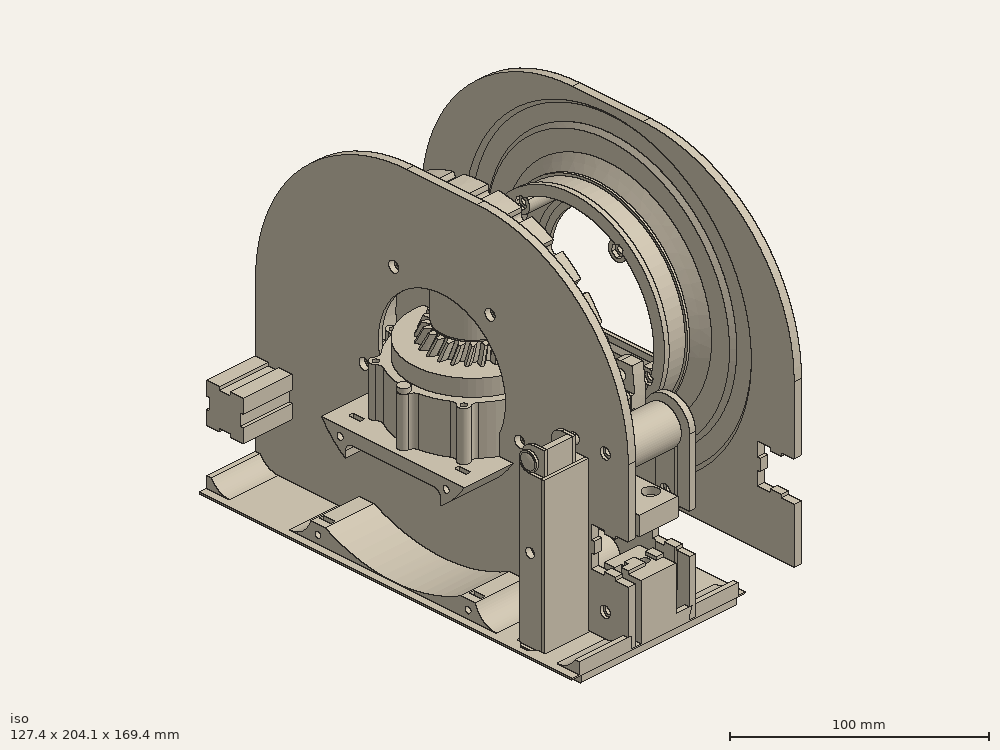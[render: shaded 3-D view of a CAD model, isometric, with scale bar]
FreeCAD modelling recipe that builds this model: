
FCSTD DOCUMENT  (FreeCAD 1.0R38806 (Git))
Label: v12c
License: All rights reserved
LicenseURL: https://en.wikipedia.org/wiki/All_rights_reserved
objects: Sketcher::SketchObject×72, PartDesign::Pad×41, PartDesign::Pocket×27, PartDesign::Body×25, PartDesign::SubShapeBinder×13, PartDesign::Hole×11, PartDesign::Revolution×7, Part::FeaturePython×7, PartDesign::PolarPattern×4, Part::Feature×3, PartDesign::Chamfer×3, App::Part×3, Part::MultiFuse×2, Part::MultiCommon×2, PartDesign::Mirrored×2, App::FeaturePython×1, PartDesign::Groove×1, Part::Cylinder×1, Part::Mirroring×1, App::DocumentObjectGroup×1
note: 480 computed .brp shape members not serialized (recipe doc carries the construction recipe); baked Part::Feature solids carry a one-line shape summary decoded from their .brp

FEATURE [Part::Feature] Body003  label="CyberGear"
  Placement = pos=(0,0,-25) rot=(0,1,0;1.5708rad)
  shape: bbox 80.34 x 79.86 x 36.5 mm, 98 faces (baked)
  expr: .Placement.Base.z = dd.CG_Z
FEATURE [App::FeaturePython] dd  # WARN: FeaturePython — macro-defined, semantics opaque (R4)
  B1_DW = 106.2
  B1_PD = 7
  B1_PL = 10
  CD_Radius = 72.6064
  CG_Z = -25
  CL_BD = 4.9
  CL_BW = 17.4
  CL_Len = 18.2
  CL_Num = 25
  CL_Radius = 6
  D1_X = -30.7
  DynamicData = Created with DynamicData (v2.68) workbench. | This is a simple container object built | for holding custom properties.
  FR_H = 165.613
  FR_W = 204
  G1_Height = 16
  G1_Module = 2
  G1_Num = 24
  G2_Num = 64
  R1_Y = 89.4064
  R2_Y = -56.6064
  R2_Z = -70.8042
  RO_D = 20
  expr: B1_DW = G2_Num * G1_Module - 2 * G1_Height + B1_PD + 3.2 mm
  expr: CD_Radius = CL_Len / (2 * sin(180 / CL_Num))
  expr: CL_BW = 19 - 1.6
  expr: D1_X = -(G1_Num * G1_Module / 2 + CL_BW / 2 - 2 mm)
  expr: FR_H = 2 * (CD_Radius + CL_Radius + 4.2 mm)
  expr: G1_Height = G1_Module * 8
  expr: R1_Y = CD_Radius + CL_Radius + RO_D / 2 + 0.8 mm
  expr: R2_Y = -(CD_Radius - CL_Radius - RO_D / 2)
  expr: R2_Z = -sqrt(pow(R1_Y; 2) - pow(R2_Y; 2)) - 1.6 mm
FEATURE [Sketcher::SketchObject] Sketch  label="CLM_Sketch000"
  ArcFitTolerance = 1e-06
  AttachmentOffset = pos=(0,0,0) rot=(0,1,0;3.14159rad)
  AttachmentSupport = -> [XZ_Plane002]
  FullyConstrained = true
  MakeInternals = false
  MapMode = 5
  Placement = pos=(0,0,0) rot=(0,0.707107,0.707107;3.14159rad)
  expr: Constraints[36] = dd.CL_BW / 2
  sketch-geometry (12):
    g0: LineSegment StartX=-14.7 StartY=4.8 StartZ=0 EndX=-14.7 EndY=2.65 EndZ=0
    g1: LineSegment StartX=-14.7 StartY=2.65 StartZ=0 EndX=-8.7 EndY=2.65 EndZ=0
    g2: LineSegment StartX=-8.7 StartY=2.65 StartZ=0 EndX=-8.7 EndY=2.45 EndZ=0
    g3: LineSegment StartX=-8.7 StartY=2.45 StartZ=0 EndX=10.3 EndY=2.45 EndZ=0
    g4: LineSegment StartX=10.3 StartY=2.45 StartZ=0 EndX=10.3 EndY=4.7 EndZ=0
    g5: LineSegment StartX=-14.7 StartY=4.8 StartZ=0 EndX=-16 EndY=4.8 EndZ=0
    g6: LineSegment StartX=-16 StartY=4.8 StartZ=0 EndX=-16 EndY=3.5 EndZ=0
    g7: LineSegment StartX=-17.0557 StartY=8e-16 StartZ=0 EndX=12.9443 EndY=0 EndZ=0
    g8: LineSegment StartX=11.6 StartY=3.9 StartZ=0 EndX=11.6 EndY=4.7 EndZ=0
    g9: LineSegment StartX=11.6 StartY=4.7 StartZ=0 EndX=10.3 EndY=4.7 EndZ=0
    g10: ArcOfCircle CenterX=-10.7262 CenterY=0 CenterZ=0 NormalX=0 NormalY=0 NormalZ=1 AngleXU=0 Radius=6.3295 StartAngle=2.55567 EndAngle=3.14159
    g11: ArcOfCircle CenterX=6.61476 CenterY=0 CenterZ=0 NormalX=0 NormalY=0 NormalZ=1 AngleXU=0 Radius=6.3295 StartAngle=0 EndAngle=0.66386
  constraints (38):
    c: Vertical(g0)
    c: Coincident(g0,g1)
    c: Horizontal(g1)
    c: Coincident(g1,g2)
    c: Coincident(g2,g3)
    c: Coincident(g3,g4)
    c: Vertical(g4)
    c: Coincident(g0,g5)
    c: Horizontal(g5)
    c: Coincident(g5,g6)
    c: Vertical(g6)
    c: PointOnObject(g7,g-1)
    c: PointOnObject(g7,g-1)
    c: Vertical(g8)
    c: Coincident(g8,g9)
    c: Coincident(g9,g4)
    c: Horizontal(g9)
    c: Vertical(g2)
    c: DistanceX(g3,g3) = 19
    c: DistanceX(g0,g3) = 25
    c: Distance(g5,g-1) = 4.8
    c: DistanceY(g-1,g8) = 4.7
    c: Equal(g5,g9)
    c: Distance(g3,g7) = 2.45
    c: Distance(g0,g7) = 2.65
    c: DistanceX(g9,g9) = 1.3
    c: PointOnObject(g10,g7)
    c: Coincident(g10,g6)
    c: Coincident(g10,g7)
    c: PointOnObject(g11,g7)
    c: Coincident(g11,g8)
    c: Coincident(g11,g7)
    c: Equal(g11,g10)
    c: DistanceX(g7,g7) = 30
    c: Distance(g8,g-1) = 3.9
    c: Equal(g6,g5)
    c: DistanceX(g2,g-1) = 8.7
    c: Horizontal(g3)
FEATURE [PartDesign::Revolution] Revolution  label="CLM_Revolution000"
  Angle = 360
  Angle2 = 60
  Axis = (-1,1e-16,0)
  Base = (0,0,0)
  Placement = pos=(0,0,0) rot=(1,0,0;1.5708rad)
  Profile = -> Sketch
  ReferenceAxis = -> Sketch [H_Axis]
  Refine = true
  Suppressed = false
  Type = 0
FEATURE [PartDesign::Body] Body  label="CLM"
  AllowCompound = false
  Group = -> [Sketch,Revolution]
  Origin = -> Origin002
  Placement = pos=(-30.7,-72.6064,0) rot=(0,0,1;0rad)
  Tip = -> Revolution
  expr: .Placement.Base.x = dd.D1_X
  expr: .Placement.Base.y = -dd.CD_Radius
FEATURE [Sketcher::SketchObject] Sketch001  label="CL1_Sketch001"
  ArcFitTolerance = 1e-06
  AttachmentOffset = pos=(0,0,8.7) rot=(0,0,1;0rad)
  AttachmentSupport = -> [YZ_Plane003]
  FullyConstrained = true
  MakeInternals = false
  MapMode = 5
  Placement = pos=(8.7,0,0) rot=(0.57735,0.57735,0.57735;2.0944rad)
  expr: .AttachmentOffset.Base.z = dd.CL_BW / 2
  expr: Constraints[13] = dd.CL_BD + 0.3 mm
  expr: Constraints[17] = dd.CL_Radius
  expr: Constraints[18] = dd.CL_Radius
  expr: Constraints[19] = dd.CD_Radius
  expr: Constraints[5] = dd.CL_Len
  sketch-geometry (8):
    g0: ArcOfCircle CenterX=0 CenterY=0 CenterZ=0 NormalX=0 NormalY=0 NormalZ=1 AngleXU=0 Radius=6 StartAngle=4.71239 EndAngle=6.28319
    g1: ArcOfCircle CenterX=0 CenterY=18.2 CenterZ=0 NormalX=0 NormalY=0 NormalZ=1 AngleXU=0 Radius=6 StartAngle=0 EndAngle=1.5708
    g2: Circle CenterX=0 CenterY=0 CenterZ=0 NormalX=0 NormalY=0 NormalZ=1 AngleXU=0 Radius=2.6
    g3: Circle CenterX=0 CenterY=18.2 CenterZ=0 NormalX=0 NormalY=0 NormalZ=1 AngleXU=0 Radius=2.6
    g4: LineSegment StartX=6 StartY=18.2 StartZ=0 EndX=6 EndY=0 EndZ=0
    g5: LineSegment StartX=4e-16 StartY=24.2 StartZ=0 EndX=-6 EndY=24.2 EndZ=0
    g6: LineSegment StartX=-1.1e-15 StartY=-6 StartZ=0 EndX=-6 EndY=-6 EndZ=0
    g7: ArcOfCircle CenterX=72.6064 CenterY=9.1 CenterZ=0 NormalX=0 NormalY=0 NormalZ=1 AngleXU=0 Radius=80.0436 StartAngle=2.95181 EndAngle=3.33138
  constraints (20):
    c: Coincident(g0,g-1)
    c: Coincident(g2,g0)
    c: Coincident(g3,g1)
    c: Equal(g3,g2)
    c: PointOnObject(g1,g-2)
    c: DistanceY(g-1,g1) = 18.2
    c: Vertical(g4)
    c: Tangent(g4,g1) = 1.5708
    c: Tangent(g4,g0) = 1.5708
    c: Horizontal(g5)
    c: Horizontal(g6)
    c: Tangent(g0,g6) = 1.5708
    c: Tangent(g1,g5) = -1.5708
    c: Diameter(g3) = 5.2
    c: Coincident(g7,g5)
    c: Coincident(g7,g6)
    c: Equal(g6,g5)
    c: Radius(g1) = 6
    c: DistanceX(g5,g5) = 6
    c: Distance(g7,g-2) = 72.6064
FEATURE [PartDesign::Pad] Pad  label="CL1_Pad000"
  Direction = (1,0,0)
  Length = 6
  Length2 = 10
  Placement = pos=(0,0,0) rot=(1,1,1;2.0944rad)
  Profile = -> Sketch001
  ReferenceAxis = -> Sketch001 [N_Axis]
  Refine = true
  Suppressed = false
  Type = 0
FEATURE [Sketcher::SketchObject] Sketch002  label="CL1_Sketch002"
  ArcFitTolerance = 1e-06
  AttachmentOffset = pos=(0,0,8.7) rot=(0,0,1;0rad)
  AttachmentSupport = -> [YZ_Plane003]
  FullyConstrained = true
  MakeInternals = false
  MapMode = 5
  Placement = pos=(8.7,0,0) rot=(0.57735,0.57735,0.57735;2.0944rad)
  expr: .AttachmentOffset.Base.z = dd.CL_BW / 2
  expr: Constraints[11] = dd.CL_Len
  expr: Constraints[13] = dd.CL_Radius
  expr: Constraints[21] = dd.CL_Radius
  expr: Constraints[26] = dd.CD_Radius
  expr: Constraints[27] = 360 ° / dd.CL_Num
  expr: Constraints[28] = 360 ° / dd.CL_Num
  sketch-geometry (12):
    g0: ArcOfCircle CenterX=0 CenterY=18.2 CenterZ=0 NormalX=0 NormalY=0 NormalZ=1 AngleXU=0 Radius=6 StartAngle=4.71239 EndAngle=6.03186
    g1: ArcOfCircle CenterX=0 CenterY=0 CenterZ=0 NormalX=0 NormalY=0 NormalZ=1 AngleXU=0 Radius=6 StartAngle=0.251327 EndAngle=1.5708
    g2: LineSegment StartX=5.8115 StartY=1.49214 StartZ=0 EndX=6 EndY=0.757976 EndZ=0
    g3: LineSegment StartX=6 StartY=0.757976 StartZ=0 EndX=6 EndY=17.442 EndZ=0
    g4: LineSegment StartX=6 StartY=17.442 StartZ=0 EndX=5.8115 EndY=16.7079 EndZ=0
    g5: LineSegment StartX=-1.1e-15 StartY=12.2 StartZ=0 EndX=-7.37714 EndY=12.2 EndZ=0
    g6: LineSegment StartX=-7.37714 StartY=6 StartZ=0 EndX=-9e-16 EndY=6 EndZ=0
    g7: LineSegment [constr] StartX=0 StartY=18.2 StartZ=0 EndX=0 EndY=24.2 EndZ=0
    g8: LineSegment [constr] StartX=0 StartY=24.2 StartZ=0 EndX=-6 EndY=24.2 EndZ=0
    g9: ArcOfCircle [constr] CenterX=72.6064 CenterY=9.1 CenterZ=0 NormalX=0 NormalY=0 NormalZ=1 AngleXU=0 Radius=80.0436 StartAngle=2.95181 EndAngle=3.10285
    g10: ArcOfCircle CenterX=72.6064 CenterY=9.1 CenterZ=0 NormalX=0 NormalY=0 NormalZ=1 AngleXU=0 Radius=80.0436 StartAngle=3.10285 EndAngle=3.18033
    g11: LineSegment [constr] StartX=0 StartY=9.1 StartZ=0 EndX=6 EndY=9.1 EndZ=0
  constraints (33):
    c: PointOnObject(g0,g-2)
    c: Coincident(g1,g-1)
    c: Coincident(g2,g3)
    c: Vertical(g3)
    c: Coincident(g3,g4)
    c: Horizontal(g5)
    c: Horizontal(g6)
    c: Tangent(g0,g5) = 1.5708
    c: Tangent(g4,g0) = 1.5708
    c: Tangent(g2,g1) = 1.5708
    c: Tangent(g1,g6) = 1.5708
    c: DistanceY(g1,g0) = 18.2
    c: Equal(g1,g0)
    c: Radius(g0) = 6
    c: Coincident(g7,g0)
    c: PointOnObject(g7,g-2)
    c: Coincident(g8,g7)
    c: Horizontal(g8)
    c: Coincident(g9,g8)
    c: Coincident(g9,g5)
    c: Equal(g7,g8)
    c: Distance(g8,g8) = 6
    c: Equal(g5,g6)
    c: Coincident(g10,g9)
    c: Coincident(g10,g5)
    c: Coincident(g10,g6)
    c: Distance(g9,g-2) = 72.6064
    c: Angle(g3,g2) = 0.251327
    c: Angle(g4,g3) = 0.251327
    c: PointOnObject(g11,g-2)
    c: Symmetric(g3,g3,g11)
    c: Horizontal(g11)
    c: Equal(g11,g8)
FEATURE [PartDesign::Pad] Pad001  label="CL1_Pad001"
  BaseFeature = -> Pad
  Direction = (1,0,0)
  Length = 1.6
  Length2 = 10
  Placement = pos=(0,0,0) rot=(1,1,1;2.0944rad)
  Profile = -> Sketch002
  ReferenceAxis = -> Sketch002 [N_Axis]
  Refine = true
  Reversed = true
  Suppressed = false
  Type = 0
FEATURE [Sketcher::SketchObject] Sketch003  label="CL1_Sketch003"
  ArcFitTolerance = 1e-06
  AttachmentOffset = pos=(0,0,8.7) rot=(0,0,1;0rad)
  AttachmentSupport = -> [YZ_Plane003]
  ExternalGeometry = -> [Pad001]
  FullyConstrained = true
  MakeInternals = false
  MapMode = 5
  Placement = pos=(8.7,0,0) rot=(0.57735,0.57735,0.57735;2.0944rad)
  expr: .AttachmentOffset.Base.z = dd.CL_BW / 2
  sketch-geometry (10):
    g0: LineSegment [constr] StartX=-7.37714 StartY=12.2 StartZ=0 EndX=-7.37714 EndY=9.1 EndZ=0
    g1: LineSegment [constr] StartX=-7.37714 StartY=9.1 StartZ=0 EndX=-7.37714 EndY=6 EndZ=0
    g2: LineSegment [constr] StartX=-7.37714 StartY=9.1 StartZ=0 EndX=-4.88857 EndY=9.1 EndZ=0
    g3: LineSegment [constr] StartX=-4.88857 StartY=9.1 StartZ=0 EndX=-2.4 EndY=9.1 EndZ=0
    g4: LineSegment StartX=-6.17714 StartY=11 StartZ=0 EndX=-6.17714 EndY=7.2 EndZ=0
    g5: LineSegment StartX=-6.17714 StartY=7.2 StartZ=0 EndX=-2.4 EndY=7.2 EndZ=0
    g6: LineSegment StartX=-2.4 StartY=7.2 StartZ=0 EndX=-2.4 EndY=11 EndZ=0
    g7: LineSegment StartX=-2.4 StartY=11 StartZ=0 EndX=-6.17714 EndY=11 EndZ=0
    g8: LineSegment [constr] StartX=-7.37714 StartY=12.2 StartZ=0 EndX=-6.17714 EndY=12.2 EndZ=0
    g9: LineSegment [constr] StartX=-6.17714 StartY=12.2 StartZ=0 EndX=-6.17714 EndY=11 EndZ=0
  constraints (27):
    c: Coincident(g0,g-3)
    c: Coincident(g1,g0)
    c: Coincident(g1,g-3)
    c: Coincident(g2,g0)
    c: Horizontal(g2)
    c: Coincident(g3,g2)
    c: Horizontal(g3)
    c: Equal(g1,g0)
    c: Equal(g2,g3)
    c: DistanceX(g3,g-1) = 2.4
    c: Vertical(g1)
    c: Coincident(g4,g5)
    c: Coincident(g5,g6)
    c: Coincident(g6,g7)
    c: Coincident(g7,g4)
    c: Vertical(g4)
    c: Horizontal(g5)
    c: Horizontal(g7)
    c: Coincident(g8,g0)
    c: Horizontal(g8)
    c: Coincident(g9,g8)
    c: Coincident(g9,g4)
    c: Vertical(g9)
    c: Symmetric(g6,g5,g3)
    c: PointOnObject(g3,g6)
    c: Equal(g9,g8)
    c: Distance(g8,g8) = 1.2
FEATURE [PartDesign::Pad] Pad002  label="CL1_Pad002"
  BaseFeature = -> Pad001
  Direction = (1,0,0)
  Length = 18.2
  Length2 = 10
  Placement = pos=(0,0,0) rot=(1,1,1;2.0944rad)
  Profile = -> Sketch003
  ReferenceAxis = -> Sketch003 [N_Axis]
  Refine = true
  Reversed = true
  Suppressed = false
  Type = 0
  expr: Length = dd.CL_BW + 0.8 mm
FEATURE [PartDesign::Body] Body004  label="ChainLink1"
  AllowCompound = false
  Group = -> [Sketch001,Pad,Sketch002,Pad001,Sketch003,Pad002]
  Origin = -> Origin003
  Placement = pos=(0,-72.6064,0) rot=(1,0,0;0rad)
  Tip = -> Pad002
  expr: .Placement.Base.y = -dd.CD_Radius
  expr: .Placement.Rotation.Angle = -180 ° / dd.CL_Num * 0
FEATURE [Sketcher::SketchObject] Sketch004  label="CL2_Sketch004"
  ArcFitTolerance = 1e-06
  AttachmentOffset = pos=(0,0,-8.7) rot=(0,0,1;0rad)
  AttachmentSupport = -> [YZ_Plane004]
  FullyConstrained = true
  MakeInternals = false
  MapMode = 5
  Placement = pos=(-8.7,0,0) rot=(0.57735,0.57735,0.57735;2.0944rad)
  expr: .AttachmentOffset.Base.z = -dd.CL_BW / 2
  expr: Constraints[10] = dd.CL_Len
  expr: Constraints[11] = dd.CD_Radius
  expr: Constraints[12] = dd.CL_Radius
  expr: Constraints[13] = dd.CL_Radius
  expr: Constraints[17] = dd.CL_BD
  sketch-geometry (8):
    g0: ArcOfCircle CenterX=0 CenterY=18.2 CenterZ=0 NormalX=0 NormalY=0 NormalZ=1 AngleXU=0 Radius=6 StartAngle=0 EndAngle=1.5708
    g1: ArcOfCircle CenterX=0 CenterY=0 CenterZ=0 NormalX=0 NormalY=0 NormalZ=1 AngleXU=0 Radius=6 StartAngle=4.71239 EndAngle=6.28319
    g2: ArcOfCircle CenterX=72.6064 CenterY=9.1 CenterZ=0 NormalX=0 NormalY=0 NormalZ=1 AngleXU=0 Radius=80.0436 StartAngle=2.95181 EndAngle=3.33138
    g3: LineSegment StartX=6 StartY=-1.5e-15 StartZ=0 EndX=6 EndY=18.2 EndZ=0
    g4: LineSegment StartX=4e-16 StartY=24.2 StartZ=0 EndX=-6 EndY=24.2 EndZ=0
    g5: LineSegment StartX=-1.1e-15 StartY=-6 StartZ=0 EndX=-6 EndY=-6 EndZ=0
    g6: Circle CenterX=0 CenterY=18.2 CenterZ=0 NormalX=0 NormalY=0 NormalZ=1 AngleXU=0 Radius=2.45
    g7: Circle CenterX=0 CenterY=0 CenterZ=0 NormalX=0 NormalY=0 NormalZ=1 AngleXU=0 Radius=2.45
  constraints (20):
    c: PointOnObject(g0,g-2)
    c: Coincident(g1,g-1)
    c: Vertical(g3)
    c: Horizontal(g4)
    c: Horizontal(g5)
    c: Tangent(g3,g0) = -1.5708
    c: Tangent(g1,g3) = -1.5708
    c: Tangent(g1,g5) = 1.5708
    c: Tangent(g0,g4) = -1.5708
    c: Coincident(g5,g2)
    c: DistanceY(g1,g0) = 18.2
    c: Distance(g2,g-2) = 72.6064
    c: Radius(g0) = 6
    c: DistanceX(g4,g4) = 6
    c: Coincident(g6,g0)
    c: Coincident(g7,g1)
    c: Equal(g7,g6)
    c: Diameter(g7) = 4.9
    c: Coincident(g2,g4)
    c: Equal(g5,g4)
FEATURE [PartDesign::Pad] Pad003  label="CL2_Pad003"
  Direction = (1,0,0)
  Length = 1.6
  Length2 = 10
  Placement = pos=(0,0,0) rot=(1,1,1;2.0944rad)
  Profile = -> Sketch004
  ReferenceAxis = -> Sketch004 [N_Axis]
  Refine = true
  Reversed = true
  Suppressed = false
  Type = 0
FEATURE [Sketcher::SketchObject] Sketch005  label="CL2_Sketch005"
  ArcFitTolerance = 1e-06
  AttachmentOffset = pos=(0,0,-8.7) rot=(0,0,1;0rad)
  AttachmentSupport = -> [YZ_Plane004]
  ExternalGeometry = -> [Pad003]
  FullyConstrained = true
  MakeInternals = false
  MapMode = 5
  Placement = pos=(-8.7,0,0) rot=(0.57735,0.57735,0.57735;2.0944rad)
  expr: .AttachmentOffset.Base.z = -dd.CL_BW / 2
  expr: Constraints[15] = dd.CL_Len
  expr: Constraints[17] = dd.CL_Radius
  expr: Constraints[18] = dd.CL_Radius
  expr: Constraints[19] = 360 ° / dd.CL_Num
  sketch-geometry (9):
    g0: ArcOfCircle CenterX=0 CenterY=18.2 CenterZ=0 NormalX=0 NormalY=0 NormalZ=1 AngleXU=0 Radius=6 StartAngle=4.71239 EndAngle=6.03186
    g1: ArcOfCircle CenterX=0 CenterY=0 CenterZ=0 NormalX=0 NormalY=0 NormalZ=1 AngleXU=0 Radius=6 StartAngle=0.251327 EndAngle=1.5708
    g2: LineSegment StartX=5.8115 StartY=16.7079 StartZ=0 EndX=6 EndY=17.442 EndZ=0
    g3: LineSegment StartX=6 StartY=17.442 StartZ=0 EndX=6 EndY=0.757976 EndZ=0
    g4: LineSegment StartX=6 StartY=0.757976 StartZ=0 EndX=5.8115 EndY=1.49214 EndZ=0
    g5: ArcOfCircle CenterX=72.6064 CenterY=9.1 CenterZ=0 NormalX=0 NormalY=0 NormalZ=1 AngleXU=0 Radius=80.0436 StartAngle=3.10285 EndAngle=3.18033
    g6: LineSegment StartX=-7.37714 StartY=12.2 StartZ=0 EndX=-9e-16 EndY=12.2 EndZ=0
    g7: LineSegment StartX=-7.37714 StartY=6 StartZ=0 EndX=-9e-16 EndY=6 EndZ=0
    g8: LineSegment [constr] StartX=5.8115 StartY=16.7079 StartZ=0 EndX=5.8115 EndY=1.49214 EndZ=0
  constraints (23):
    c: PointOnObject(g0,g-2)
    c: Coincident(g1,g-1)
    c: Coincident(g2,g3)
    c: Vertical(g3)
    c: Coincident(g3,g4)
    c: Tangent(g4,g1) = -1.5708
    c: Tangent(g2,g0) = -1.5708
    c: Coincident(g5,g-3)
    c: Coincident(g6,g5)
    c: Horizontal(g6)
    c: Coincident(g7,g5)
    c: Horizontal(g7)
    c: Tangent(g0,g6) = -1.5708
    c: Tangent(g1,g7) = 1.5708
    c: Equal(g-3,g5)
    c: DistanceY(g1,g0) = 18.2
    c: Equal(g0,g1)
    c: Radius(g0) = 6
    c: DistanceX(g1,g3) = 6
    c: Angle(g3,g4) = 0.251327
    c: Coincident(g8,g0)
    c: Coincident(g8,g1)
    c: Vertical(g8)
FEATURE [PartDesign::Pad] Pad004  label="CL2_Pad004"
  BaseFeature = -> Pad003
  Direction = (1,0,0)
  Length = 1.6
  Length2 = 10
  Placement = pos=(0,0,0) rot=(1,1,1;2.0944rad)
  Profile = -> Sketch005
  ReferenceAxis = -> Sketch005 [N_Axis]
  Refine = true
  Suppressed = false
  Type = 0
FEATURE [Sketcher::SketchObject] Sketch007  label="CL3_Sketch007"
  ArcFitTolerance = 1e-06
  AttachmentOffset = pos=(0,0,8.7) rot=(0,0,1;0rad)
  AttachmentSupport = -> [YZ_Plane005]
  FullyConstrained = true
  MakeInternals = false
  MapMode = 5
  Placement = pos=(8.7,0,0) rot=(0.57735,0.57735,0.57735;2.0944rad)
  expr: .AttachmentOffset.Base.z = dd.CL_BW / 2
  expr: Constraints[16] = dd.CL_Radius
  expr: Constraints[17] = dd.CL_Radius
  expr: Constraints[18] = dd.CD_Radius
  expr: Constraints[2] = dd.CL_Len
  expr: Constraints[4] = dd.CL_BD
  sketch-geometry (8):
    g0: Circle CenterX=0 CenterY=0 CenterZ=0 NormalX=0 NormalY=0 NormalZ=1 AngleXU=0 Radius=2.45
    g1: Circle CenterX=0 CenterY=-18.2 CenterZ=0 NormalX=0 NormalY=0 NormalZ=1 AngleXU=0 Radius=2.45
    g2: ArcOfCircle CenterX=72.6064 CenterY=-9.1 CenterZ=0 NormalX=0 NormalY=0 NormalZ=1 AngleXU=0 Radius=80.0436 StartAngle=2.95181 EndAngle=3.33138
    g3: ArcOfCircle CenterX=0 CenterY=0 CenterZ=0 NormalX=0 NormalY=0 NormalZ=1 AngleXU=0 Radius=6 StartAngle=1e-16 EndAngle=1.5708
    g4: ArcOfCircle CenterX=0 CenterY=-18.2 CenterZ=0 NormalX=0 NormalY=0 NormalZ=1 AngleXU=0 Radius=6 StartAngle=4.71239 EndAngle=6.28319
    g5: LineSegment StartX=-6 StartY=-24.2 StartZ=0 EndX=-9e-16 EndY=-24.2 EndZ=0
    g6: LineSegment StartX=-6 StartY=6 StartZ=0 EndX=0 EndY=6 EndZ=0
    g7: LineSegment StartX=6 StartY=6e-16 StartZ=0 EndX=6 EndY=-18.2 EndZ=0
  constraints (20):
    c: Coincident(g0,g-1)
    c: PointOnObject(g1,g-2)
    c: DistanceY(g1,g0) = 18.2
    c: Equal(g1,g0)
    c: Diameter(g1) = 4.9
    c: Coincident(g3,g0)
    c: Coincident(g4,g1)
    c: Coincident(g5,g2)
    c: Horizontal(g5)
    c: Coincident(g6,g2)
    c: Horizontal(g6)
    c: Vertical(g7)
    c: Tangent(g6,g3) = 1.5708
    c: Tangent(g3,g7) = 1.5708
    c: Tangent(g7,g4) = 1.5708
    c: Tangent(g4,g5) = -1.5708
    c: Radius(g3) = 6
    c: DistanceX(g6,g6) = 6
    c: Distance(g2,g-2) = 72.6064
    c: Equal(g5,g6)
FEATURE [PartDesign::Pad] Pad005  label="CL3_Pad005"
  Direction = (1,0,0)
  Length = 1.6
  Length2 = 10
  Placement = pos=(0,0,0) rot=(1,1,1;2.0944rad)
  Profile = -> Sketch007
  ReferenceAxis = -> Sketch007 [N_Axis]
  Refine = true
  Reversed = true
  Suppressed = false
  Type = 0
FEATURE [Sketcher::SketchObject] Sketch008  label="CL3_Sketch008"
  ArcFitTolerance = 1e-06
  AttachmentOffset = pos=(0,0,8.7) rot=(0,0,1;0rad)
  AttachmentSupport = -> [YZ_Plane005]
  ExternalGeometry = -> [Pad005]
  FullyConstrained = true
  MakeInternals = false
  MapMode = 5
  Placement = pos=(8.7,0,0) rot=(0.57735,0.57735,0.57735;2.0944rad)
  expr: .AttachmentOffset.Base.z = dd.CL_BW / 2
  expr: Constraints[15] = dd.CL_Radius
  expr: Constraints[21] = 360 ° / dd.CL_Num
  expr: Constraints[3] = dd.CL_Len
  expr: Constraints[4] = dd.CL_Radius
  sketch-geometry (9):
    g0: ArcOfCircle CenterX=0 CenterY=-18.2 CenterZ=0 NormalX=0 NormalY=0 NormalZ=1 AngleXU=0 Radius=6 StartAngle=0.251327 EndAngle=1.5708
    g1: ArcOfCircle CenterX=0 CenterY=0 CenterZ=0 NormalX=0 NormalY=0 NormalZ=1 AngleXU=0 Radius=6 StartAngle=4.71239 EndAngle=6.03186
    g2: ArcOfCircle CenterX=72.6064 CenterY=-9.1 CenterZ=0 NormalX=0 NormalY=0 NormalZ=1 AngleXU=0 Radius=80.0436 StartAngle=3.10285 EndAngle=3.18033
    g3: LineSegment StartX=-7.37714 StartY=-6 StartZ=0 EndX=-9e-16 EndY=-6 EndZ=0
    g4: LineSegment StartX=-7.37714 StartY=-12.2 StartZ=0 EndX=-9e-16 EndY=-12.2 EndZ=0
    g5: LineSegment StartX=5.8115 StartY=-1.49214 StartZ=0 EndX=6 EndY=-0.757976 EndZ=0
    g6: LineSegment StartX=6 StartY=-0.757976 StartZ=0 EndX=6 EndY=-17.442 EndZ=0
    g7: LineSegment StartX=6 StartY=-17.442 StartZ=0 EndX=5.8115 EndY=-16.7079 EndZ=0
    g8: LineSegment [constr] StartX=5.8115 StartY=-16.7079 StartZ=0 EndX=5.8115 EndY=-1.49214 EndZ=0
  constraints (23):
    c: PointOnObject(g0,g-2)
    c: Coincident(g1,g-1)
    c: Coincident(g2,g-3)
    c: Distance(g0,g1) = 18.2
    c: Radius(g1) = 6
    c: Equal(g1,g0)
    c: Coincident(g3,g2)
    c: Horizontal(g3)
    c: Coincident(g4,g2)
    c: Horizontal(g4)
    c: Tangent(g1,g3) = -1.5708
    c: Tangent(g0,g4) = 1.5708
    c: Coincident(g5,g6)
    c: Vertical(g6)
    c: Coincident(g6,g7)
    c: Distance(g5,g-2) = 6
    c: Tangent(g1,g5) = -1.5708
    c: Tangent(g0,g7) = -1.5708
    c: Coincident(g8,g0)
    c: Coincident(g8,g1)
    c: Vertical(g8)
    c: Angle(g5,g6) = 0.251327
    c: Equal(g2,g-3)
FEATURE [PartDesign::Pad] Pad006  label="CL3_Pad006"
  BaseFeature = -> Pad005
  Direction = (1,0,0)
  Length = 6
  Length2 = 10
  Placement = pos=(0,0,0) rot=(1,1,1;2.0944rad)
  Profile = -> Sketch008
  ReferenceAxis = -> Sketch008 [N_Axis]
  Refine = true
  Suppressed = false
  Type = 0
FEATURE [Sketcher::SketchObject] Sketch010  label="CL4_Sketch010"
  ArcFitTolerance = 1e-06
  AttachmentOffset = pos=(0,0,-8.7) rot=(0,0,1;0rad)
  AttachmentSupport = -> [YZ_Plane006]
  FullyConstrained = true
  MakeInternals = false
  MapMode = 5
  Placement = pos=(-8.7,0,0) rot=(0.57735,0.57735,0.57735;2.0944rad)
  expr: .AttachmentOffset.Base.z = -dd.CL_BW / 2
  expr: Constraints[16] = dd.CL_Radius
  expr: Constraints[17] = dd.CL_Radius
  expr: Constraints[18] = dd.CD_Radius
  expr: Constraints[2] = dd.CL_Len
  expr: Constraints[4] = dd.CL_BD
  sketch-geometry (8):
    g0: Circle CenterX=0 CenterY=0 CenterZ=0 NormalX=0 NormalY=0 NormalZ=1 AngleXU=0 Radius=2.45
    g1: Circle CenterX=0 CenterY=-18.2 CenterZ=0 NormalX=0 NormalY=0 NormalZ=1 AngleXU=0 Radius=2.45
    g2: ArcOfCircle CenterX=72.6064 CenterY=-9.1 CenterZ=0 NormalX=0 NormalY=0 NormalZ=1 AngleXU=0 Radius=80.0436 StartAngle=2.95181 EndAngle=3.33138
    g3: ArcOfCircle CenterX=0 CenterY=0 CenterZ=0 NormalX=0 NormalY=0 NormalZ=1 AngleXU=0 Radius=6 StartAngle=1e-16 EndAngle=1.5708
    g4: ArcOfCircle CenterX=0 CenterY=-18.2 CenterZ=0 NormalX=0 NormalY=0 NormalZ=1 AngleXU=0 Radius=6 StartAngle=4.71239 EndAngle=6.28319
    g5: LineSegment StartX=-6 StartY=-24.2 StartZ=0 EndX=-9e-16 EndY=-24.2 EndZ=0
    g6: LineSegment StartX=-6 StartY=6 StartZ=0 EndX=0 EndY=6 EndZ=0
    g7: LineSegment StartX=6 StartY=6e-16 StartZ=0 EndX=6 EndY=-18.2 EndZ=0
  constraints (20):
    c: Coincident(g0,g-1)
    c: PointOnObject(g1,g-2)
    c: DistanceY(g1,g0) = 18.2
    c: Equal(g1,g0)
    c: Diameter(g1) = 4.9
    c: Coincident(g3,g0)
    c: Coincident(g4,g1)
    c: Coincident(g5,g2)
    c: Horizontal(g5)
    c: Coincident(g6,g2)
    c: Horizontal(g6)
    c: Vertical(g7)
    c: Tangent(g6,g3) = 1.5708
    c: Tangent(g3,g7) = 1.5708
    c: Tangent(g7,g4) = 1.5708
    c: Tangent(g4,g5) = -1.5708
    c: Radius(g3) = 6
    c: DistanceX(g6,g6) = 6
    c: Distance(g2,g-2) = 72.6064
    c: Equal(g5,g6)
FEATURE [PartDesign::Pad] Pad007  label="CL4_Pad007"
  Direction = (1,0,0)
  Length = 1.6
  Length2 = 10
  Placement = pos=(0,0,0) rot=(1,1,1;2.0944rad)
  Profile = -> Sketch010
  ReferenceAxis = -> Sketch010 [N_Axis]
  Refine = true
  Suppressed = false
  Type = 0
FEATURE [Sketcher::SketchObject] Sketch011  label="CL4_Sketch011"
  ArcFitTolerance = 1e-06
  AttachmentOffset = pos=(0,0,-8.7) rot=(0,0,1;0rad)
  AttachmentSupport = -> [YZ_Plane006]
  ExternalGeometry = -> [Pad007]
  FullyConstrained = true
  MakeInternals = false
  MapMode = 5
  Placement = pos=(-8.7,0,0) rot=(0.57735,0.57735,0.57735;2.0944rad)
  expr: .AttachmentOffset.Base.z = -dd.CL_BW / 2
  expr: Constraints[15] = dd.CL_Radius
  expr: Constraints[21] = 360 ° / dd.CL_Num
  expr: Constraints[3] = dd.CL_Len
  expr: Constraints[4] = dd.CL_Radius
  sketch-geometry (9):
    g0: ArcOfCircle CenterX=0 CenterY=-18.2 CenterZ=0 NormalX=0 NormalY=0 NormalZ=1 AngleXU=0 Radius=6 StartAngle=0.251327 EndAngle=1.5708
    g1: ArcOfCircle CenterX=0 CenterY=0 CenterZ=0 NormalX=0 NormalY=0 NormalZ=1 AngleXU=0 Radius=6 StartAngle=4.71239 EndAngle=6.03186
    g2: ArcOfCircle CenterX=72.6064 CenterY=-9.1 CenterZ=0 NormalX=0 NormalY=0 NormalZ=1 AngleXU=0 Radius=80.0436 StartAngle=3.10285 EndAngle=3.18033
    g3: LineSegment StartX=-7.37714 StartY=-6 StartZ=0 EndX=-9e-16 EndY=-6 EndZ=0
    g4: LineSegment StartX=-7.37714 StartY=-12.2 StartZ=0 EndX=-9e-16 EndY=-12.2 EndZ=0
    g5: LineSegment StartX=5.8115 StartY=-1.49214 StartZ=0 EndX=6 EndY=-0.757976 EndZ=0
    g6: LineSegment StartX=6 StartY=-0.757976 StartZ=0 EndX=6 EndY=-17.442 EndZ=0
    g7: LineSegment StartX=6 StartY=-17.442 StartZ=0 EndX=5.8115 EndY=-16.7079 EndZ=0
    g8: LineSegment [constr] StartX=5.8115 StartY=-16.7079 StartZ=0 EndX=5.8115 EndY=-1.49214 EndZ=0
  constraints (23):
    c: PointOnObject(g0,g-2)
    c: Coincident(g1,g-1)
    c: Coincident(g2,g-3)
    c: Distance(g0,g1) = 18.2
    c: Radius(g1) = 6
    c: Equal(g1,g0)
    c: Coincident(g3,g2)
    c: Horizontal(g3)
    c: Coincident(g4,g2)
    c: Horizontal(g4)
    c: Tangent(g1,g3) = -1.5708
    c: Tangent(g0,g4) = 1.5708
    c: Coincident(g5,g6)
    c: Vertical(g6)
    c: Coincident(g6,g7)
    c: Distance(g5,g-2) = 6
    c: Tangent(g1,g5) = -1.5708
    c: Tangent(g0,g7) = -1.5708
    c: Coincident(g8,g0)
    c: Coincident(g8,g1)
    c: Vertical(g8)
    c: Angle(g5,g6) = 0.251327
    c: Equal(g2,g-3)
FEATURE [PartDesign::Pad] Pad008  label="CL4_Pad008"
  BaseFeature = -> Pad007
  Direction = (1,0,0)
  Length = 1.6
  Length2 = 10
  Placement = pos=(0,0,0) rot=(1,1,1;2.0944rad)
  Profile = -> Sketch011
  ReferenceAxis = -> Sketch011 [N_Axis]
  Refine = true
  Reversed = true
  Suppressed = false
  Type = 0
FEATURE [Part::FeaturePython] LanternGear  label="CD_LanternGear000"  # WARN: FeaturePython — macro-defined, semantics opaque (R4)
  AttacherType = Attacher::AttachEngine3D
  AttachmentOffset = pos=(0,0,-6.7) rot=(0,0,1;0.125664rad)
  AttachmentSupport = -> [YZ_Plane001]
  MapMode = 5
  Placement = pos=(-6.7,0,0) rot=(0.600057,0.529021,0.600057;2.1684rad)
  bolt_radius = 2.45
  head = 0
  height = 13.4
  module = 5.80852
  num_profiles = 10
  num_teeth = 25
  version = 1.3.0
  expr: .AttachmentOffset.Base.z = -height / 2
  expr: .AttachmentOffset.Rotation.Angle = 180 ° / dd.CL_Num
  expr: bolt_radius = dd.CL_BD / 2
  expr: height = dd.CL_BW - 4 mm
  expr: module = 2 * dd.CD_Radius / dd.CL_Num
  expr: num_teeth = dd.CL_Num
FEATURE [Part::FeaturePython] BevelGear  label="CD_BevelGear000"  # WARN: FeaturePython — macro-defined, semantics opaque (R4)
  AttacherType = Attacher::AttachEngine3D
  AttachmentOffset = pos=(0,0,6.7) rot=(0,0,1;0rad)
  AttachmentSupport = -> [YZ_Plane001]
  MapMode = 5
  Placement = pos=(6.7,0,0) rot=(0.57735,0.57735,0.57735;2.0944rad)
  angular_backlash = 0
  backlash = 0
  beta = -5.625
  clearance = 0.1
  dw = 128
  height = 7.5
  module = 2
  num_teeth = 64
  numpoints = 20
  pitch_angle = 69.444
  pressure_angle = 20
  reset_origin = true
  version = 1.3.0
  expr: .AttachmentOffset.Base.z = -dd.G1_Num * dd.G1_Module / 2 - dd.D1_X
  expr: angular_backlash = backlash / dw * 360 ° / pi
  expr: beta = -360 ° / num_teeth
  expr: dw = num_teeth * module
  expr: height = (dd.G1_Height + dd.G1_Module * 2) * dd.G1_Num / dd.G2_Num
  expr: module = dd.G1_Module
  expr: num_teeth = dd.G2_Num
  expr: pitch_angle = atan(dd.G2_Num / dd.G1_Num)
FEATURE [Part::FeaturePython] BevelGear001  label="G1_BevelGear001"  # WARN: FeaturePython — macro-defined, semantics opaque (R4)
  AttacherType = Attacher::AttachEngine3D
  Placement = pos=(0,0,0) rot=(0,0,1;0.1309rad)
  angular_backlash = 0
  backlash = 0
  beta = 5.625
  clearance = 0.1
  dw = 48
  height = 16
  module = 2
  num_teeth = 24
  numpoints = 20
  pitch_angle = 20.556
  pressure_angle = 20
  reset_origin = true
  version = 1.3.0
  expr: .Placement.Rotation.Angle = 180 ° / dd.G1_Num
  expr: angular_backlash = backlash / dw * 360 ° / pi
  expr: beta = 360 ° / dd.G2_Num
  expr: dw = num_teeth * module
  expr: height = dd.G1_Height
  expr: module = dd.G1_Module
  expr: num_teeth = dd.G1_Num
  expr: pitch_angle = 90 ° - <<CD_BevelGear000>>.pitch_angle
FEATURE [Sketcher::SketchObject] Sketch015  label="CD_Sketch015"
  ArcFitTolerance = 1e-06
  AttachmentSupport = -> [XZ_Plane009]
  FullyConstrained = true
  MakeInternals = false
  MapMode = 5
  Placement = pos=(0,0,0) rot=(1,0,0;1.5708rad)
  expr: Constraints[10] = dd.CL_BW - 4 mm
  expr: Constraints[11] = dd.CD_Radius + dd.CL_BD
  expr: Constraints[12] = (dd.G1_Height + dd.G1_Module * 2) * dd.G1_Num / dd.G2_Num
  expr: Constraints[13] = dd.G1_Height
  expr: Constraints[15] = dd.G2_Num * dd.G1_Module / 2
  expr: Constraints[23] = dd.B1_PL
  expr: Constraints[24] = (dd.B1_DW + dd.B1_PD) / 2
  expr: Constraints[33] = dd.G1_Module * 2.5
  sketch-geometry (12):
    g0: LineSegment StartX=14.2 StartY=-48 StartZ=0 EndX=14.2 EndY=-64 EndZ=0
    g1: LineSegment StartX=14.2 StartY=-64 StartZ=0 EndX=6.7 EndY=-64 EndZ=0
    g2: LineSegment StartX=6.7 StartY=-64 StartZ=0 EndX=6.7 EndY=-77.5064 EndZ=0
    g3: LineSegment StartX=6.7 StartY=-77.5064 StartZ=0 EndX=-6.7 EndY=-77.5064 EndZ=0
    g4: LineSegment StartX=-6.7 StartY=-77.5064 StartZ=0 EndX=-6.7 EndY=-55.4 EndZ=0
    g5: LineSegment StartX=-6.7 StartY=-55.4 StartZ=0 EndX=-5.5 EndY=-55.4 EndZ=0
    g6: LineSegment StartX=-5.5 StartY=-55.4 StartZ=0 EndX=-5.5 EndY=-56.6 EndZ=0
    g7: LineSegment StartX=-5.5 StartY=-56.6 StartZ=0 EndX=4.5 EndY=-56.6 EndZ=0
    g8: LineSegment StartX=4.5 StartY=-56.6 StartZ=0 EndX=4.5 EndY=-55.4 EndZ=0
    g9: LineSegment StartX=4.5 StartY=-55.4 StartZ=0 EndX=6.7 EndY=-55.4 EndZ=0
    g10: LineSegment StartX=6.7 StartY=-55.4 StartZ=0 EndX=9.2 EndY=-48 EndZ=0
    g11: LineSegment StartX=9.2 StartY=-48 StartZ=0 EndX=14.2 EndY=-48 EndZ=0
  constraints (35):
    c: Coincident(g11,g0)
    c: Vertical(g0)
    c: Coincident(g0,g1)
    c: Coincident(g1,g2)
    c: Vertical(g2)
    c: Coincident(g2,g3)
    c: Coincident(g3,g4)
    c: Coincident(g4,g5)
    c: Vertical(g4)
    c: Symmetric(g2,g3,g-2)
    c: Distance(g3,g3) = 13.4
    c: Distance(g3,g-1) = 77.5064
    c: Distance(g1,g1) = 7.5
    c: DistanceY(g0,g0) = 16
    c: Horizontal(g1)
    c: Distance(g0,g-1) = 64
    c: Coincident(g5,g6)
    c: Horizontal(g5)
    c: Coincident(g6,g7)
    c: Vertical(g6)
    c: Coincident(g7,g8)
    c: Horizontal(g7)
    c: Vertical(g8)
    c: DistanceX(g7,g7) = 10
    c: Distance(g7,g-1) = 56.6
    c: Coincident(g8,g9)
    c: Coincident(g9,g10)
    c: Horizontal(g9)
    c: Equal(g8,g6)
    c: Equal(g6,g5)
    c: Distance(g5,g5) = 1.2
    c: Coincident(g10,g11)
    c: Horizontal(g11)
    c: Distance(g11,g11) = 5
    c: PointOnObject(g9,g2)
FEATURE [PartDesign::Revolution] Revolution001  label="CD_Revolution001"
  Angle = 360
  Angle2 = 60
  Axis = (1,0,0)
  Base = (0,0,0)
  Placement = pos=(0,0,0) rot=(1,0,0;1.5708rad)
  Profile = -> Sketch015
  ReferenceAxis = -> Sketch015 [H_Axis]
  Refine = true
  Reversed = true
  Suppressed = false
  Type = 0
FEATURE [PartDesign::Body] Body009  label="CD_Comm"
  AllowCompound = false
  Group = -> [Sketch015,Revolution001]
  Origin = -> Origin009
  Tip = -> Revolution001
FEATURE [PartDesign::SubShapeBinder] Binder001  label="CD_Binder001"
  BindCopyOnChange = 0
  BindMode = 0
  ClaimChildren = false
  Context = -> Part001 [Body010.Binder001.]
  Fuse = false
  MakeFace = true
  OffsetFill = false
  OffsetIntersection = false
  OffsetJoinType = 0
  OffsetOpenResult = false
  PartialLoad = false
  Refine = true
  Relative = true
  Support = -> [LanternGear[Face102]]
  _Version = 2
FEATURE [Sketcher::SketchObject] Sketch016  label="CD_Sketch016"
  ArcFitTolerance = 1e-06
  AttachmentSupport = -> [YZ_Plane010]
  ExternalGeometry = -> [Binder001]
  FullyConstrained = true
  MakeInternals = false
  MapMode = 5
  Placement = pos=(0,0,0) rot=(0.57735,0.57735,0.57735;2.0944rad)
  expr: Constraints[10] = dd.CL_BD
  sketch-geometry (9):
    g0: LineSegment [constr] StartX=0 StartY=0 StartZ=0 EndX=-52.9312 EndY=-49.7057 EndZ=0
    g1: LineSegment [constr] StartX=-54.578 StartY=-47.8916 StartZ=0 EndX=0 EndY=0 EndZ=0
    g2: LineSegment [constr] StartX=-64.2932 StartY=-38.7279 StartZ=0 EndX=-52.9312 EndY=-49.7057 EndZ=0
    g3: LineSegment [constr] StartX=-42.6885 StartY=-61.7346 StartZ=0 EndX=-52.9312 EndY=-49.7057 EndZ=0
    g4: Circle CenterX=-52.9312 CenterY=-49.7057 CenterZ=0 NormalX=0 NormalY=0 NormalZ=1 AngleXU=0 Radius=2.45
    g5: ArcOfCircle CenterX=-32.7449 CenterY=-30.7495 CenterZ=0 NormalX=0 NormalY=0 NormalZ=1 AngleXU=0 Radius=32.5415 StartAngle=3.38929 EndAngle=4.40186
    g6: LineSegment StartX=-64.2932 StartY=-38.7279 StartZ=0 EndX=-32.7449 EndY=-30.7495 EndZ=0
    g7: LineSegment StartX=-32.7449 StartY=-30.7495 StartZ=0 EndX=-42.6885 EndY=-61.7346 EndZ=0
    g8: LineSegment [constr] StartX=-54.7171 StartY=-51.3828 StartZ=0 EndX=-56.4667 EndY=-53.0257 EndZ=0
  constraints (23):
    c: Coincident(g0,g-1)
    c: Coincident(g1,g-6)
    c: Coincident(g1,g0)
    c: Equal(g0,g1)
    c: Coincident(g2,g-3)
    c: Coincident(g2,g0)
    c: Coincident(g3,g-4)
    c: Coincident(g3,g0)
    c: Equal(g3,g2)
    c: Coincident(g4,g0)
    c: Diameter(g4) = 4.9
    c: PointOnObject(g5,g0)
    c: Coincident(g5,g6)
    c: Coincident(g6,g5)
    c: Coincident(g6,g7)
    c: Coincident(g7,g5)
    c: Coincident(g5,g3)
    c: PointOnObject(g5,g2)
    c: PointOnObject(g8,g4)
    c: PointOnObject(g8,g5)
    c: Parallel(g8,g0)
    c: PointOnObject(g8,g0)
    c: Distance(g8,g8) = 2.4
FEATURE [PartDesign::Pad] Pad010  label="CD_Pad010"
  Direction = (1,0,0)
  Length = 13.4
  Length2 = 10
  Midplane = true
  Placement = pos=(0,0,0) rot=(1,1,1;2.0944rad)
  Profile = -> Sketch016
  ReferenceAxis = -> Sketch016 [N_Axis]
  Refine = true
  Suppressed = false
  Type = 0
  expr: Length = dd.CL_BW - 4 mm
FEATURE [PartDesign::Body] Body010  label="CD_Add"
  AllowCompound = false
  Group = -> [Binder001,Sketch016,Pad010]
  Origin = -> Origin010
  Tip = -> Pad010
FEATURE [Part::MultiFuse] Fusion  label="CD_Fusion000"
  Refine = true
  Shapes = -> [BevelGear,LanternGear,Body010]
FEATURE [Part::MultiCommon] Common  label="CD_Common000"
  Refine = true
  Shapes = -> [Body009,Fusion]
FEATURE [Sketcher::SketchObject] Sketch017  label="B1S_Sketch017"
  ArcFitTolerance = 1e-06
  AttachmentSupport = -> [YZ_Plane011]
  FullyConstrained = true
  MakeInternals = false
  MapMode = 5
  Placement = pos=(0,0,0) rot=(0.57735,0.57735,0.57735;2.0944rad)
  expr: Constraints[2] = dd.B1_DW - 1.6 mm
  expr: Constraints[3] = dd.B1_DW + 1.6 mm
  sketch-geometry (2):
    g0: Circle CenterX=0 CenterY=0 CenterZ=0 NormalX=0 NormalY=0 NormalZ=1 AngleXU=0 Radius=52.3
    g1: Circle CenterX=0 CenterY=0 CenterZ=0 NormalX=0 NormalY=0 NormalZ=1 AngleXU=0 Radius=53.9
  constraints (4):
    c: Coincident(g0,g-1)
    c: Coincident(g1,g0)
    c: Diameter(g0) = 104.6
    c: Diameter(g1) = 107.8
FEATURE [PartDesign::Pad] Pad011  label="B1S_Pad011"
  Direction = (1,0,0)
  Length = 6.2
  Length2 = 7
  Placement = pos=(0,0,0) rot=(1,1,1;2.0944rad)
  Profile = -> Sketch017
  ReferenceAxis = -> Sketch017 [N_Axis]
  Refine = true
  Reversed = true
  Suppressed = false
  Type = 4
  expr: Length = dd.B1_PL / 2 + 1.2 mm
  expr: Length2 = dd.B1_PL / 2 + 2 mm
FEATURE [Sketcher::SketchObject] Sketch018  label="B1S_Sketch018"
  ArcFitTolerance = 1e-06
  AttachmentOffset = pos=(0,53.1,0) rot=(0,0,1;0rad)
  AttachmentSupport = -> [XZ_Plane011]
  ExternalGeometry = -> [Pad011]
  FullyConstrained = true
  MakeInternals = false
  MapMode = 5
  Placement = pos=(0,1.18e-14,53.1) rot=(1,0,0;1.5708rad)
  expr: .AttachmentOffset.Base.y = dd.B1_DW / 2
  expr: Constraints[15] = dd.B1_PD / 2 + 0.1 mm
  expr: Constraints[16] = dd.B1_PL + 0.4 mm
  sketch-geometry (8):
    g0: LineSegment StartX=-5.2 StartY=3.6 StartZ=0 EndX=5.2 EndY=3.6 EndZ=0
    g1: LineSegment StartX=5.2 StartY=3.6 StartZ=0 EndX=5.2 EndY=1.2 EndZ=0
    g2: LineSegment StartX=5.2 StartY=1.2 StartZ=0 EndX=5 EndY=1 EndZ=0
    g3: LineSegment StartX=5 StartY=1 StartZ=0 EndX=5 EndY=2e-16 EndZ=0
    g4: LineSegment StartX=5 StartY=2e-16 StartZ=0 EndX=-5 EndY=0 EndZ=0
    g5: LineSegment StartX=-5 StartY=0 StartZ=0 EndX=-5 EndY=1 EndZ=0
    g6: LineSegment StartX=-5 StartY=1 StartZ=0 EndX=-5.2 EndY=1.2 EndZ=0
    g7: LineSegment StartX=-5.2 StartY=1.2 StartZ=0 EndX=-5.2 EndY=3.6 EndZ=0
  constraints (22):
    c: Horizontal(g0)
    c: Coincident(g0,g1)
    c: Vertical(g1)
    c: Coincident(g1,g2)
    c: Coincident(g2,g3)
    c: PointOnObject(g3,g-1)
    c: Vertical(g3)
    c: Coincident(g3,g4)
    c: PointOnObject(g4,g-1)
    c: Coincident(g4,g5)
    c: Vertical(g5)
    c: Coincident(g5,g6)
    c: Coincident(g6,g7)
    c: Coincident(g7,g0)
    c: Vertical(g7)
    c: Distance(g0,g-1) = 3.6
    c: DistanceX(g0,g0) = 10.4
    c: Symmetric(g6,g1,g-2)
    c: Symmetric(g5,g2,g-2)
    c: Perpendicular(g2,g6)
    c: DistanceX(g6,g4) = 0.2
    c: DistanceY(g3,g1) = 1.2
FEATURE [PartDesign::Groove] Groove  label="B1S_Groove000"
  Angle = 360
  Angle2 = 60
  Axis = (1,0,0)
  Base = (0,1.18e-14,53.1)
  BaseFeature = -> Pad011
  Placement = pos=(0,0,0) rot=(1,1,1;2.0944rad)
  Profile = -> Sketch018
  ReferenceAxis = -> Sketch018 [H_Axis]
  Refine = true
  Reversed = true
  Suppressed = false
  Type = 0
FEATURE [PartDesign::PolarPattern] PolarPattern  label="B1S_PolarPattern000"
  Angle = 360
  Axis = -> X_Axis011
  BaseFeature = -> Groove
  Mode = 0
  Occurrences = 24
  Offset = 120
  Originals = -> [Groove]
  Placement = pos=(0,0,0) rot=(1,1,1;2.0944rad)
  Refine = true
  Suppressed = false
  TransformMode = 0
FEATURE [PartDesign::Chamfer] Chamfer  label="B1S_Chamfer000"
  Angle = 45
  Base = -> PolarPattern [Edge10]
  BaseFeature = -> PolarPattern
  ChamferType = 0
  FlipDirection = false
  Placement = pos=(0,0,0) rot=(1,1,1;2.0944rad)
  Refine = true
  Size = 0.8
  Size2 = 1
  SupportTransform = false
  Suppressed = false
  UseAllEdges = false
FEATURE [PartDesign::Body] Body011  label="Bearing1_Separator"
  AllowCompound = false
  Group = -> [Sketch017,Pad011,Sketch018,Groove,PolarPattern,Chamfer]
  Origin = -> Origin011
  Tip = -> Chamfer
FEATURE [PartDesign::SubShapeBinder] Binder002  label="F1_Binder002"
  BindCopyOnChange = 0
  BindMode = 0
  ClaimChildren = false
  Context = -> Part001 [Body012.Binder002.]
  Fuse = false
  MakeFace = true
  OffsetFill = false
  OffsetIntersection = false
  OffsetJoinType = 0
  OffsetOpenResult = false
  PartialLoad = false
  Refine = true
  Relative = true
  Support = -> [Common[Edge299,Edge1325,Edge1453,Edge1456,Edge294]]
  _Version = 2
FEATURE [Sketcher::SketchObject] Sketch019  label="F1_Sketch019"
  ArcFitTolerance = 1e-06
  AttachmentSupport = -> [XZ_Plane012]
  ExternalGeometry = -> [Binder002]
  FullyConstrained = true
  MakeInternals = false
  MapMode = 5
  Placement = pos=(0,0,0) rot=(1,0,0;1.5708rad)
  expr: Constraints[10] = (dd.B1_DW - dd.B1_PD) / 2
  sketch-geometry (12):
    g0: LineSegment StartX=-14.7 StartY=-46.4 StartZ=0 EndX=-14.7 EndY=-56.8 EndZ=0
    g1: LineSegment StartX=-5.5 StartY=-50.8 StartZ=0 EndX=-5.5 EndY=-49.6 EndZ=0
    g2: LineSegment StartX=-5.5 StartY=-49.6 StartZ=0 EndX=4.5 EndY=-49.6 EndZ=0
    g3: LineSegment StartX=4.5 StartY=-49.6 StartZ=0 EndX=4.5 EndY=-50.8 EndZ=0
    g4: LineSegment StartX=4.5 StartY=-50.8 StartZ=0 EndX=7.05405 EndY=-50.8 EndZ=0
    g5: LineSegment StartX=7.05405 StartY=-50.8 StartZ=0 EndX=8.54054 EndY=-46.4 EndZ=0
    g6: LineSegment [constr] StartX=9.2 StartY=-48 StartZ=0 EndX=8 EndY=-48 EndZ=0
    g7: LineSegment StartX=-6.7 StartY=-50.8 StartZ=0 EndX=-5.5 EndY=-50.8 EndZ=0
    g8: LineSegment StartX=8.54054 StartY=-46.4 StartZ=0 EndX=-14.7 EndY=-46.4 EndZ=0
    g9: LineSegment StartX=-6.7 StartY=-50.8 StartZ=0 EndX=-12.7 EndY=-56.8 EndZ=0
    g10: LineSegment StartX=-12.7 StartY=-56.8 StartZ=0 EndX=-14.7 EndY=-56.8 EndZ=0
    g11: LineSegment [constr] StartX=-6.7 StartY=-50.8 StartZ=0 EndX=-6.7 EndY=-55.4 EndZ=0
  constraints (35):
    c: Vertical(g0)
    c: Coincident(g7,g1)
    c: Vertical(g1)
    c: Coincident(g1,g2)
    c: Horizontal(g2)
    c: Coincident(g2,g3)
    c: Vertical(g3)
    c: Coincident(g3,g4)
    c: Horizontal(g4)
    c: Coincident(g4,g5)
    c: Distance(g1,g-1) = 49.6
    c: Parallel(g-3,g5)
    c: Coincident(g5,g8)
    c: Coincident(g6,g-3)
    c: PointOnObject(g6,g5)
    c: Horizontal(g6)
    c: Equal(g3,g6)
    c: PointOnObject(g-5,g3)
    c: PointOnObject(g-4,g1)
    c: Equal(g1,g3)
    c: Distance(g1,g1) = 1.2
    c: Horizontal(g7)
    c: Horizontal(g8)
    c: DistanceY(g2,g5) = 3.2
    c: Coincident(g8,g0)
    c: Coincident(g7,g9)
    c: Coincident(g9,g10)
    c: Coincident(g10,g0)
    c: Horizontal(g10)
    c: Coincident(g11,g7)
    c: Coincident(g11,g-4)
    c: Vertical(g11)
    c: DistanceX(g9,g7) = 6
    c: Distance(g10,g10) = 2
    c: Angle(g2,g9) = 0.785398
FEATURE [PartDesign::Revolution] Revolution002  label="F1_Revolution002"
  Angle = 360
  Angle2 = 60
  Axis = (1,0,0)
  Base = (0,0,0)
  Placement = pos=(0,0,0) rot=(1,0,0;1.5708rad)
  Profile = -> Sketch019
  ReferenceAxis = -> Sketch019 [H_Axis]
  Refine = true
  Reversed = true
  Suppressed = false
  Type = 0
FEATURE [PartDesign::SubShapeBinder] Binder003  label="FM_Binder003"
  BindCopyOnChange = 0
  BindMode = 0
  ClaimChildren = false
  Context = -> Body013 [Binder003.]
  Fuse = false
  MakeFace = true
  OffsetFill = false
  OffsetIntersection = false
  OffsetJoinType = 0
  OffsetOpenResult = false
  PartialLoad = false
  Refine = true
  Relative = true
  Support = -> [Part[Body003.Face2]]
  _Version = 2
FEATURE [Sketcher::SketchObject] Sketch020  label="FM_Sketch020"
  ArcFitTolerance = 1e-06
  AttachmentSupport = -> [YZ_Plane013]
  FullyConstrained = true
  MakeInternals = false
  MapMode = 5
  Placement = pos=(0,0,0) rot=(0.57735,0.57735,0.57735;2.0944rad)
  expr: Constraints[1] = dd.B1_DW - dd.B1_PD - 6.4 mm
  expr: Constraints[9] = -dd.CG_Z
  sketch-geometry (14):
    g0: Circle [constr] CenterX=0 CenterY=0 CenterZ=0 NormalX=0 NormalY=0 NormalZ=1 AngleXU=0 Radius=46.4
    g1: ArcOfCircle CenterX=0 CenterY=0 CenterZ=0 NormalX=0 NormalY=0 NormalZ=1 AngleXU=0 Radius=46.4 StartAngle=3.7106 EndAngle=4.1179
    g2: ArcOfCircle CenterX=0 CenterY=0 CenterZ=0 NormalX=0 NormalY=0 NormalZ=1 AngleXU=0 Radius=46.4 StartAngle=5.30688 EndAngle=5.71418
    g3: LineSegment StartX=-39.0891 StartY=-25 StartZ=0 EndX=39.0891 EndY=-25 EndZ=0
    g4: Circle [constr] CenterX=-29.0262 CenterY=-29.8 CenterZ=0 NormalX=0 NormalY=0 NormalZ=1 AngleXU=0 Radius=4.8
    g5: LineSegment StartX=-25.988 StartY=-34.9197 StartZ=0 EndX=-25.988 EndY=-38.4394 EndZ=0
    g6: LineSegment StartX=25.988 StartY=-38.4394 StartZ=0 EndX=25.988 EndY=-34.9197 EndZ=0
    g7: LineSegment StartX=22.4683 StartY=-31.4 StartZ=0 EndX=-22.4683 EndY=-31.4 EndZ=0
    g8: LineSegment [constr] StartX=-29.0262 StartY=-29.8 StartZ=0 EndX=-32.3754 EndY=-33.2385 EndZ=0
    g9: LineSegment [constr] StartX=-29.0262 StartY=-29.8 StartZ=0 EndX=-29.0262 EndY=-25 EndZ=0
    g10: ArcOfCircle CenterX=-22.4683 CenterY=-34.9197 CenterZ=0 NormalX=0 NormalY=0 NormalZ=1 AngleXU=0 Radius=3.51968 StartAngle=1.5708 EndAngle=3.14159
    g11: ArcOfCircle CenterX=22.4683 CenterY=-34.9197 CenterZ=0 NormalX=0 NormalY=0 NormalZ=1 AngleXU=0 Radius=3.51968 StartAngle=0 EndAngle=1.5708
    g12: GeomPoint [constr] X=-25.2427 Y=-32.7538 Z=0
    g13: LineSegment [constr] StartX=-22.4683 StartY=-34.9197 StartZ=0 EndX=-25.2427 EndY=-32.7538 EndZ=0
  constraints (36):
    c: Coincident(g0,g-1)
    c: Diameter(g0) = 92.8
    c: Coincident(g1,g0)
    c: Coincident(g2,g0)
    c: Coincident(g3,g1)
    c: Coincident(g3,g2)
    c: Horizontal(g3)
    c: Coincident(g6,g2)
    c: Coincident(g5,g1)
    c: Distance(g2,g-1) = 25
    c: Equal(g2,g0)
    c: Equal(g1,g0)
    c: Diameter(g4) = 9.6
    c: Vertical(g5)
    c: Vertical(g6)
    c: Coincident(g8,g4)
    c: PointOnObject(g8,g0)
    c: PointOnObject(g8,g4)
    c: PointOnObject(g0,g8)
    c: Coincident(g9,g4)
    c: PointOnObject(g9,g4)
    c: Vertical(g9)
    c: PointOnObject(g9,g3)
    c: Tangent(g5,g10) = -1.5708
    c: Tangent(g7,g10) = -1.5708
    c: Tangent(g6,g11) = -1.5708
    c: Tangent(g7,g11) = -1.5708
    c: Symmetric(g11,g10,g-2)
    c: Equal(g10,g11)
    c: DistanceY(g7,g2) = 6.4
    c: PointOnObject(g12,g10)
    c: Coincident(g13,g10)
    c: Coincident(g13,g12)
    c: PointOnObject(g12,g4)
    c: Equal(g13,g5)
    c: PointOnObject(g4,g13)
FEATURE [Sketcher::SketchObject] Sketch021  label="FM_Sketch021"
  ArcFitTolerance = 1e-06
  AttachmentOffset = pos=(0,0,-31.4) rot=(0,0,1;0rad)
  AttachmentSupport = -> [XY_Plane013]
  ExternalGeometry = -> [Binder003]
  FullyConstrained = true
  MakeInternals = false
  MapMode = 5
  Placement = pos=(0,0,-31.4) rot=(0,0,1;0rad)
  expr: .AttachmentOffset.Base.z = dd.CG_Z - 6.4 mm
  sketch-geometry (10):
    g0: Circle CenterX=-28.7267 CenterY=24.1045 CenterZ=0 NormalX=0 NormalY=0 NormalZ=1 AngleXU=0 Radius=1.5
    g1: Circle CenterX=-6.51181 CenterY=36.9303 CenterZ=0 NormalX=0 NormalY=0 NormalZ=1 AngleXU=0 Radius=1.5
    g2: Circle CenterX=18.75 CenterY=32.476 CenterZ=0 NormalX=0 NormalY=0 NormalZ=1 AngleXU=0 Radius=1.5
    g3: Circle CenterX=35.2385 CenterY=12.8258 CenterZ=0 NormalX=0 NormalY=0 NormalZ=1 AngleXU=0 Radius=1.5
    g4: Circle CenterX=35.2385 CenterY=-12.8258 CenterZ=0 NormalX=0 NormalY=0 NormalZ=1 AngleXU=0 Radius=1.5
    g5: Circle CenterX=18.75 CenterY=-32.476 CenterZ=0 NormalX=0 NormalY=0 NormalZ=1 AngleXU=0 Radius=1.5
    g6: Circle CenterX=-6.51181 CenterY=-36.9303 CenterZ=0 NormalX=0 NormalY=0 NormalZ=1 AngleXU=0 Radius=1.5
    g7: Circle CenterX=-28.7267 CenterY=-24.1045 CenterZ=0 NormalX=0 NormalY=0 NormalZ=1 AngleXU=0 Radius=1.5
    g8: Circle CenterX=-37.5 CenterY=-4.2e-15 CenterZ=0 NormalX=0 NormalY=0 NormalZ=1 AngleXU=0 Radius=1.5
    g9: Circle CenterX=0 CenterY=0 CenterZ=0 NormalX=0 NormalY=0 NormalZ=1 AngleXU=0 Radius=18.6
  constraints (20):
    c: Coincident(g0,g-4)
    c: Equal(g0,g-4)
    c: Coincident(g1,g-5)
    c: Equal(g1,g-5)
    c: Coincident(g2,g-6)
    c: Equal(g2,g-6)
    c: Coincident(g3,g-7)
    c: Equal(g3,g-7)
    c: Coincident(g4,g-8)
    c: Equal(g4,g-8)
    c: Coincident(g5,g-9)
    c: Equal(g5,g-9)
    c: Coincident(g6,g-10)
    c: Equal(g6,g-10)
    c: Coincident(g7,g-11)
    c: Equal(g7,g-11)
    c: Coincident(g8,g-3)
    c: Equal(g8,g-3)
    c: Coincident(g9,g-1)
    c: Diameter(g9) = 37.2
FEATURE [PartDesign::Pad] Pad012  label="FM_Pad012"
  Direction = (1,0,0)
  Length = 86.8
  Length2 = 10
  Midplane = true
  Placement = pos=(0,0,0) rot=(1,1,1;2.0944rad)
  Profile = -> Sketch020
  ReferenceAxis = -> Sketch020 [N_Axis]
  Refine = true
  Suppressed = false
  Type = 0
FEATURE [Sketcher::SketchObject] Sketch022  label="FM_Sketch022"
  ArcFitTolerance = 1e-06
  AttachmentOffset = pos=(0,0,-25) rot=(0,0,1;0rad)
  AttachmentSupport = -> [XY_Plane013]
  ExternalGeometry = -> [Binder003]
  FullyConstrained = true
  MakeInternals = false
  MapMode = 5
  Placement = pos=(0,0,-25) rot=(0,0,1;0rad)
  expr: .AttachmentOffset.Base.z = dd.CG_Z
  sketch-geometry (2):
    g0: Circle CenterX=30 CenterY=0 CenterZ=0 NormalX=0 NormalY=0 NormalZ=1 AngleXU=0 Radius=2.8
    g1: Circle CenterX=0 CenterY=0 CenterZ=0 NormalX=0 NormalY=0 NormalZ=1 AngleXU=0 Radius=21.5
  constraints (4):
    c: Coincident(g0,g-3)
    c: Coincident(g1,g-1)
    c: Equal(g1,g-4)
    c: Diameter(g0) = 5.6
FEATURE [Sketcher::SketchObject] Sketch023  label="FM_Sketch023"
  ArcFitTolerance = 1e-06
  AttachmentSupport = -> [YZ_Plane013]
  ExternalGeometry = -> [Pad012]
  FullyConstrained = true
  MakeInternals = false
  MapMode = 5
  Placement = pos=(0,0,0) rot=(0.57735,0.57735,0.57735;2.0944rad)
  expr: Constraints[22] = dd.FR_W
  expr: Constraints[29] = -dd.R2_Y
  sketch-geometry (23):
    g0: LineSegment [constr] StartX=-82 StartY=-29.8 StartZ=0 EndX=82 EndY=-29.8 EndZ=0
    g1: ArcOfCircle CenterX=-82 CenterY=-29.8 CenterZ=0 NormalX=0 NormalY=0 NormalZ=1 AngleXU=0 Radius=4.8 StartAngle=4.71239 EndAngle=5.94335
    g2: ArcOfCircle CenterX=-56.6064 CenterY=-29.8 CenterZ=0 NormalX=0 NormalY=0 NormalZ=1 AngleXU=0 Radius=4.8 StartAngle=3.48143 EndAngle=5.94335
    g3: ArcOfCircle CenterX=56.6064 CenterY=-29.8 CenterZ=0 NormalX=0 NormalY=0 NormalZ=1 AngleXU=0 Radius=4.8 StartAngle=3.48143 EndAngle=5.94335
    g4: ArcOfCircle CenterX=82 CenterY=-29.8 CenterZ=0 NormalX=0 NormalY=0 NormalZ=1 AngleXU=0 Radius=4.8 StartAngle=3.48143 EndAngle=4.71239
    g5: LineSegment StartX=-77.4745 StartY=-31.4 StartZ=0 EndX=-61.1319 EndY=-31.4 EndZ=0
    g6: LineSegment StartX=-52.081 StartY=-31.4 StartZ=0 EndX=52.081 EndY=-31.4 EndZ=0
    g7: LineSegment StartX=61.1319 StartY=-31.4 StartZ=0 EndX=77.4745 EndY=-31.4 EndZ=0
    g8: LineSegment StartX=-102 StartY=-34.6 StartZ=0 EndX=-102 EndY=-25 EndZ=0
    g9: LineSegment StartX=-102 StartY=-25 StartZ=0 EndX=102 EndY=-25 EndZ=0
    g10: LineSegment StartX=102 StartY=-25 StartZ=0 EndX=102 EndY=-34.6 EndZ=0
    g11: LineSegment [constr] StartX=61.1319 StartY=-31.4 StartZ=0 EndX=56.6064 EndY=-29.8 EndZ=0
    g12: LineSegment [constr] StartX=56.6064 StartY=-29.8 StartZ=0 EndX=56.6064 EndY=-25 EndZ=0
    g13: LineSegment StartX=89 StartY=-34.6 StartZ=0 EndX=82 EndY=-34.6 EndZ=0
    g14: LineSegment StartX=89 StartY=-36.2 StartZ=0 EndX=89 EndY=-34.6 EndZ=0
    g15: LineSegment StartX=95 StartY=-36.2 StartZ=0 EndX=89 EndY=-36.2 EndZ=0
    g16: LineSegment StartX=102 StartY=-34.6 StartZ=0 EndX=95 EndY=-34.6 EndZ=0
    g17: LineSegment StartX=95 StartY=-34.6 StartZ=0 EndX=95 EndY=-36.2 EndZ=0
    g18: LineSegment StartX=-95 StartY=-34.6 StartZ=0 EndX=-102 EndY=-34.6 EndZ=0
    g19: LineSegment StartX=-95 StartY=-36.2 StartZ=0 EndX=-95 EndY=-34.6 EndZ=0
    g20: LineSegment StartX=-89 StartY=-36.2 StartZ=0 EndX=-95 EndY=-36.2 EndZ=0
    g21: LineSegment StartX=-82 StartY=-34.6 StartZ=0 EndX=-89 EndY=-34.6 EndZ=0
    g22: LineSegment StartX=-89 StartY=-34.6 StartZ=0 EndX=-89 EndY=-36.2 EndZ=0
  constraints (65):
    c: Horizontal(g5)
    c: Horizontal(g6)
    c: Horizontal(g7)
    c: PointOnObject(g-4,g6)
    c: PointOnObject(g-4,g7)
    c: PointOnObject(g-4,g5)
    c: Coincident(g1,g5)
    c: Coincident(g2,g5)
    c: Coincident(g2,g6)
    c: Coincident(g3,g6)
    c: Coincident(g7,g3)
    c: Coincident(g4,g7)
    c: Equal(g4,g3)
    c: Equal(g3,g2)
    c: Equal(g2,g1)
    c: Coincident(g18,g8)
    c: Vertical(g8)
    c: Coincident(g8,g9)
    c: Horizontal(g9)
    c: Coincident(g9,g10)
    c: Vertical(g10)
    c: Coincident(g10,g16)
    c: DistanceX(g9,g9) = 204
    c: PointOnObject(g-3,g9)
    c: Symmetric(g10,g18,g-2)
    c: Radius(g3) = 4.8
    c: Symmetric(g4,g1,g-2)
    c: Distance(g16,g13) = 20
    c: Coincident(g0,g1)
    c: Distance(g2,g-2) = 56.6064
    c: Coincident(g0,g4)
    c: PointOnObject(g3,g0)
    c: Symmetric(g2,g3,g-2)
    c: Coincident(g11,g3)
    c: Coincident(g11,g3)
    c: Coincident(g12,g3)
    c: PointOnObject(g12,g9)
    c: Vertical(g12)
    c: Equal(g12,g11)
    c: Coincident(g14,g13)
    c: Horizontal(g13)
    c: Coincident(g15,g14)
    c: Coincident(g17,g15)
    c: Horizontal(g15)
    c: Coincident(g16,g17)
    c: Horizontal(g16)
    c: Vertical(g14)
    c: Vertical(g17)
    c: Equal(g13,g16)
    c: DistanceX(g15,g15) = 6
    c: Coincident(g19,g18)
    c: Coincident(g20,g19)
    c: Coincident(g22,g20)
    c: Coincident(g21,g22)
    c: Horizontal(g18)
    c: Vertical(g19)
    c: Horizontal(g20)
    c: Vertical(g22)
    c: Horizontal(g21)
    c: Symmetric(g14,g20,g-2)
    c: Equal(g18,g21)
    c: Tangent(g4,g13) = 1.5708
    c: Distance(g19,g19) = 1.6
    c: Equal(g19,g22)
    c: Tangent(g1,g21) = 1.5708
FEATURE [PartDesign::Pad] Pad013  label="FM_Pad013"
  BaseFeature = -> Pad012
  Direction = (1,0,0)
  Length = 21.2
  Length2 = 10
  Midplane = true
  Placement = pos=(0,0,0) rot=(1,1,1;2.0944rad)
  Profile = -> Sketch023
  ReferenceAxis = -> Sketch023 [N_Axis]
  Refine = true
  Suppressed = false
  Type = 0
FEATURE [PartDesign::Pocket] Pocket004  label="FM_Pocket004"
  BaseFeature = -> Pad013
  Direction = (0,0,-1)
  Length = 2.2
  Length2 = 5
  Placement = pos=(0,0,0) rot=(1,1,1;2.0944rad)
  Profile = -> Sketch022
  ReferenceAxis = -> Sketch022 [N_Axis]
  Refine = true
  Suppressed = false
  Type = 0
FEATURE [Sketcher::SketchObject] Sketch026  label="FM_Sketch026"
  ArcFitTolerance = 1e-06
  AttachmentSupport = -> [Pocket004]
  ExternalGeometry = -> [Pocket004]
  FullyConstrained = true
  MakeInternals = false
  MapMode = 5
  Placement = pos=(43.4,0,0) rot=(0.57735,0.57735,0.57735;2.0944rad)
  sketch-geometry (6):
    g0: Circle CenterX=29.0262 CenterY=-29.8 CenterZ=0 NormalX=0 NormalY=0 NormalZ=1 AngleXU=0 Radius=1.65
    g1: Circle [constr] CenterX=29.0262 CenterY=-29.8 CenterZ=0 NormalX=0 NormalY=0 NormalZ=1 AngleXU=0 Radius=4.8
    g2: LineSegment [constr] StartX=29.0262 StartY=-29.8 StartZ=0 EndX=29.0262 EndY=-25 EndZ=0
    g3: LineSegment [constr] StartX=29.0262 StartY=-29.8 StartZ=0 EndX=32.3754 EndY=-33.2385 EndZ=0
    g4: LineSegment [constr] StartX=29.0262 StartY=-29.8 StartZ=0 EndX=25.2427 EndY=-32.7538 EndZ=0
    g5: Circle CenterX=-29.0262 CenterY=-29.8 CenterZ=0 NormalX=0 NormalY=0 NormalZ=1 AngleXU=0 Radius=1.65
  constraints (16):
    c: Diameter(g0) = 3.3
    c: Coincident(g1,g0)
    c: Coincident(g2,g0)
    c: PointOnObject(g2,g1)
    c: Vertical(g2)
    c: Coincident(g3,g0)
    c: PointOnObject(g3,g1)
    c: Coincident(g4,g0)
    c: PointOnObject(g4,g1)
    c: PointOnObject(g2,g-5)
    c: PointOnObject(g3,g-4)
    c: PointOnObject(g-1,g3)
    c: PointOnObject(g4,g-3)
    c: PointOnObject(g-3,g4)
    c: Symmetric(g5,g0,g-2)
    c: Equal(g5,g0)
FEATURE [PartDesign::Pocket] Pocket006  label="FM_Pocket006"
  BaseFeature = -> Pocket004
  Direction = (-1,0,0)
  Length = 12
  Length2 = 5
  Placement = pos=(0,0,0) rot=(1,1,1;2.0944rad)
  Profile = -> Sketch026
  ReferenceAxis = -> Sketch026 [N_Axis]
  Refine = true
  Suppressed = false
  Type = 0
  expr: Length = 12 mm
FEATURE [Sketcher::SketchObject] Sketch027  label="FM_Sketch027"
  ArcFitTolerance = 1e-06
  AttachmentOffset = pos=(0,0,-8) rot=(0,0,1;0rad)
  AttachmentSupport = -> [Pocket006]
  ExternalGeometry = -> [Pocket006]
  FullyConstrained = true
  MakeInternals = false
  MapMode = 5
  Placement = pos=(35.4,0,0) rot=(0.57735,0.57735,0.57735;2.0944rad)
  sketch-geometry (20):
    g0: LineSegment [constr] StartX=30.6428 StartY=-27 StartZ=0 EndX=27.4096 EndY=-27 EndZ=0
    g1: LineSegment [constr] StartX=27.4096 StartY=-27 StartZ=0 EndX=25.793 EndY=-29.8 EndZ=0
    g2: LineSegment StartX=25.793 StartY=-29.8 StartZ=0 EndX=27.4096 EndY=-32.6 EndZ=0
    g3: LineSegment StartX=27.4096 StartY=-32.6 StartZ=0 EndX=30.6428 EndY=-32.6 EndZ=0
    g4: LineSegment StartX=30.6428 StartY=-32.6 StartZ=0 EndX=32.2594 EndY=-29.8 EndZ=0
    g5: LineSegment [constr] StartX=32.2594 StartY=-29.8 StartZ=0 EndX=30.6428 EndY=-27 EndZ=0
    g6: Circle [constr] CenterX=29.0262 CenterY=-29.8 CenterZ=0 NormalX=0 NormalY=0 NormalZ=1 AngleXU=0 Radius=3.23316
    g7: LineSegment [constr] StartX=-25.793 StartY=-29.8 StartZ=0 EndX=-27.4096 EndY=-27 EndZ=0
    g8: LineSegment [constr] StartX=-27.4096 StartY=-27 StartZ=0 EndX=-30.6428 EndY=-27 EndZ=0
    g9: LineSegment [constr] StartX=-30.6428 StartY=-27 StartZ=0 EndX=-32.2594 EndY=-29.8 EndZ=0
    g10: LineSegment StartX=-32.2594 StartY=-29.8 StartZ=0 EndX=-30.6428 EndY=-32.6 EndZ=0
    g11: LineSegment StartX=-30.6428 StartY=-32.6 StartZ=0 EndX=-27.4096 EndY=-32.6 EndZ=0
    g12: LineSegment StartX=-27.4096 StartY=-32.6 StartZ=0 EndX=-25.793 EndY=-29.8 EndZ=0
    g13: Circle [constr] CenterX=-29.0262 CenterY=-29.8 CenterZ=0 NormalX=0 NormalY=0 NormalZ=1 AngleXU=0 Radius=3.23316
    g14: LineSegment StartX=-32.2594 StartY=-29.8 StartZ=0 EndX=-32.2594 EndY=-25 EndZ=0
    g15: LineSegment StartX=-32.2594 StartY=-25 StartZ=0 EndX=-25.793 EndY=-25 EndZ=0
    g16: LineSegment StartX=-25.793 StartY=-25 StartZ=0 EndX=-25.793 EndY=-29.8 EndZ=0
    g17: LineSegment StartX=25.793 StartY=-29.8 StartZ=0 EndX=25.793 EndY=-25 EndZ=0
    g18: LineSegment StartX=25.793 StartY=-25 StartZ=0 EndX=32.2594 EndY=-25 EndZ=0
    g19: LineSegment StartX=32.2594 StartY=-25 StartZ=0 EndX=32.2594 EndY=-29.8 EndZ=0
  constraints (48):
    c: Coincident(g0,g1)
    c: Coincident(g1,g2)
    c: Coincident(g2,g3)
    c: Coincident(g3,g4)
    c: Coincident(g4,g5)
    c: Coincident(g5,g0)
    c: Equal(g0, g1-g5) x5
    c: PointOnObject(g0,g6)
    c: PointOnObject(g1,g6)
    c: PointOnObject(g2,g6)
    c: PointOnObject(g3,g6)
    c: PointOnObject(g4,g6)
    c: PointOnObject(g5,g6)
    c: Horizontal(g0)
    c: DistanceY(g2,g0) = 5.6
    c: Coincident(g6,g-3)
    c: Coincident(g7,g8)
    c: Coincident(g8,g9)
    c: Coincident(g9,g10)
    c: Coincident(g10,g11)
    c: Coincident(g11,g12)
    c: Coincident(g12,g7)
    c: Equal(g7, g8-g12) x5
    c: PointOnObject(g7,g13)
    c: PointOnObject(g8,g13)
    c: PointOnObject(g9,g13)
    c: PointOnObject(g10,g13)
    c: PointOnObject(g11,g13)
    c: PointOnObject(g12,g13)
    c: Coincident(g13,g-4)
    c: Equal(g13,g6)
    c: Horizontal(g11)
    c: Coincident(g9,g14)
    c: PointOnObject(g14,g-5)
    c: Vertical(g14)
    c: Coincident(g14,g15)
    c: PointOnObject(g15,g-5)
    c: Coincident(g15,g16)
    c: Coincident(g16,g7)
    c: Coincident(g1,g17)
    c: PointOnObject(g17,g-5)
    c: Vertical(g17)
    c: Coincident(g18,g19)
    c: Coincident(g19,g4)
    c: Vertical(g19)
    c: Horizontal(g18)
    c: Coincident(g18,g17)
    c: Vertical(g16)
FEATURE [PartDesign::Pocket] Pocket007  label="FM_Pocket007"
  BaseFeature = -> Pocket006
  Direction = (-1,0,0)
  Length = 2.4
  Length2 = 5
  Placement = pos=(0,0,0) rot=(1,1,1;2.0944rad)
  Profile = -> Sketch027
  ReferenceAxis = -> Sketch027 [N_Axis]
  Refine = true
  Suppressed = false
  Type = 0
FEATURE [PartDesign::Pocket] Pocket008  label="FM_Pocket008"
  BaseFeature = -> Pocket007
  Direction = (0,0,-1)
  Length = 5
  Length2 = 5
  Placement = pos=(0,0,0) rot=(1,1,1;2.0944rad)
  Profile = -> Sketch021
  ReferenceAxis = -> Sketch021 [N_Axis]
  Refine = true
  Reversed = true
  Suppressed = false
  Type = 1
FEATURE [PartDesign::Hole] Hole  label="FM_Hole000"
  BaseFeature = -> Pocket008
  CustomThreadClearance = 0
  Depth = 3.2
  DepthType = 0
  Diameter = 5.6
  DrillForDepth = false
  DrillPoint = 0
  DrillPointAngle = 118
  HoleCutCountersinkAngle = 90
  HoleCutCustomValues = false
  HoleCutDepth = 0
  HoleCutDiameter = 6
  HoleCutType = 2
  ModelThread = false
  Placement = pos=(0,0,0) rot=(1,1,1;2.0944rad)
  Profile = -> Sketch021
  Refine = true
  Reversed = true
  Suppressed = false
  Tapered = false
  TaperedAngle = 90
  ThreadClass = 0
  ThreadDepth = 3.2
  ThreadDepthType = 0
  ThreadDirection = 0
  ThreadFit = 0
  ThreadSize = 0
  ThreadType = 0
  Threaded = false
  UseCustomThreadClearance = false
FEATURE [Sketcher::SketchObject] Sketch029  label="F1_Sketch029"
  ArcFitTolerance = 1e-06
  AttachmentSupport = -> [YZ_Plane012]
  FullyConstrained = true
  MakeInternals = false
  MapMode = 5
  Placement = pos=(0,0,0) rot=(0.57735,0.57735,0.57735;2.0944rad)
  sketch-geometry (36):
    g0: Circle CenterX=0 CenterY=-44.8 CenterZ=0 NormalX=0 NormalY=0 NormalZ=1 AngleXU=0 Radius=1.6
    g1: Circle CenterX=-42.6073 CenterY=-13.844 CenterZ=0 NormalX=0 NormalY=0 NormalZ=1 AngleXU=0 Radius=1.6
    g2: Circle CenterX=26.3328 CenterY=36.244 CenterZ=0 NormalX=0 NormalY=0 NormalZ=1 AngleXU=0 Radius=1.6
    g3: Circle CenterX=42.6073 CenterY=-13.844 CenterZ=0 NormalX=0 NormalY=0 NormalZ=1 AngleXU=0 Radius=1.6
    g4: ArcOfCircle CenterX=-42.6073 CenterY=-13.844 CenterZ=0 NormalX=0 NormalY=0 NormalZ=1 AngleXU=0 Radius=4.8 StartAngle=5.02655 EndAngle=8.16814
    g5: ArcOfCircle CenterX=26.3328 CenterY=36.244 CenterZ=0 NormalX=0 NormalY=0 NormalZ=1 AngleXU=0 Radius=4.8 StartAngle=2.51327 EndAngle=5.65487
    g6: ArcOfCircle CenterX=42.6073 CenterY=-13.844 CenterZ=0 NormalX=0 NormalY=0 NormalZ=1 AngleXU=0 Radius=4.8 StartAngle=1.25664 EndAngle=4.39823
    g7: ArcOfCircle CenterX=0 CenterY=-44.8 CenterZ=0 NormalX=0 NormalY=0 NormalZ=1 AngleXU=0 Radius=4.8 StartAngle=4e-16 EndAngle=3.14159
    g8: ArcOfCircle CenterX=0 CenterY=0 CenterZ=0 NormalX=0 NormalY=0 NormalZ=1 AngleXU=0 Radius=46.4 StartAngle=0.838844 EndAngle=1.04611
    g9: ArcOfCircle CenterX=0 CenterY=0 CenterZ=0 NormalX=0 NormalY=0 NormalZ=1 AngleXU=0 Radius=46.4 StartAngle=5.86539 EndAngle=6.07266
    g10: ArcOfCircle CenterX=0 CenterY=0 CenterZ=0 NormalX=0 NormalY=0 NormalZ=1 AngleXU=0 Radius=46.4 StartAngle=4.60876 EndAngle=4.81602
    g11: ArcOfCircle CenterX=0 CenterY=0 CenterZ=0 NormalX=0 NormalY=0 NormalZ=1 AngleXU=0 Radius=46.4 StartAngle=3.35212 EndAngle=3.55939
    g12: LineSegment StartX=-45.3755 StartY=-9.69639 StartZ=0 EndX=-44.0906 EndY=-9.27889 EndZ=0
    g13: LineSegment StartX=-42.409 StartY=-18.8265 StartZ=0 EndX=-41.1241 EndY=-18.409 EndZ=0
    g14: LineSegment StartX=23.2436 StartY=40.1584 StartZ=0 EndX=22.4495 EndY=39.0653 EndZ=0
    g15: LineSegment StartX=31.0102 StartY=34.5156 StartZ=0 EndX=30.2161 EndY=33.4226 EndZ=0
    g16: LineSegment StartX=45.3755 StartY=-9.69639 StartZ=0 EndX=44.0906 EndY=-9.27889 EndZ=0
    g17: LineSegment StartX=42.409 StartY=-18.8265 StartZ=0 EndX=41.1241 EndY=-18.409 EndZ=0
    g18: LineSegment StartX=4.8 StartY=-46.1511 StartZ=0 EndX=4.8 EndY=-44.8 EndZ=0
    g19: LineSegment StartX=-4.8 StartY=-46.1511 StartZ=0 EndX=-4.8 EndY=-44.8 EndZ=0
    g20: LineSegment [constr] StartX=0 StartY=-44.8 StartZ=0 EndX=42.6073 EndY=-13.844 EndZ=0
    g21: LineSegment [constr] StartX=42.6073 StartY=-13.844 StartZ=0 EndX=26.3328 EndY=36.244 EndZ=0
    g22: LineSegment [constr] StartX=26.3328 StartY=36.244 StartZ=0 EndX=-26.3328 EndY=36.244 EndZ=0
    g23: LineSegment [constr] StartX=-26.3328 StartY=36.244 StartZ=0 EndX=-42.6073 EndY=-13.844 EndZ=0
    g24: LineSegment [constr] StartX=-42.6073 StartY=-13.844 StartZ=0 EndX=0 EndY=-44.8 EndZ=0
    g25: Circle [constr] CenterX=0 CenterY=0 CenterZ=0 NormalX=0 NormalY=0 NormalZ=1 AngleXU=0 Radius=44.8
    g26: LineSegment [constr] StartX=0 StartY=-44.8 StartZ=0 EndX=0 EndY=-46.4 EndZ=0
    g27: LineSegment [constr] StartX=42.6073 StartY=-13.844 StartZ=0 EndX=0 EndY=0 EndZ=0
    g28: LineSegment [constr] StartX=26.3328 StartY=36.244 StartZ=0 EndX=0 EndY=0 EndZ=0
    g29: LineSegment [constr] StartX=0 StartY=0 StartZ=0 EndX=-26.3328 EndY=36.244 EndZ=0
    g30: LineSegment [constr] StartX=0 StartY=0 StartZ=0 EndX=-42.6073 EndY=-13.844 EndZ=0
    g31: ArcOfCircle CenterX=0 CenterY=0 CenterZ=0 NormalX=0 NormalY=0 NormalZ=1 AngleXU=0 Radius=46.4 StartAngle=2.09548 EndAngle=2.30275
    g32: ArcOfCircle CenterX=-26.3328 CenterY=36.244 CenterZ=0 NormalX=0 NormalY=0 NormalZ=1 AngleXU=0 Radius=4.8 StartAngle=3.76991 EndAngle=6.9115
    g33: LineSegment StartX=-31.0102 StartY=34.5156 StartZ=0 EndX=-30.2161 EndY=33.4226 EndZ=0
    g34: LineSegment StartX=-23.2436 StartY=40.1584 StartZ=0 EndX=-22.4495 EndY=39.0653 EndZ=0
    g35: Circle CenterX=-26.3328 CenterY=36.244 CenterZ=0 NormalX=0 NormalY=0 NormalZ=1 AngleXU=0 Radius=1.6
  constraints (85):
    c: Equal(g2,g1)
    c: Equal(g1,g0)
    c: Equal(g0,g3)
    c: Diameter(g1) = 3.2
    c: Coincident(g4,g1)
    c: Coincident(g5,g2)
    c: Coincident(g6,g3)
    c: Coincident(g7,g0)
    c: Coincident(g12,g11)
    c: Coincident(g13,g11)
    c: Coincident(g14,g8)
    c: Coincident(g15,g8)
    c: Coincident(g16,g9)
    c: Coincident(g17,g9)
    c: Coincident(g18,g10)
    c: Vertical(g18)
    c: Coincident(g19,g10)
    c: Vertical(g19)
    c: Equal(g10,g-3)
    c: Equal(g-3,g9)
    c: Equal(g-3,g8)
    c: Equal(g-3,g11)
    c: Equal(g4,g5)
    c: Equal(g5,g6)
    c: Equal(g6,g7)
    c: Radius(g7) = 4.8
    c: Tangent(g4,g12) = 1.5708
    c: Tangent(g4,g13) = -1.5708
    c: Tangent(g19,g7) = 1.5708
    c: Tangent(g18,g7) = -1.5708
    c: Tangent(g17,g6) = 1.5708
    c: Tangent(g16,g6) = -1.5708
    c: Tangent(g5,g15) = 1.5708
    c: Tangent(g5,g14) = -1.5708
    c: Coincident(g20,g21)
    c: Coincident(g21,g22)
    c: Coincident(g22,g23)
    c: Coincident(g23,g24)
    c: Coincident(g24,g20)
    c: Equal(g20, g21-g24) x4
    c: PointOnObject(g20,g25)
    c: PointOnObject(g21,g25)
    c: PointOnObject(g22,g25)
    c: PointOnObject(g23,g25)
    c: PointOnObject(g24,g25)
    c: Coincident(g25,g8)
    c: PointOnObject(g24,g-2)
    c: Coincident(g26,g20)
    c: PointOnObject(g26,g-3)
    c: Vertical(g26)
    c: DistanceY(g26,g26) = 1.6
    c: Coincident(g0,g20)
    c: Coincident(g8,g10)
    c: Coincident(g8,g9)
    c: Coincident(g8,g11)
    c: Coincident(g8,g-1)
    c: Coincident(g27,g20)
    c: Coincident(g27,g8)
    c: Coincident(g28,g21)
    c: Coincident(g28,g8)
    c: Coincident(g29,g8)
    c: Coincident(g29,g22)
    c: Coincident(g30,g8)
    c: Coincident(g30,g23)
    c: Parallel(g17,g16)
    c: Parallel(g16,g27)
    c: Coincident(g3,g20)
    c: Parallel(g15,g14)
    c: Parallel(g14,g28)
    c: Coincident(g2,g21)
    c: Parallel(g13,g30)
    c: Parallel(g30,g12)
    c: Coincident(g1,g23)
    c: Coincident(g31,g8)
    c: Coincident(g32,g22)
    c: Coincident(g33,g31)
    c: Coincident(g34,g31)
    c: Parallel(g34,g33)
    c: Parallel(g33,g29)
    c: Tangent(g32,g33) = -1.5708
    c: Tangent(g32,g34) = 1.5708
    c: Equal(g-3,g31)
    c: Equal(g32,g4)
    c: Coincident(g35,g22)
    c: Equal(g35,g3)
FEATURE [PartDesign::Pad] Pad016  label="F1_Pad016"
  BaseFeature = -> Revolution002
  Direction = (1,0,0)
  Length = 8.54
  Length2 = 14.7
  Placement = pos=(0,0,0) rot=(1,0,0;1.5708rad)
  Profile = -> Sketch029
  ReferenceAxis = -> Sketch029 [N_Axis]
  Refine = true
  Suppressed = false
  Type = 4
FEATURE [Sketcher::SketchObject] Sketch030  label="F1_Sketch030"
  ArcFitTolerance = 1e-06
  AttachmentOffset = pos=(0,0,8.54) rot=(0,0,1;0rad)
  AttachmentSupport = -> [YZ_Plane012]
  FullyConstrained = true
  MakeInternals = false
  MapMode = 5
  Placement = pos=(8.54,0,0) rot=(0.57735,0.57735,0.57735;2.0944rad)
  expr: .AttachmentOffset.Base.z = <<F1_Pad016>>.Length
  sketch-geometry (39):
    g0: LineSegment StartX=-40.4439 StartY=-11.4413 StartZ=0 EndX=-43.6064 EndY=-10.769 EndZ=0
    g1: LineSegment StartX=-43.6064 StartY=-10.769 StartZ=0 EndX=-45.7698 EndY=-13.1717 EndZ=0
    g2: LineSegment StartX=-45.7698 StartY=-13.1717 StartZ=0 EndX=-44.7707 EndY=-16.2467 EndZ=0
    g3: LineSegment StartX=-44.7707 StartY=-16.2467 StartZ=0 EndX=-41.6082 EndY=-16.9189 EndZ=0
    g4: LineSegment StartX=-41.6082 StartY=-16.9189 StartZ=0 EndX=-39.4448 EndY=-14.5162 EndZ=0
    g5: LineSegment StartX=-39.4448 StartY=-14.5162 StartZ=0 EndX=-40.4439 EndY=-11.4413 EndZ=0
    g6: Circle [constr] CenterX=-42.6073 CenterY=-13.844 CenterZ=0 NormalX=0 NormalY=0 NormalZ=1 AngleXU=0 Radius=3.23316
    g7: LineSegment StartX=45.7698 StartY=-13.1717 StartZ=0 EndX=43.6064 EndY=-10.769 EndZ=0
    g8: LineSegment StartX=43.6064 StartY=-10.769 StartZ=0 EndX=40.4439 EndY=-11.4413 EndZ=0
    g9: LineSegment StartX=40.4439 StartY=-11.4413 StartZ=0 EndX=39.4448 EndY=-14.5162 EndZ=0
    g10: LineSegment StartX=39.4448 StartY=-14.5162 StartZ=0 EndX=41.6082 EndY=-16.9189 EndZ=0
    g11: LineSegment StartX=41.6082 StartY=-16.9189 StartZ=0 EndX=44.7707 EndY=-16.2467 EndZ=0
    g12: LineSegment StartX=44.7707 StartY=-16.2467 StartZ=0 EndX=45.7698 EndY=-13.1717 EndZ=0
    g13: Circle [constr] CenterX=42.6073 CenterY=-13.844 CenterZ=0 NormalX=0 NormalY=0 NormalZ=1 AngleXU=0 Radius=3.23316
    g14: LineSegment StartX=-1.61658 StartY=-42 StartZ=0 EndX=-3.23316 EndY=-44.8 EndZ=0
    g15: LineSegment StartX=-3.23316 StartY=-44.8 StartZ=0 EndX=-1.61658 EndY=-47.6 EndZ=0
    g16: LineSegment StartX=-1.61658 StartY=-47.6 StartZ=0 EndX=1.61658 EndY=-47.6 EndZ=0
    g17: LineSegment StartX=1.61658 StartY=-47.6 StartZ=0 EndX=3.23316 EndY=-44.8 EndZ=0
    g18: LineSegment StartX=3.23316 StartY=-44.8 StartZ=0 EndX=1.61658 EndY=-42 EndZ=0
    g19: LineSegment StartX=1.61658 StartY=-42 StartZ=0 EndX=-1.61658 EndY=-42 EndZ=0
    g20: Circle [constr] CenterX=0 CenterY=-44.8 CenterZ=0 NormalX=0 NormalY=0 NormalZ=1 AngleXU=0 Radius=3.23316
    g21: LineSegment StartX=23.3791 StartY=34.9289 StartZ=0 EndX=25.9948 EndY=33.0285 EndZ=0
    g22: LineSegment StartX=25.9948 StartY=33.0285 StartZ=0 EndX=28.9485 EndY=34.3436 EndZ=0
    g23: LineSegment StartX=28.9485 StartY=34.3436 StartZ=0 EndX=29.2864 EndY=37.559 EndZ=0
    g24: LineSegment StartX=29.2864 StartY=37.559 StartZ=0 EndX=26.6707 EndY=39.4594 EndZ=0
    g25: LineSegment StartX=26.6707 StartY=39.4594 StartZ=0 EndX=23.7171 EndY=38.1444 EndZ=0
    g26: LineSegment StartX=23.7171 StartY=38.1444 StartZ=0 EndX=23.3791 EndY=34.9289 EndZ=0
    g27: Circle [constr] CenterX=26.3328 CenterY=36.244 CenterZ=0 NormalX=0 NormalY=0 NormalZ=1 AngleXU=0 Radius=3.23316
    g28: LineSegment StartX=-28.9485 StartY=34.3436 StartZ=0 EndX=-25.9948 EndY=33.0285 EndZ=0
    g29: LineSegment StartX=-25.9948 StartY=33.0285 StartZ=0 EndX=-23.3791 EndY=34.9289 EndZ=0
    g30: LineSegment StartX=-23.3791 StartY=34.9289 StartZ=0 EndX=-23.7171 EndY=38.1444 EndZ=0
    g31: LineSegment StartX=-23.7171 StartY=38.1444 StartZ=0 EndX=-26.6707 EndY=39.4594 EndZ=0
    g32: LineSegment StartX=-26.6707 StartY=39.4594 StartZ=0 EndX=-29.2864 EndY=37.559 EndZ=0
    g33: LineSegment StartX=-29.2864 StartY=37.559 StartZ=0 EndX=-28.9485 EndY=34.3436 EndZ=0
    g34: Circle [constr] CenterX=-26.3328 CenterY=36.244 CenterZ=0 NormalX=0 NormalY=0 NormalZ=1 AngleXU=0 Radius=3.23316
    g35: LineSegment [constr] StartX=-26.3328 StartY=36.244 StartZ=0 EndX=0 EndY=0 EndZ=0
    g36: LineSegment [constr] StartX=0 StartY=-1.8e-15 StartZ=0 EndX=-42.6073 EndY=-13.844 EndZ=0
    g37: LineSegment [constr] StartX=42.6073 StartY=-13.844 StartZ=0 EndX=0 EndY=-1.8e-15 EndZ=0
    g38: LineSegment [constr] StartX=26.3328 StartY=36.244 StartZ=0 EndX=0 EndY=0 EndZ=0
  constraints (88):
    c: Coincident(g0,g1)
    c: Coincident(g1,g2)
    c: Coincident(g2,g3)
    c: Coincident(g3,g4)
    c: Coincident(g4,g5)
    c: Coincident(g5,g0)
    c: Equal(g0, g1-g5) x5
    c: PointOnObject(g0,g6)
    c: PointOnObject(g1,g6)
    c: PointOnObject(g2,g6)
    c: PointOnObject(g3,g6)
    c: PointOnObject(g4,g6)
    c: PointOnObject(g5,g6)
    c: Coincident(g7,g8)
    c: Coincident(g8,g9)
    c: Coincident(g9,g10)
    c: Coincident(g10,g11)
    c: Coincident(g11,g12)
    c: Coincident(g12,g7)
    c: Equal(g7, g8-g12) x5
    c: PointOnObject(g7,g13)
    c: PointOnObject(g8,g13)
    c: PointOnObject(g9,g13)
    c: PointOnObject(g10,g13)
    c: PointOnObject(g11,g13)
    c: PointOnObject(g12,g13)
    c: Coincident(g14,g15)
    c: Coincident(g15,g16)
    c: Coincident(g16,g17)
    c: Coincident(g17,g18)
    c: Coincident(g18,g19)
    c: Coincident(g19,g14)
    c: Equal(g14, g15-g19) x5
    c: PointOnObject(g14,g20)
    c: PointOnObject(g15,g20)
    c: PointOnObject(g16,g20)
    c: PointOnObject(g17,g20)
    c: PointOnObject(g18,g20)
    c: PointOnObject(g19,g20)
    c: Equal(g13,g6)
    c: Coincident(g20,g-4)
    c: Coincident(g21,g22)
    c: Coincident(g22,g23)
    c: Coincident(g23,g24)
    c: Coincident(g24,g25)
    c: Coincident(g25,g26)
    c: Coincident(g26,g21)
    c: Equal(g21, g22-g26) x5
    c: PointOnObject(g21,g27)
    c: PointOnObject(g22,g27)
    c: PointOnObject(g23,g27)
    c: PointOnObject(g24,g27)
    c: PointOnObject(g25,g27)
    c: PointOnObject(g26,g27)
    c: Coincident(g27,g-3)
    c: Coincident(g28,g29)
    c: Coincident(g29,g30)
    c: Coincident(g30,g31)
    c: Coincident(g31,g32)
    c: Coincident(g32,g33)
    c: Coincident(g33,g28)
    c: Equal(g28, g29-g33) x5
    c: PointOnObject(g28,g34)
    c: PointOnObject(g29,g34)
    c: PointOnObject(g30,g34)
    c: PointOnObject(g31,g34)
    c: PointOnObject(g32,g34)
    c: PointOnObject(g33,g34)
    c: Coincident(g34,g-5)
    c: Equal(g34,g27)
    c: Equal(g27,g6)
    c: Coincident(g35,g34)
    c: Coincident(g35,g-1)
    c: Coincident(g36,g35)
    c: Coincident(g36,g6)
    c: Coincident(g37,g13)
    c: Coincident(g37,g35)
    c: Coincident(g38,g27)
    c: Coincident(g38,g35)
    c: Perpendicular(g24,g38)
    c: Perpendicular(g37,g12)
    c: Coincident(g13,g-6)
    c: Coincident(g6,g-7)
    c: Perpendicular(g36,g2)
    c: Equal(g20,g6)
    c: Perpendicular(g35,g32)
    c: Horizontal(g16)
    c: DistanceY(g15,g14) = 5.6
FEATURE [Part::Cylinder] Cylinder  label="F1_Div"
  Angle = 360
  AttacherType = Attacher::AttachEngine3D
  FirstAngle = 0
  Height = 4.2
  Placement = pos=(4.5,0,0) rot=(0,1,0;1.5708rad)
  Radius = 51
  SecondAngle = 0
  expr: .Placement.Base.x = dd.B1_PL - Height - 1.3 mm
  expr: Height = 4.2
FEATURE [PartDesign::SubShapeBinder] Binder005  label="G1_Binder005"
  BindCopyOnChange = 0
  BindMode = 0
  ClaimChildren = false
  Context = -> Part002 [Body014.Binder005.]
  Fuse = false
  MakeFace = true
  OffsetFill = false
  OffsetIntersection = false
  OffsetJoinType = 0
  OffsetOpenResult = false
  PartialLoad = false
  Refine = true
  Relative = true
  Support = -> [BevelGear001[Face145],Part[Body003.Face80]]
  _Version = 2
FEATURE [Sketcher::SketchObject] Sketch031  label="G1_Sketch031"
  ArcFitTolerance = 1e-06
  AttachmentSupport = -> [XZ_Plane014]
  ExternalGeometry = -> [Binder005]
  FullyConstrained = true
  MakeInternals = false
  MapMode = 5
  Placement = pos=(0,0,0) rot=(1,0,0;1.5708rad)
  sketch-geometry (5):
    g0: LineSegment StartX=-16.2823 StartY=16 StartZ=0 EndX=0 EndY=16 EndZ=0
    g1: LineSegment StartX=0 StartY=16 StartZ=0 EndX=1.2e-15 EndY=36 EndZ=0
    g2: LineSegment StartX=1.2e-15 StartY=36 StartZ=0 EndX=-16.5 EndY=36 EndZ=0
    g3: LineSegment StartX=-16.5 StartY=36 StartZ=0 EndX=-16.5 EndY=16.8125 EndZ=0
    g4: LineSegment StartX=-16.5 StartY=16.8125 StartZ=0 EndX=-16.2823 EndY=16 EndZ=0
  constraints (12):
    c: PointOnObject(g0,g-2)
    c: Horizontal(g0)
    c: Coincident(g0,g1)
    c: Symmetric(g-3,g-3,g1)
    c: Coincident(g1,g2)
    c: Coincident(g2,g-3)
    c: Coincident(g2,g3)
    c: Coincident(g3,g4)
    c: Vertical(g3)
    c: Angle(g0,g4) = 1.8326
    c: Coincident(g0,g4)
    c: Coincident(g0,g-4)
FEATURE [PartDesign::Revolution] Revolution003  label="G1_Revolution003"
  Angle = 360
  Angle2 = 60
  Axis = (0,2e-16,1)
  Base = (0,0,0)
  Placement = pos=(0,0,0) rot=(1,0,0;1.5708rad)
  Profile = -> Sketch031
  ReferenceAxis = -> Sketch031 [V_Axis]
  Refine = true
  Suppressed = false
  Type = 0
FEATURE [PartDesign::Body] Body014  label="G1_Add"
  AllowCompound = false
  Group = -> [Binder005,Sketch031,Revolution003]
  Origin = -> Origin014
  Tip = -> Revolution003
FEATURE [Part::MultiFuse] Fusion001  label="G1_Fusion001"
  Refine = true
  Shapes = -> [BevelGear001,Body014]
FEATURE [PartDesign::SubShapeBinder] Binder006  label="G1_Binder006"
  BindCopyOnChange = 0
  BindMode = 0
  ClaimChildren = false
  Context = -> Part002 [Body015.Binder006.]
  Fuse = false
  MakeFace = true
  OffsetFill = false
  OffsetIntersection = false
  OffsetJoinType = 0
  OffsetOpenResult = false
  PartialLoad = false
  Refine = true
  Relative = true
  Support = -> [Part[Body003.Face80]]
  _Version = 2
FEATURE [Sketcher::SketchObject] Sketch032  label="G1_Sketch032"
  ArcFitTolerance = 1e-06
  AttachmentSupport = -> [XZ_Plane015]
  ExternalGeometry = -> [Binder006]
  FullyConstrained = true
  MakeInternals = false
  MapMode = 5
  Placement = pos=(0,0,0) rot=(1,0,0;1.5708rad)
  expr: Constraints[10] = dd.G1_Num * dd.G1_Module / 2
  sketch-geometry (4):
    g0: LineSegment StartX=0 StartY=0 StartZ=0 EndX=24 EndY=0 EndZ=0
    g1: LineSegment StartX=24 StartY=0 StartZ=0 EndX=24 EndY=36 EndZ=0
    g2: LineSegment StartX=24 StartY=36 StartZ=0 EndX=0 EndY=36 EndZ=0
    g3: LineSegment StartX=0 StartY=36 StartZ=0 EndX=0 EndY=0 EndZ=0
  constraints (11):
    c: Coincident(g0,g1)
    c: Coincident(g1,g2)
    c: Coincident(g2,g3)
    c: Coincident(g3,g0)
    c: Horizontal(g0)
    c: Horizontal(g2)
    c: Vertical(g1)
    c: Vertical(g3)
    c: Coincident(g0,g-1)
    c: PointOnObject(g-3,g2)
    c: DistanceX(g0,g0) = 24
FEATURE [PartDesign::Revolution] Revolution004  label="G1_Revolution004"
  Angle = 360
  Angle2 = 60
  Axis = (0,2e-16,1)
  Base = (0,0,0)
  Placement = pos=(0,0,0) rot=(1,0,0;1.5708rad)
  Profile = -> Sketch032
  ReferenceAxis = -> Sketch032 [V_Axis]
  Refine = true
  Reversed = true
  Suppressed = false
  Type = 0
FEATURE [Sketcher::SketchObject] Sketch033  label="G1_Sketch033"
  ArcFitTolerance = 1e-06
  AttachmentSupport = -> [XY_Plane015]
  ExternalGeometry = -> [Binder006]
  FullyConstrained = true
  MakeInternals = false
  MapMode = 5
  sketch-geometry (6):
    g0: Circle CenterX=-9e-16 CenterY=12 CenterZ=0 NormalX=0 NormalY=0 NormalZ=1 AngleXU=0 Radius=2.1
    g1: Circle CenterX=10.3923 CenterY=6 CenterZ=0 NormalX=0 NormalY=0 NormalZ=1 AngleXU=0 Radius=2.1
    g2: Circle CenterX=10.3923 CenterY=-6 CenterZ=0 NormalX=0 NormalY=0 NormalZ=1 AngleXU=0 Radius=2.1
    g3: Circle CenterX=0 CenterY=-12 CenterZ=0 NormalX=0 NormalY=0 NormalZ=1 AngleXU=0 Radius=2.1
    g4: Circle CenterX=-10.3923 CenterY=-6 CenterZ=0 NormalX=0 NormalY=0 NormalZ=1 AngleXU=0 Radius=2.1
    g5: Circle CenterX=-10.3923 CenterY=6 CenterZ=0 NormalX=0 NormalY=0 NormalZ=1 AngleXU=0 Radius=2.1
  constraints (12):
    c: Coincident(g0,g-4)
    c: Coincident(g1,g-5)
    c: Coincident(g2,g-6)
    c: Coincident(g3,g-7)
    c: Coincident(g4,g-8)
    c: Coincident(g5,g-3)
    c: Equal(g1,g0)
    c: Equal(g0,g2)
    c: Equal(g2,g3)
    c: Equal(g3,g4)
    c: Equal(g4,g5)
    c: Diameter(g2) = 4.2
FEATURE [PartDesign::Hole] Hole003  label="G1_Hole003"
  BaseFeature = -> Revolution004
  CustomThreadClearance = 0
  Depth = 155.194
  DepthType = 1
  Diameter = 4.2
  DrillForDepth = false
  DrillPoint = 1
  DrillPointAngle = 118
  HoleCutCountersinkAngle = 90
  HoleCutCustomValues = false
  HoleCutDepth = 0
  HoleCutDiameter = 7.4
  HoleCutType = 2
  ModelThread = false
  Placement = pos=(0,0,0) rot=(1,0,0;1.5708rad)
  Profile = -> Sketch033
  Refine = true
  Reversed = true
  Suppressed = false
  Tapered = false
  TaperedAngle = 90
  ThreadClass = 0
  ThreadDepth = 155.194
  ThreadDepthType = 0
  ThreadDirection = 0
  ThreadFit = 0
  ThreadSize = 0
  ThreadType = 0
  Threaded = false
  UseCustomThreadClearance = false
FEATURE [PartDesign::Body] Body015  label="G1_Comm"
  AllowCompound = false
  Group = -> [Binder006,Sketch032,Revolution004,Sketch033,Hole003]
  Origin = -> Origin015
  Tip = -> Hole003
FEATURE [Part::MultiCommon] Common001  label="G1_Common001"
  Refine = true
  Shapes = -> [Fusion001,Body015]
FEATURE [App::Part] Part002  label="G1"
  Group = -> [Body015,BevelGear001,Fusion001,Body014,Common001]
  Origin = -> Origin008
  Placement = pos=(0,0,-64) rot=(1,0,0;0rad)
  expr: .Placement.Base.z = -dd.G2_Num * dd.G1_Module / 2
FEATURE [Sketcher::SketchObject] Sketch034  label="CL0_Sketch010"
  ArcFitTolerance = 1e-06
  AttachmentOffset = pos=(0,0,8.7) rot=(0,0,1;0rad)
  AttachmentSupport = -> [YZ_Plane016]
  FullyConstrained = true
  MakeInternals = false
  MapMode = 5
  Placement = pos=(8.7,0,0) rot=(0.57735,0.57735,0.57735;2.0944rad)
  expr: .AttachmentOffset.Base.z = dd.CL_BW / 2
  expr: Constraints[16] = dd.CL_Radius
  expr: Constraints[17] = dd.CL_Radius
  expr: Constraints[18] = dd.CD_Radius
  expr: Constraints[2] = dd.CL_Len
  expr: Constraints[4] = dd.CL_BD
  sketch-geometry (8):
    g0: Circle CenterX=0 CenterY=0 CenterZ=0 NormalX=0 NormalY=0 NormalZ=1 AngleXU=0 Radius=2.45
    g1: Circle CenterX=0 CenterY=-18.2 CenterZ=0 NormalX=0 NormalY=0 NormalZ=1 AngleXU=0 Radius=2.45
    g2: ArcOfCircle CenterX=72.6064 CenterY=-9.1 CenterZ=0 NormalX=0 NormalY=0 NormalZ=1 AngleXU=0 Radius=80.0436 StartAngle=2.95181 EndAngle=3.33138
    g3: ArcOfCircle CenterX=0 CenterY=0 CenterZ=0 NormalX=0 NormalY=0 NormalZ=1 AngleXU=0 Radius=6 StartAngle=1e-16 EndAngle=1.5708
    g4: ArcOfCircle CenterX=0 CenterY=-18.2 CenterZ=0 NormalX=0 NormalY=0 NormalZ=1 AngleXU=0 Radius=6 StartAngle=4.71239 EndAngle=6.28319
    g5: LineSegment StartX=-6 StartY=-24.2 StartZ=0 EndX=-9e-16 EndY=-24.2 EndZ=0
    g6: LineSegment StartX=-6 StartY=6 StartZ=0 EndX=0 EndY=6 EndZ=0
    g7: LineSegment StartX=6 StartY=6e-16 StartZ=0 EndX=6 EndY=-18.2 EndZ=0
  constraints (20):
    c: Coincident(g0,g-1)
    c: PointOnObject(g1,g-2)
    c: DistanceY(g1,g0) = 18.2
    c: Equal(g1,g0)
    c: Diameter(g1) = 4.9
    c: Coincident(g3,g0)
    c: Coincident(g4,g1)
    c: Coincident(g5,g2)
    c: Horizontal(g5)
    c: Coincident(g6,g2)
    c: Horizontal(g6)
    c: Vertical(g7)
    c: Tangent(g6,g3) = 1.5708
    c: Tangent(g3,g7) = 1.5708
    c: Tangent(g7,g4) = 1.5708
    c: Tangent(g4,g5) = -1.5708
    c: Radius(g3) = 6
    c: DistanceX(g6,g6) = 6
    c: Distance(g2,g-2) = 72.6064
    c: Equal(g5,g6)
FEATURE [PartDesign::Pad] Pad017  label="CL0_Pad017"
  Direction = (1,0,0)
  Length = 1.6
  Length2 = 10
  Placement = pos=(0,0,0) rot=(1,1,1;2.0944rad)
  Profile = -> Sketch034
  ReferenceAxis = -> Sketch034 [N_Axis]
  Refine = true
  Reversed = true
  Suppressed = false
  Type = 0
  expr: Length = <<CL3_Pad005>>.Length
FEATURE [Sketcher::SketchObject] Sketch035  label="CL0_Sketch011"
  ArcFitTolerance = 1e-06
  AttachmentOffset = pos=(0,0,8.7) rot=(0,0,1;0rad)
  AttachmentSupport = -> [YZ_Plane016]
  ExternalGeometry = -> [Pad017]
  FullyConstrained = true
  MakeInternals = false
  MapMode = 5
  Placement = pos=(8.7,0,0) rot=(0.57735,0.57735,0.57735;2.0944rad)
  expr: .AttachmentOffset.Base.z = dd.CL_BW / 2
  expr: Constraints[14] = 360 / dd.CL_Num
  expr: Constraints[18] = dd.CL_BD + 0.3 mm
  expr: Constraints[5] = dd.CL_Radius
  sketch-geometry (8):
    g0: ArcOfCircle CenterX=-4e-15 CenterY=-18.2 CenterZ=0 NormalX=0 NormalY=0 NormalZ=1 AngleXU=0 Radius=6 StartAngle=0.251327 EndAngle=1.5708
    g1: ArcOfCircle CenterX=72.6064 CenterY=-9.1 CenterZ=0 NormalX=0 NormalY=0 NormalZ=1 AngleXU=0 Radius=80.0436 StartAngle=2.95181 EndAngle=3.18033
    g2: LineSegment StartX=-7.37714 StartY=-12.2 StartZ=0 EndX=-5.3e-15 EndY=-12.2 EndZ=0
    g3: LineSegment StartX=6 StartY=0 StartZ=0 EndX=6 EndY=-17.442 EndZ=0
    g4: LineSegment StartX=6 StartY=-17.442 StartZ=0 EndX=5.8115 EndY=-16.7079 EndZ=0
    g5: LineSegment StartX=-6 StartY=6 StartZ=0 EndX=-9e-16 EndY=6 EndZ=0
    g6: ArcOfCircle CenterX=0 CenterY=0 CenterZ=0 NormalX=0 NormalY=0 NormalZ=1 AngleXU=0 Radius=6 StartAngle=0 EndAngle=1.5708
    g7: Circle CenterX=0 CenterY=0 CenterZ=0 NormalX=0 NormalY=0 NormalZ=1 AngleXU=0 Radius=2.6
  constraints (19):
    c: Coincident(g2,g1)
    c: Horizontal(g2)
    c: Tangent(g0,g2) = 1.5708
    c: Vertical(g3)
    c: Coincident(g3,g4)
    c: Distance(g3,g-2) = 6
    c: Tangent(g0,g4) = -1.5708
    c: Coincident(g1,g-3)
    c: Horizontal(g5)
    c: Coincident(g1,g5)
    c: Equal(g-3,g1)
    c: Coincident(g6,g-1)
    c: Tangent(g3,g6) = 1.5708
    c: Tangent(g6,g5) = 1.5708
    c: Angle(g3,g4) = 0.251327
    c: Equal(g0,g6)
    c: Coincident(g-4,g0)
    c: Coincident(g7,g6)
    c: Diameter(g7) = 5.2
FEATURE [PartDesign::Pad] Pad018  label="CL0_Pad018"
  BaseFeature = -> Pad017
  Direction = (1,0,0)
  Length = 6
  Length2 = 10
  Placement = pos=(0,0,0) rot=(1,1,1;2.0944rad)
  Profile = -> Sketch035
  ReferenceAxis = -> Sketch035 [N_Axis]
  Refine = true
  Suppressed = false
  Type = 0
  expr: Length = <<CL3_Pad006>>.Length
FEATURE [Sketcher::SketchObject] Sketch037  label="CL0_Sketch013"
  ArcFitTolerance = 1e-06
  AttachmentOffset = pos=(0,0,-8.7) rot=(0,0,1;0rad)
  AttachmentSupport = -> [YZ_Plane006]
  FullyConstrained = true
  MakeInternals = false
  MapMode = 5
  Placement = pos=(-8.7,0,0) rot=(0.57735,0.57735,0.57735;2.0944rad)
  expr: .AttachmentOffset.Base.z = -dd.CL_BW / 2
  expr: Constraints[16] = dd.CL_Radius
  expr: Constraints[17] = dd.CL_Radius
  expr: Constraints[18] = dd.CD_Radius
  expr: Constraints[2] = dd.CL_Len
  expr: Constraints[4] = dd.CL_BD
  sketch-geometry (8):
    g0: Circle CenterX=0 CenterY=0 CenterZ=0 NormalX=0 NormalY=0 NormalZ=1 AngleXU=0 Radius=2.45
    g1: Circle CenterX=0 CenterY=-18.2 CenterZ=0 NormalX=0 NormalY=0 NormalZ=1 AngleXU=0 Radius=2.45
    g2: ArcOfCircle CenterX=72.6064 CenterY=-9.1 CenterZ=0 NormalX=0 NormalY=0 NormalZ=1 AngleXU=0 Radius=80.0436 StartAngle=2.95181 EndAngle=3.33138
    g3: ArcOfCircle CenterX=0 CenterY=0 CenterZ=0 NormalX=0 NormalY=0 NormalZ=1 AngleXU=0 Radius=6 StartAngle=1e-16 EndAngle=1.5708
    g4: ArcOfCircle CenterX=0 CenterY=-18.2 CenterZ=0 NormalX=0 NormalY=0 NormalZ=1 AngleXU=0 Radius=6 StartAngle=4.71239 EndAngle=6.28319
    g5: LineSegment StartX=-6 StartY=-24.2 StartZ=0 EndX=-9e-16 EndY=-24.2 EndZ=0
    g6: LineSegment StartX=-6 StartY=6 StartZ=0 EndX=0 EndY=6 EndZ=0
    g7: LineSegment StartX=6 StartY=6e-16 StartZ=0 EndX=6 EndY=-18.2 EndZ=0
  constraints (20):
    c: Coincident(g0,g-1)
    c: PointOnObject(g1,g-2)
    c: DistanceY(g1,g0) = 18.2
    c: Equal(g1,g0)
    c: Diameter(g1) = 4.9
    c: Coincident(g3,g0)
    c: Coincident(g4,g1)
    c: Coincident(g5,g2)
    c: Horizontal(g5)
    c: Coincident(g6,g2)
    c: Horizontal(g6)
    c: Vertical(g7)
    c: Tangent(g6,g3) = 1.5708
    c: Tangent(g3,g7) = 1.5708
    c: Tangent(g7,g4) = 1.5708
    c: Tangent(g4,g5) = -1.5708
    c: Radius(g3) = 6
    c: DistanceX(g6,g6) = 6
    c: Distance(g2,g-2) = 72.6064
    c: Equal(g5,g6)
FEATURE [PartDesign::Pad] Pad019  label="CL0_Pad009"
  Direction = (1,0,0)
  Length = 1.6
  Length2 = 10
  Placement = pos=(0,0,0) rot=(1,1,1;2.0944rad)
  Profile = -> Sketch037
  ReferenceAxis = -> Sketch037 [N_Axis]
  Refine = true
  Suppressed = false
  Type = 0
FEATURE [Sketcher::SketchObject] Sketch038  label="CL0_Sketch014"
  ArcFitTolerance = 1e-06
  AttachmentOffset = pos=(0,0,-8.7) rot=(0,0,1;0rad)
  AttachmentSupport = -> [YZ_Plane006]
  ExternalGeometry = -> [Pad019]
  FullyConstrained = true
  MakeInternals = false
  MapMode = 5
  Placement = pos=(-8.7,0,0) rot=(0.57735,0.57735,0.57735;2.0944rad)
  expr: .AttachmentOffset.Base.z = -dd.CL_BW / 2
  expr: Constraints[11] = 360 ° / dd.CL_Num
  expr: Constraints[16] = dd.CL_BD
  expr: Constraints[8] = dd.CL_Radius
  sketch-geometry (8):
    g0: ArcOfCircle CenterX=-4e-16 CenterY=-18.2 CenterZ=0 NormalX=0 NormalY=0 NormalZ=1 AngleXU=0 Radius=6 StartAngle=0.251327 EndAngle=1.5708
    g1: ArcOfCircle CenterX=72.6064 CenterY=-9.1 CenterZ=0 NormalX=0 NormalY=0 NormalZ=1 AngleXU=0 Radius=80.0436 StartAngle=2.95181 EndAngle=3.18033
    g2: LineSegment StartX=-6 StartY=6 StartZ=0 EndX=-9e-16 EndY=6 EndZ=0
    g3: LineSegment StartX=-7.37714 StartY=-12.2 StartZ=0 EndX=-1.8e-15 EndY=-12.2 EndZ=0
    g4: LineSegment StartX=6 StartY=0 StartZ=0 EndX=6 EndY=-17.442 EndZ=0
    g5: LineSegment StartX=6 StartY=-17.442 StartZ=0 EndX=5.8115 EndY=-16.7079 EndZ=0
    g6: ArcOfCircle CenterX=0 CenterY=0 CenterZ=0 NormalX=0 NormalY=0 NormalZ=1 AngleXU=0 Radius=6 StartAngle=0 EndAngle=1.5708
    g7: Circle CenterX=0 CenterY=0 CenterZ=0 NormalX=0 NormalY=0 NormalZ=1 AngleXU=0 Radius=2.45
  constraints (19):
    c: Coincident(g1,g-3)
    c: Coincident(g2,g1)
    c: Horizontal(g2)
    c: Coincident(g3,g1)
    c: Horizontal(g3)
    c: Tangent(g0,g3) = 1.5708
    c: Vertical(g4)
    c: Coincident(g4,g5)
    c: Distance(g4,g-2) = 6
    c: Tangent(g0,g5) = -1.5708
    c: Equal(g1,g-3)
    c: Angle(g4,g5) = 0.251327
    c: Coincident(g6,g-1)
    c: Tangent(g4,g6) = 1.5708
    c: Tangent(g6,g2) = 1.5708
    c: Coincident(g7,g6)
    c: Diameter(g7) = 4.9
    c: Equal(g0,g6)
    c: Coincident(g-4,g0)
FEATURE [PartDesign::Pad] Pad020  label="CL0_Pad010"
  BaseFeature = -> Pad019
  Direction = (1,0,0)
  Length = 1.6
  Length2 = 10
  Placement = pos=(0,0,0) rot=(1,1,1;2.0944rad)
  Profile = -> Sketch038
  ReferenceAxis = -> Sketch038 [N_Axis]
  Refine = true
  Reversed = true
  Suppressed = false
  Type = 0
FEATURE [Sketcher::SketchObject] Sketch040  label="CL0_Sketch016"
  ArcFitTolerance = 1e-06
  AttachmentSupport = -> [YZ_Plane007]
  FullyConstrained = true
  MakeInternals = false
  MapMode = 5
  Placement = pos=(0,0,0) rot=(0.57735,0.57735,0.57735;2.0944rad)
  expr: Constraints[10] = dd.CD_Radius
  expr: Constraints[11] = dd.CL_Len / 2
  expr: Constraints[7] = dd.CL_Radius
  expr: Constraints[8] = dd.CL_Radius
  expr: Constraints[9] = dd.CL_Len + dd.CL_Radius
  sketch-geometry (4):
    g0: ArcOfCircle CenterX=72.6064 CenterY=-9.1 CenterZ=0 NormalX=0 NormalY=0 NormalZ=1 AngleXU=0 Radius=80.0436 StartAngle=2.95181 EndAngle=3.33138
    g1: LineSegment StartX=-6 StartY=6 StartZ=0 EndX=-4.8 EndY=6 EndZ=0
    g2: LineSegment StartX=-4.8 StartY=6 StartZ=0 EndX=-4.8 EndY=-24.2 EndZ=0
    g3: LineSegment StartX=-4.8 StartY=-24.2 StartZ=0 EndX=-6 EndY=-24.2 EndZ=0
  constraints (13):
    c: Coincident(g0,g1)
    c: Coincident(g1,g2)
    c: Coincident(g2,g3)
    c: Coincident(g3,g0)
    c: Horizontal(g3)
    c: Horizontal(g1)
    c: Vertical(g2)
    c: Distance(g0,g-2) = 6
    c: Distance(g1,g-1) = 6
    c: Distance(g2,g-1) = 24.2
    c: Distance(g0,g-2) = 72.6064
    c: Distance(g0,g-1) = 9.1
    c: Distance(g3,g3) = 1.2
FEATURE [PartDesign::Pad] Pad021  label="CL0_Pad019"
  Direction = (1,0,0)
  Length = 14.2
  Length2 = 10
  Midplane = true
  Placement = pos=(0,0,0) rot=(1,1,1;2.0944rad)
  Profile = -> Sketch040
  ReferenceAxis = -> Sketch040 [N_Axis]
  Refine = true
  Suppressed = false
  Type = 0
  expr: Length = dd.CL_BW - 3.2 mm
FEATURE [Sketcher::SketchObject] Sketch042  label="RS_Sketch042"
  ArcFitTolerance = 1e-06
  AttachmentSupport = -> [XY_Plane017]
  FullyConstrained = true
  MakeInternals = false
  MapMode = 5
  expr: Constraints[15] = dd.RO_D / 2
  expr: Constraints[16] = dd.CL_BW / 2 + 1.6 mm
  expr: Constraints[17] = dd.CL_BW / 2 + 6.2 mm
  sketch-geometry (8):
    g0: LineSegment StartX=-10.3 StartY=8 StartZ=0 EndX=-10.3 EndY=10 EndZ=0
    g1: LineSegment StartX=-10.3 StartY=10 StartZ=0 EndX=14.9 EndY=10 EndZ=0
    g2: LineSegment StartX=14.9 StartY=10 StartZ=0 EndX=14.9 EndY=8 EndZ=0
    g3: LineSegment StartX=9.9 StartY=8 StartZ=0 EndX=9.9 EndY=6.8 EndZ=0
    g4: LineSegment StartX=9.9 StartY=6.8 StartZ=0 EndX=-5.3 EndY=6.8 EndZ=0
    g5: LineSegment StartX=-5.3 StartY=6.8 StartZ=0 EndX=-5.3 EndY=8 EndZ=0
    g6: LineSegment StartX=14.9 StartY=8 StartZ=0 EndX=9.9 EndY=8 EndZ=0
    g7: LineSegment StartX=-5.3 StartY=8 StartZ=0 EndX=-10.3 EndY=8 EndZ=0
  constraints (24):
    c: Vertical(g0)
    c: Coincident(g0,g1)
    c: Horizontal(g1)
    c: Coincident(g1,g2)
    c: Vertical(g2)
    c: Coincident(g6,g3)
    c: Vertical(g3)
    c: Coincident(g3,g4)
    c: Horizontal(g4)
    c: Coincident(g4,g5)
    c: Vertical(g5)
    c: Coincident(g5,g7)
    c: Equal(g5,g3)
    c: Distance(g5,g5) = 1.2
    c: Distance(g2,g6) = 5
    c: Distance(g1,g-1) = 10
    c: Distance(g0,g-2) = 10.3
    c: DistanceX(g-1,g1) = 14.9
    c: Distance(g2,g-1) = 8
    c: Horizontal(g6)
    c: Horizontal(g7)
    c: Coincident(g7,g0)
    c: Coincident(g6,g2)
    c: Equal(g6,g7)
FEATURE [PartDesign::Revolution] Revolution005  label="RS_Revolution005"
  Angle = 360
  Angle2 = 60
  Axis = (1,0,0)
  Base = (0,0,0)
  Profile = -> Sketch042
  ReferenceAxis = -> Sketch042 [H_Axis]
  Refine = true
  Suppressed = false
  Type = 0
FEATURE [PartDesign::Body] Body019  label="RollerShell"
  AllowCompound = false
  Group = -> [Sketch042,Revolution005]
  Origin = -> Origin019
  Placement = pos=(0,-89.4064,0) rot=(0,0,1;0rad)
  Tip = -> Revolution005
  expr: .Placement.Base.y = -dd.R1_Y
FEATURE [Part::Feature] Body021  label="RollerShell001"
  Placement = pos=(0,-56.6064,-70.8042) rot=(0,0,1;0rad)
  shape: bbox 25.2 x 20 x 20 mm, 8 faces (baked)
  expr: .Placement.Base.y = dd.R2_Y
  expr: .Placement.Base.z = dd.R2_Z
FEATURE [Sketcher::SketchObject] Sketch043  label="RP_Sketch043"
  ArcFitTolerance = 1e-06
  AttachmentSupport = -> [XY_Plane018]
  FullyConstrained = true
  MakeInternals = false
  MapMode = 5
  expr: Constraints[12] = (dd.CL_BW + 6.2 mm + 1.6 mm) / 2 + (6.2 mm - 1.6 mm) / 2 + 2 mm
  sketch-geometry (8):
    g0: LineSegment StartX=2.3 StartY=1.6 StartZ=0 EndX=2.3 EndY=3 EndZ=0
    g1: LineSegment StartX=2.3 StartY=1.6 StartZ=0 EndX=16.9 EndY=1.6 EndZ=0
    g2: LineSegment StartX=16.9 StartY=1.6 StartZ=0 EndX=16.9 EndY=6 EndZ=0
    g3: LineSegment StartX=16.9 StartY=6 StartZ=0 EndX=14.9 EndY=6 EndZ=0
    g4: LineSegment StartX=14.9 StartY=6 StartZ=0 EndX=14.9 EndY=4 EndZ=0
    g5: LineSegment StartX=14.9 StartY=4 StartZ=0 EndX=3.3 EndY=4 EndZ=0
    g6: ArcOfCircle CenterX=3.3 CenterY=3 CenterZ=0 NormalX=0 NormalY=0 NormalZ=1 AngleXU=0 Radius=1 StartAngle=1.5708 EndAngle=3.14159
    g7: GeomPoint [constr] X=2.3 Y=4 Z=0
  constraints (22):
    c: Vertical(g0)
    c: DistanceX(g-1,g0) = 2.3
    c: Coincident(g1,g2)
    c: Vertical(g2)
    c: Coincident(g2,g3)
    c: Coincident(g3,g4)
    c: Vertical(g4)
    c: Coincident(g4,g5)
    c: Horizontal(g5)
    c: Horizontal(g3)
    c: Horizontal(g1)
    c: Distance(g0,g-1) = 1.6
    c: Distance(g1,g-2) = 16.9
    c: Distance(g3,g3) = 2
    c: Equal(g4,g3)
    c: Distance(g4,g-1) = 4
    c: PointOnObject(g7,g0)
    c: PointOnObject(g7,g5)
    c: Tangent(g0,g6) = 1.5708
    c: Tangent(g5,g6) = -1.5708
    c: Radius(g6) = 1
    c: Coincident(g1,g0)
FEATURE [PartDesign::Revolution] Revolution006  label="RP_Revolution006"
  Angle = 360
  Angle2 = 60
  Axis = (1,0,0)
  Base = (0,0,0)
  Profile = -> Sketch043
  ReferenceAxis = -> Sketch043 [H_Axis]
  Refine = true
  Suppressed = false
  Type = 0
FEATURE [PartDesign::Body] Body020  label="RollerPin1"
  AllowCompound = false
  Group = -> [Sketch043,Revolution006]
  Origin = -> Origin020
  Placement = pos=(0,-56.6064,-70.8042) rot=(0,0,1;0rad)
  Tip = -> Revolution006
  expr: .Placement.Base.y = dd.R2_Y
  expr: .Placement.Base.z = dd.R2_Z
FEATURE [Part::FeaturePython] Tube  label="RollerPin2"  # WARN: FeaturePython — macro-defined, semantics opaque (R4)
  AttacherType = Attacher::AttachEngine3D
  Height = 15.2
  InnerRadius = 4
  OuterRadius = 5.2
  Placement = pos=(-5.3,-56.6064,-70.8042) rot=(0,1,0;1.5708rad)
  expr: .Placement.Base.x = -Height / 2 + (6.2 mm - 1.6 mm) / 2
  expr: .Placement.Base.y = dd.R2_Y
  expr: .Placement.Base.z = dd.R2_Z
  expr: Height = dd.CL_BW + 7.8 mm - 10 mm
FEATURE [PartDesign::Pocket] Pocket013  label="F1_Pocket013"
  BaseFeature = -> Pad016
  Direction = (-1,0,0)
  Length = 2
  Length2 = 5
  Placement = pos=(0,0,0) rot=(1,0,0;1.5708rad)
  Profile = -> Sketch030
  ReferenceAxis = -> Sketch030 [N_Axis]
  Refine = true
  Suppressed = false
  Type = 0
FEATURE [PartDesign::Hole] Hole005  label="FM_Hole005"
  BaseFeature = -> Hole
  CustomThreadClearance = 0
  Depth = 264.633
  DepthType = 1
  Diameter = 6
  DrillForDepth = false
  DrillPoint = 1
  DrillPointAngle = 118
  HoleCutCountersinkAngle = 90
  HoleCutCustomValues = false
  HoleCutDepth = 0
  HoleCutDiameter = 6.1
  HoleCutType = 0
  ModelThread = false
  Placement = pos=(0,0,0) rot=(1,1,1;2.0944rad)
  Profile = -> Sketch021
  Refine = true
  Suppressed = false
  Tapered = false
  TaperedAngle = 117
  ThreadClass = 0
  ThreadDepth = 264.633
  ThreadDepthType = 0
  ThreadDirection = 0
  ThreadFit = 0
  ThreadSize = 0
  ThreadType = 0
  Threaded = false
  UseCustomThreadClearance = false
FEATURE [PartDesign::Mirrored] Mirrored  label="FM_Mirrored000"
  BaseFeature = -> Hole005
  MirrorPlane = -> YZ_Plane013
  Originals = -> [Pocket006,Pocket007]
  Placement = pos=(0,0,0) rot=(1,1,1;2.0944rad)
  Refine = true
  Suppressed = false
  TransformMode = 0
FEATURE [PartDesign::SubShapeBinder] Binder007  label="F1_Binder007"
  BindCopyOnChange = 0
  BindMode = 0
  ClaimChildren = false
  Context = -> Part001 [Body012.Binder007.]
  Fuse = false
  MakeFace = true
  OffsetFill = false
  OffsetIntersection = false
  OffsetJoinType = 0
  OffsetOpenResult = false
  PartialLoad = false
  Refine = true
  Relative = true
  Support = -> [Body013[Mirrored.Face2]]
  _Version = 2
FEATURE [Sketcher::SketchObject] Sketch044  label="F1_Sketch044"
  ArcFitTolerance = 1e-06
  AttachmentOffset = pos=(0,0,-16.7) rot=(0,0,1;0rad)
  AttachmentSupport = -> [YZ_Plane012]
  ExternalGeometry = -> [Binder007]
  FullyConstrained = true
  MakeInternals = false
  MapMode = 5
  Placement = pos=(-16.7,0,0) rot=(0.57735,0.57735,0.57735;2.0944rad)
  expr: .AttachmentOffset.Base.z = -<<F1_Pad016>>.Length2 - 2 mm
  expr: Constraints[28] = dd.CD_Radius + dd.CL_Radius + 4 mm
  expr: Constraints[37] = dd.FR_W
  expr: Constraints[38] = 19.6 mm - dd.CG_Z
  expr: Constraints[46] = dd.CD_Radius + dd.CL_Radius + 4.2 mm
  expr: Constraints[6] = dd.R1_Y
  expr: Constraints[7] = -dd.R2_Y
  expr: Constraints[8] = -dd.R2_Z
  sketch-geometry (22):
    g0: Circle CenterX=-26.3328 CenterY=36.244 CenterZ=0 NormalX=0 NormalY=0 NormalZ=1 AngleXU=0 Radius=1.55
    g1: Circle CenterX=26.3328 CenterY=36.244 CenterZ=0 NormalX=0 NormalY=0 NormalZ=1 AngleXU=0 Radius=1.55
    g2: Circle CenterX=42.6073 CenterY=-13.844 CenterZ=0 NormalX=0 NormalY=0 NormalZ=1 AngleXU=0 Radius=1.55
    g3: Circle CenterX=0 CenterY=-44.8 CenterZ=0 NormalX=0 NormalY=0 NormalZ=1 AngleXU=0 Radius=1.55
    g4: Circle CenterX=-29.0262 CenterY=-29.8 CenterZ=0 NormalX=0 NormalY=0 NormalZ=1 AngleXU=0 Radius=1.55
    g5: Circle CenterX=-42.6073 CenterY=-13.844 CenterZ=0 NormalX=0 NormalY=0 NormalZ=1 AngleXU=0 Radius=1.55
    g6: Circle CenterX=-56.6064 CenterY=-70.8042 CenterZ=0 NormalX=0 NormalY=0 NormalZ=1 AngleXU=0 Radius=1.55
    g7: Circle CenterX=-89.4064 CenterY=0 CenterZ=0 NormalX=0 NormalY=0 NormalZ=1 AngleXU=0 Radius=1.55
    g8: LineSegment StartX=-102 StartY=0 StartZ=0 EndX=-102 EndY=-82.8064 EndZ=0
    g9: LineSegment StartX=-102 StartY=-82.8064 StartZ=0 EndX=102 EndY=-82.8064 EndZ=0
    g10: LineSegment StartX=102 StartY=-82.8064 StartZ=0 EndX=102 EndY=0 EndZ=0
    g11: LineSegment StartX=-19.3936 StartY=82.6064 StartZ=0 EndX=19.3936 EndY=82.6064 EndZ=0
    g12: ArcOfCircle CenterX=-19.3936 CenterY=0 CenterZ=0 NormalX=0 NormalY=0 NormalZ=1 AngleXU=0 Radius=82.6064 StartAngle=1.5708 EndAngle=3.14159
    g13: ArcOfCircle CenterX=19.3936 CenterY=0 CenterZ=0 NormalX=0 NormalY=0 NormalZ=1 AngleXU=0 Radius=82.6064 StartAngle=0 EndAngle=1.5708
    g14: Circle CenterX=29.0262 CenterY=-29.8 CenterZ=0 NormalX=0 NormalY=0 NormalZ=1 AngleXU=0 Radius=1.55
    g15: Circle CenterX=92 CenterY=-44.6 CenterZ=0 NormalX=0 NormalY=0 NormalZ=1 AngleXU=0 Radius=3.05
    g16: Circle CenterX=-92 CenterY=-44.6 CenterZ=0 NormalX=0 NormalY=0 NormalZ=1 AngleXU=0 Radius=3.05
    g17: LineSegment [constr] StartX=-89.4064 StartY=0 StartZ=0 EndX=-89.4064 EndY=-70.8042 EndZ=0
    g18: LineSegment [constr] StartX=-56.6064 StartY=-70.8042 StartZ=0 EndX=-89.4064 EndY=-70.8042 EndZ=0
    g19: Circle CenterX=-89.4064 CenterY=-70.8042 CenterZ=0 NormalX=0 NormalY=0 NormalZ=1 AngleXU=0 Radius=1.55
    g20: Circle CenterX=-41.1 CenterY=-78.8064 CenterZ=0 NormalX=0 NormalY=0 NormalZ=1 AngleXU=0 Radius=1.6
    g21: Circle CenterX=41.1 CenterY=-78.8064 CenterZ=0 NormalX=0 NormalY=0 NormalZ=1 AngleXU=0 Radius=1.6
  constraints (52):
    c: Coincident(g0,g-7)
    c: Coincident(g1,g-6)
    c: Coincident(g2,g-5)
    c: Coincident(g3,g-4)
    c: Coincident(g5,g-3)
    c: PointOnObject(g7,g-1)
    c: Distance(g7,g-2) = 89.4064
    c: DistanceX(g6,g-1) = 56.6064
    c: Distance(g6,g-1) = 70.8042
    c: Equal(g7,g6)
    c: Equal(g6,g0)
    c: Equal(g0,g1)
    c: Equal(g1,g5)
    c: Equal(g5,g4)
    c: Equal(g4,g3)
    c: Equal(g3,g2)
    c: Diameter(g0) = 3.1
    c: Vertical(g8)
    c: Coincident(g8,g9)
    c: Horizontal(g9)
    c: Coincident(g9,g10)
    c: Vertical(g10)
    c: Horizontal(g11)
    c: Tangent(g13,g11) = 1.5708
    c: Tangent(g11,g12) = 1.5708
    c: Tangent(g8,g12) = -1.5708
    c: Tangent(g13,g10) = -1.5708
    c: Symmetric(g12,g13,g-2)
    c: DistanceY(g-1,g11) = 82.6064
    c: PointOnObject(g10,g-1)
    c: Coincident(g4,g-9)
    c: Coincident(g14,g-8)
    c: Equal(g2,g14)
    c: Equal(g16,g15)
    c: Symmetric(g16,g15,g-2)
    c: Diameter(g16) = 6.1
    c: DistanceX(g15,g9) = 10
    c: DistanceX(g9,g9) = 204
    c: DistanceY(g15,g10) = 44.6
    c: Vertical(g17)
    c: Coincident(g18,g6)
    c: Horizontal(g18)
    c: Coincident(g18,g17)
    c: Coincident(g7,g17)
    c: Coincident(g19,g17)
    c: Equal(g19,g7)
    c: Distance(g8,g-1) = 82.8064
    c: Symmetric(g21,g20,g-2)
    c: Equal(g20,g21)
    c: Diameter(g21) = 3.2
    c: Distance(g20,g-2) = 41.1
    c: Distance(g21,g9) = 4
FEATURE [PartDesign::Pad] Pad022  label="F1_Pad022"
  BaseFeature = -> Pocket013
  Direction = (1,0,0)
  Length = 2
  Length2 = 10
  Placement = pos=(0,0,0) rot=(1,0,0;1.5708rad)
  Profile = -> Sketch044
  ReferenceAxis = -> Sketch044 [N_Axis]
  Refine = true
  Suppressed = false
  Type = 0
FEATURE [Sketcher::SketchObject] Sketch048  label="F2_Sketch048"
  ArcFitTolerance = 1e-06
  AttachmentSupport = -> [YZ_Plane019]
  FullyConstrained = true
  MakeInternals = false
  MapMode = 5
  Placement = pos=(0,0,0) rot=(0.57735,0.57735,0.57735;2.0944rad)
  expr: Constraints[0] = -dd.R2_Y
  expr: Constraints[1] = -dd.R2_Z
  expr: Constraints[22] = 4.8 mm - dd.CG_Z
  expr: Constraints[2] = dd.R1_Y
  expr: Constraints[30] = dd.FR_W / 2
  expr: Constraints[36] = dd.CD_Radius + dd.CL_Radius + 4.2 mm
  sketch-geometry (15):
    g0: Circle CenterX=-89.4064 CenterY=0 CenterZ=0 NormalX=0 NormalY=0 NormalZ=1 AngleXU=0 Radius=1.55
    g1: Circle CenterX=-56.6064 CenterY=-70.8042 CenterZ=0 NormalX=0 NormalY=0 NormalZ=1 AngleXU=0 Radius=1.55
    g2: ArcOfCircle CenterX=-89.4064 CenterY=0 CenterZ=0 NormalX=0 NormalY=0 NormalZ=1 AngleXU=0 Radius=12.5936 StartAngle=0.683944 EndAngle=3.14159
    g3: LineSegment StartX=-102 StartY=1.5e-15 StartZ=0 EndX=-102 EndY=-82.8064 EndZ=0
    g4: LineSegment StartX=-102 StartY=-82.8064 StartZ=0 EndX=-50.6064 EndY=-82.8064 EndZ=0
    g5: LineSegment StartX=-50.6064 StartY=-82.8064 StartZ=0 EndX=-50.6064 EndY=-29.8 EndZ=0
    g6: LineSegment StartX=-51.9559 StartY=-26.0089 StartZ=0 EndX=-79.6453 EndY=7.9573 EndZ=0
    g7: ArcOfCircle CenterX=-56.6064 CenterY=-29.8 CenterZ=0 NormalX=0 NormalY=0 NormalZ=1 AngleXU=0 Radius=6 StartAngle=2e-16 EndAngle=0.683944
    g8: Circle CenterX=-89.4064 CenterY=-29.8 CenterZ=0 NormalX=0 NormalY=0 NormalZ=1 AngleXU=0 Radius=1.55
    g9: Circle CenterX=-56.6064 CenterY=-29.8 CenterZ=0 NormalX=0 NormalY=0 NormalZ=1 AngleXU=0 Radius=1.55
    g10: LineSegment [constr] StartX=-89.4064 StartY=-29.8 StartZ=0 EndX=-56.6064 EndY=-29.8 EndZ=0
    g11: LineSegment [constr] StartX=-56.6064 StartY=-70.8042 StartZ=0 EndX=-56.6064 EndY=-29.8 EndZ=0
    g12: LineSegment [constr] StartX=-89.4064 StartY=-29.8 StartZ=0 EndX=-89.4064 EndY=0 EndZ=0
    g13: LineSegment [constr] StartX=-56.6064 StartY=-70.8042 StartZ=0 EndX=-89.4064 EndY=-70.8042 EndZ=0
    g14: Circle CenterX=-89.4064 CenterY=-70.8042 CenterZ=0 NormalX=0 NormalY=0 NormalZ=1 AngleXU=0 Radius=1.55
  constraints (37):
    c: Distance(g1,g-2) = 56.6064
    c: Distance(g1,g-1) = 70.8042
    c: Distance(g0,g-2) = 89.4064
    c: PointOnObject(g0,g-1)
    c: Equal(g0,g1)
    c: Diameter(g0) = 3.1
    c: Coincident(g2,g0)
    c: Horizontal(g4)
    c: Tangent(g2,g6) = -1.5708
    c: Tangent(g3,g2) = -1.5708
    c: Vertical(g3)
    c: Vertical(g5)
    c: Coincident(g5,g4)
    c: Tangent(g5,g7) = -1.5708
    c: Tangent(g6,g7) = -1.5708
    c: Equal(g8,g9)
    c: Diameter(g8) = 3.1
    c: Coincident(g9,g7)
    c: Radius(g7) = 6
    c: Coincident(g10,g8)
    c: Coincident(g10,g7)
    c: Horizontal(g10)
    c: Distance(g7,g-1) = 29.8
    c: Coincident(g11,g1)
    c: Coincident(g11,g7)
    c: Vertical(g11)
    c: Coincident(g12,g8)
    c: Coincident(g12,g0)
    c: Vertical(g12)
    c: Coincident(g3,g4)
    c: DistanceX(g2,g-1) = 102
    c: Coincident(g13,g1)
    c: Horizontal(g13)
    c: PointOnObject(g13,g12)
    c: Coincident(g14,g13)
    c: Equal(g14,g1)
    c: Distance(g4,g-1) = 82.8064
FEATURE [Sketcher::SketchObject] Sketch049  label="FM_Sketch049"
  ArcFitTolerance = 1e-06
  AttachmentOffset = pos=(0,0,-25) rot=(0,0,1;0rad)
  AttachmentSupport = -> [XY_Plane013]
  FullyConstrained = true
  MakeInternals = false
  MapMode = 5
  Placement = pos=(0,0,-25) rot=(0,0,1;0rad)
  expr: .AttachmentOffset.Base.z = dd.CG_Z
  expr: Constraints[3] = dd.FR_W / 2 - 10 mm
  sketch-geometry (2):
    g0: Circle CenterX=-5.6 CenterY=92 CenterZ=0 NormalX=0 NormalY=0 NormalZ=1 AngleXU=0 Radius=2.1
    g1: Circle CenterX=5.6 CenterY=-92 CenterZ=0 NormalX=0 NormalY=0 NormalZ=1 AngleXU=0 Radius=2.1
  constraints (5):
    c: Equal(g0,g1)
    c: Diameter(g1) = 4.2
    c: Symmetric(g0,g1,g-1)
    c: Distance(g0,g-1) = 92
    c: Distance(g0,g-2) = 5.6
FEATURE [PartDesign::Hole] Hole007  label="FM_Hole007"
  BaseFeature = -> Mirrored
  CustomThreadClearance = 0
  Depth = 448.653
  DepthType = 1
  Diameter = 4.2
  DrillForDepth = false
  DrillPoint = 1
  DrillPointAngle = 118
  HoleCutCountersinkAngle = 179
  HoleCutCustomValues = false
  HoleCutDepth = 3.6
  HoleCutDiameter = 7.6
  HoleCutType = 3
  ModelThread = false
  Placement = pos=(0,0,0) rot=(1,1,1;2.0944rad)
  Profile = -> Sketch049
  Refine = true
  Suppressed = false
  Tapered = false
  TaperedAngle = 90
  ThreadClass = 0
  ThreadDepth = 448.653
  ThreadDepthType = 0
  ThreadDirection = 0
  ThreadFit = 0
  ThreadSize = 0
  ThreadType = 0
  Threaded = false
  UseCustomThreadClearance = false
FEATURE [PartDesign::Pad] Pad025  label="F2_Pad025"
  Direction = (1,0,0)
  Length = 3.2
  Length2 = 10
  Placement = pos=(0,0,0) rot=(1,1,1;2.0944rad)
  Profile = -> Sketch048
  ReferenceAxis = -> Sketch048 [N_Axis]
  Refine = true
  Reversed = true
  Suppressed = false
  Type = 0
FEATURE [Sketcher::SketchObject] Sketch051  label="F2_Sketch051"
  ArcFitTolerance = 1e-06
  AttachmentOffset = pos=(0,0,-4) rot=(0,0,1;0rad)
  AttachmentSupport = -> [YZ_Plane019]
  ExternalGeometry = -> [Pad025]
  FullyConstrained = true
  MakeInternals = false
  MapMode = 5
  Placement = pos=(-4,0,0) rot=(0.57735,0.57735,0.57735;2.0944rad)
  expr: .AttachmentOffset.Base.z = -<<F2_Pad025>>.Length - 0.8 mm
  sketch-geometry (11):
    g0: ArcOfCircle CenterX=-89.4064 CenterY=2.98e-14 CenterZ=0 NormalX=0 NormalY=0 NormalZ=1 AngleXU=0 Radius=6 StartAngle=0 EndAngle=3.14159
    g1: ArcOfCircle CenterX=-89.4064 CenterY=-70.8042 CenterZ=0 NormalX=0 NormalY=0 NormalZ=1 AngleXU=0 Radius=6 StartAngle=3.14159 EndAngle=6.28319
    g2: LineSegment StartX=-83.4064 StartY=2.98e-14 StartZ=0 EndX=-83.4064 EndY=-70.8042 EndZ=0
    g3: LineSegment StartX=-95.4064 StartY=3.05e-14 StartZ=0 EndX=-95.4064 EndY=-70.8042 EndZ=0
    g4: Circle CenterX=-89.4064 CenterY=2.98e-14 CenterZ=0 NormalX=0 NormalY=0 NormalZ=1 AngleXU=0 Radius=1.55
    g5: Circle CenterX=-89.4064 CenterY=-70.8042 CenterZ=0 NormalX=0 NormalY=0 NormalZ=1 AngleXU=0 Radius=1.55
    g6: Circle CenterX=-56.6064 CenterY=-29.8 CenterZ=0 NormalX=0 NormalY=0 NormalZ=1 AngleXU=0 Radius=1.55
    g7: Circle CenterX=-56.6064 CenterY=-70.8042 CenterZ=0 NormalX=0 NormalY=0 NormalZ=1 AngleXU=0 Radius=1.55
    g8: Circle CenterX=-89.4064 CenterY=-29.8 CenterZ=0 NormalX=0 NormalY=0 NormalZ=1 AngleXU=0 Radius=1.55
    g9: Circle CenterX=-56.6064 CenterY=-29.8 CenterZ=0 NormalX=0 NormalY=0 NormalZ=1 AngleXU=0 Radius=6
    g10: Circle CenterX=-56.6064 CenterY=-70.8042 CenterZ=0 NormalX=0 NormalY=0 NormalZ=1 AngleXU=0 Radius=6
  constraints (22):
    c: Tangent(g0,g2) = 1.5708
    c: Tangent(g0,g3) = -1.5708
    c: Tangent(g1,g2) = 1.5708
    c: Tangent(g1,g3) = -1.5708
    c: Equal(g0,g1)
    c: Coincident(g0,g-3)
    c: Radius(g0) = 6
    c: Coincident(g4,g0)
    c: Coincident(g5,g1)
    c: Equal(g-3,g4)
    c: Equal(g-4,g6)
    c: Equal(g-5,g7)
    c: Coincident(g1,g-6)
    c: Equal(g-6,g5)
    c: Coincident(g8,g-7)
    c: Equal(g8,g-7)
    c: Coincident(g9,g6)
    c: Coincident(g10,g7)
    c: Equal(g10,g9)
    c: Equal(g9,g0)
    c: Coincident(g-4,g6)
    c: Coincident(g-5,g7)
FEATURE [PartDesign::Pad] Pad026  label="F2_Pad026"
  BaseFeature = -> Pad025
  Direction = (1,0,0)
  Length = 0.8
  Length2 = 10
  Placement = pos=(0,0,0) rot=(1,1,1;2.0944rad)
  Profile = -> Sketch051
  ReferenceAxis = -> Sketch051 [N_Axis]
  Refine = true
  Suppressed = false
  Type = 0
FEATURE [PartDesign::Chamfer] Chamfer002  label="F2_Chamfer002"
  Angle = 45
  Base = -> Pad026 [Edge45,Edge34,Edge31]
  BaseFeature = -> Pad026
  ChamferType = 0
  FlipDirection = false
  Placement = pos=(0,0,0) rot=(1,1,1;2.0944rad)
  Refine = true
  Size = 0.79
  Size2 = 1
  SupportTransform = false
  Suppressed = false
  UseAllEdges = false
FEATURE [Sketcher::SketchObject] Sketch052  label="F2_Sketch052"
  ArcFitTolerance = 1e-06
  AttachmentSupport = -> [YZ_Plane019]
  ExternalGeometry = -> [Chamfer002]
  FullyConstrained = true
  MakeInternals = false
  MapMode = 5
  Placement = pos=(0,0,0) rot=(0.57735,0.57735,0.57735;2.0944rad)
  sketch-geometry (21):
    g0: LineSegment StartX=-54.9899 StartY=-68.0042 StartZ=0 EndX=-58.223 EndY=-68.0042 EndZ=0
    g1: LineSegment StartX=-58.223 StartY=-68.0042 StartZ=0 EndX=-59.8396 EndY=-70.8042 EndZ=0
    g2: LineSegment StartX=-59.8396 StartY=-70.8042 StartZ=0 EndX=-58.223 EndY=-73.6042 EndZ=0
    g3: LineSegment StartX=-58.223 StartY=-73.6042 StartZ=0 EndX=-54.9899 EndY=-73.6042 EndZ=0
    g4: LineSegment StartX=-54.9899 StartY=-73.6042 StartZ=0 EndX=-53.3733 EndY=-70.8042 EndZ=0
    g5: LineSegment StartX=-53.3733 StartY=-70.8042 StartZ=0 EndX=-54.9899 EndY=-68.0042 EndZ=0
    g6: Circle [constr] CenterX=-56.6064 CenterY=-70.8042 CenterZ=0 NormalX=0 NormalY=0 NormalZ=1 AngleXU=0 Radius=3.23316
    g7: LineSegment StartX=-87.7899 StartY=-68.0042 StartZ=0 EndX=-91.023 EndY=-68.0042 EndZ=0
    g8: LineSegment StartX=-91.023 StartY=-68.0042 StartZ=0 EndX=-92.6396 EndY=-70.8042 EndZ=0
    g9: LineSegment StartX=-92.6396 StartY=-70.8042 StartZ=0 EndX=-91.023 EndY=-73.6042 EndZ=0
    g10: LineSegment StartX=-91.023 StartY=-73.6042 StartZ=0 EndX=-87.7899 EndY=-73.6042 EndZ=0
    g11: LineSegment StartX=-87.7899 StartY=-73.6042 StartZ=0 EndX=-86.1733 EndY=-70.8042 EndZ=0
    g12: LineSegment StartX=-86.1733 StartY=-70.8042 StartZ=0 EndX=-87.7899 EndY=-68.0042 EndZ=0
    g13: Circle [constr] CenterX=-89.4064 CenterY=-70.8042 CenterZ=0 NormalX=0 NormalY=0 NormalZ=1 AngleXU=0 Radius=3.23316
    g14: LineSegment StartX=-87.7899 StartY=2.8 StartZ=0 EndX=-91.023 EndY=2.8 EndZ=0
    g15: LineSegment StartX=-91.023 StartY=2.8 StartZ=0 EndX=-92.6396 EndY=5.95e-14 EndZ=0
    g16: LineSegment StartX=-92.6396 StartY=5.93e-14 StartZ=0 EndX=-91.023 EndY=-2.8 EndZ=0
    g17: LineSegment StartX=-91.023 StartY=-2.8 StartZ=0 EndX=-87.7899 EndY=-2.8 EndZ=0
    g18: LineSegment StartX=-87.7899 StartY=-2.8 StartZ=0 EndX=-86.1733 EndY=5.91e-14 EndZ=0
    g19: LineSegment StartX=-86.1733 StartY=5.91e-14 StartZ=0 EndX=-87.7899 EndY=2.8 EndZ=0
    g20: Circle [constr] CenterX=-89.4064 CenterY=5.96e-14 CenterZ=0 NormalX=0 NormalY=0 NormalZ=1 AngleXU=0 Radius=3.23316
  constraints (48):
    c: Coincident(g0,g1)
    c: Coincident(g1,g2)
    c: Coincident(g2,g3)
    c: Coincident(g3,g4)
    c: Coincident(g4,g5)
    c: Coincident(g5,g0)
    c: Equal(g0, g1-g5) x5
    c: PointOnObject(g0,g6)
    c: PointOnObject(g1,g6)
    c: PointOnObject(g2,g6)
    c: PointOnObject(g3,g6)
    c: PointOnObject(g4,g6)
    c: PointOnObject(g5,g6)
    c: Coincident(g7,g8)
    c: Coincident(g8,g9)
    c: Coincident(g9,g10)
    c: Coincident(g10,g11)
    c: Coincident(g11,g12)
    c: Coincident(g12,g7)
    c: Equal(g7, g8-g12) x5
    c: PointOnObject(g7,g13)
    c: PointOnObject(g8,g13)
    c: PointOnObject(g9,g13)
    c: PointOnObject(g10,g13)
    c: PointOnObject(g11,g13)
    c: PointOnObject(g12,g13)
    c: Coincident(g14,g15)
    c: Coincident(g15,g16)
    c: Coincident(g16,g17)
    c: Coincident(g17,g18)
    c: Coincident(g18,g19)
    c: Coincident(g19,g14)
    c: Equal(g14, g15-g19) x5
    c: PointOnObject(g14,g20)
    c: PointOnObject(g15,g20)
    c: PointOnObject(g16,g20)
    c: PointOnObject(g17,g20)
    c: PointOnObject(g18,g20)
    c: PointOnObject(g19,g20)
    c: Coincident(g20,g-3)
    c: Equal(g6,g13)
    c: Equal(g13,g20)
    c: Horizontal(g10)
    c: Horizontal(g17)
    c: Horizontal(g3)
    c: Distance(g3,g0) = 5.6
    c: Coincident(g6,g-5)
    c: Coincident(g-4,g13)
FEATURE [PartDesign::Pocket] Pocket016  label="F2_Pocket016"
  BaseFeature = -> Chamfer002
  Direction = (-1,0,0)
  Length = 2
  Length2 = 5
  Placement = pos=(0,0,0) rot=(1,1,1;2.0944rad)
  Profile = -> Sketch052
  ReferenceAxis = -> Sketch052 [N_Axis]
  Refine = true
  Suppressed = false
  Type = 0
FEATURE [Sketcher::SketchObject] Sketch053  label="PR_Sketch053"
  ArcFitTolerance = 1e-06
  AttachmentSupport = -> [YZ_Plane020]
  FullyConstrained = true
  MakeInternals = false
  MapMode = 5
  Placement = pos=(0,0,0) rot=(0.57735,0.57735,0.57735;2.0944rad)
  sketch-geometry (20):
    g0: LineSegment StartX=-10.1 StartY=10.1 StartZ=0 EndX=-3 EndY=10.1 EndZ=0
    g1: LineSegment StartX=-3 StartY=10.1 StartZ=0 EndX=-3 EndY=8.5 EndZ=0
    g2: LineSegment StartX=-3 StartY=8.5 StartZ=0 EndX=3 EndY=8.5 EndZ=0
    g3: LineSegment StartX=3 StartY=8.5 StartZ=0 EndX=3 EndY=10.1 EndZ=0
    g4: LineSegment StartX=3 StartY=10.1 StartZ=0 EndX=10.1 EndY=10.1 EndZ=0
    g5: LineSegment StartX=10.1 StartY=10.1 StartZ=0 EndX=10.1 EndY=3 EndZ=0
    g6: LineSegment StartX=10.1 StartY=3 StartZ=0 EndX=8.5 EndY=3 EndZ=0
    g7: LineSegment StartX=8.5 StartY=3 StartZ=0 EndX=8.5 EndY=-3 EndZ=0
    g8: LineSegment StartX=8.5 StartY=-3 StartZ=0 EndX=10.1 EndY=-3 EndZ=0
    g9: LineSegment StartX=10.1 StartY=-3 StartZ=0 EndX=10.1 EndY=-10.1 EndZ=0
    g10: LineSegment StartX=10.1 StartY=-10.1 StartZ=0 EndX=3 EndY=-10.1 EndZ=0
    g11: LineSegment StartX=3 StartY=-10.1 StartZ=0 EndX=3 EndY=-8.5 EndZ=0
    g12: LineSegment StartX=3 StartY=-8.5 StartZ=0 EndX=-3 EndY=-8.5 EndZ=0
    g13: LineSegment StartX=-3 StartY=-8.5 StartZ=0 EndX=-3 EndY=-10.1 EndZ=0
    g14: LineSegment StartX=-3 StartY=-10.1 StartZ=0 EndX=-10.1 EndY=-10.1 EndZ=0
    g15: LineSegment StartX=-10.1 StartY=-10.1 StartZ=0 EndX=-10.1 EndY=-3 EndZ=0
    g16: LineSegment StartX=-10.1 StartY=-3 StartZ=0 EndX=-8.5 EndY=-3 EndZ=0
    g17: LineSegment StartX=-8.5 StartY=-3 StartZ=0 EndX=-8.5 EndY=3 EndZ=0
    g18: LineSegment StartX=-8.5 StartY=3 StartZ=0 EndX=-10.1 EndY=3 EndZ=0
    g19: LineSegment StartX=-10.1 StartY=3 StartZ=0 EndX=-10.1 EndY=10.1 EndZ=0
  constraints (59):
    c: Horizontal(g0)
    c: Coincident(g0,g1)
    c: Vertical(g1)
    c: Coincident(g1,g2)
    c: Horizontal(g2)
    c: Coincident(g2,g3)
    c: Coincident(g3,g4)
    c: Horizontal(g4)
    c: Coincident(g4,g5)
    c: Vertical(g5)
    c: Coincident(g5,g6)
    c: Horizontal(g6)
    c: Coincident(g6,g7)
    c: Coincident(g7,g8)
    c: Coincident(g8,g9)
    c: Vertical(g9)
    c: Coincident(g9,g10)
    c: Horizontal(g10)
    c: Coincident(g10,g11)
    c: Coincident(g11,g12)
    c: Horizontal(g12)
    c: Coincident(g12,g13)
    c: Coincident(g13,g14)
    c: Horizontal(g14)
    c: Coincident(g14,g15)
    c: Vertical(g15)
    c: Coincident(g15,g16)
    c: Coincident(g16,g17)
    c: Coincident(g17,g18)
    c: Horizontal(g18)
    c: Coincident(g18,g19)
    c: Coincident(g19,g0)
    c: Vertical(g3)
    c: Vertical(g7)
    c: Horizontal(g8)
    c: Vertical(g11)
    c: Vertical(g13)
    c: Horizontal(g16)
    c: Vertical(g17)
    c: Vertical(g19)
    c: Symmetric(g0,g9,g-1)
    c: Equal(g0,g4)
    c: Equal(g4,g5)
    c: Equal(g5,g9)
    c: Equal(g9,g10)
    c: Equal(g10,g14)
    c: Equal(g14,g15)
    c: Equal(g15,g19)
    c: Equal(g1,g3)
    c: Equal(g3,g6)
    c: Equal(g6,g8)
    c: Equal(g8,g11)
    c: Equal(g11,g13)
    c: Equal(g13,g16)
    c: Equal(g16,g18)
    c: Equal(g7,g12)
    c: Distance(g11,g11) = 1.6
    c: DistanceY(g15,g18) = 6
    c: Distance(g0,g14) = 20.2
FEATURE [PartDesign::Pad] Pad027  label="RP_Pad027"
  Direction = (1,0,0)
  Length = 80
  Length2 = 43.4
  Placement = pos=(0,0,0) rot=(1,1,1;2.0944rad)
  Profile = -> Sketch053
  ReferenceAxis = -> Sketch053 [N_Axis]
  Refine = true
  Suppressed = false
  Type = 4
FEATURE [PartDesign::Body] Body023  label="PR1"
  AllowCompound = false
  Group = -> [Sketch053,Pad027]
  Origin = -> Origin022
  Placement = pos=(0,-92,-44.6) rot=(0,0,1;0rad)
  Tip = -> Pad027
  expr: .Placement.Base.y = -(dd.FR_W / 2 - 10 mm)
  expr: .Placement.Base.z = dd.CG_Z - 19.6 mm
FEATURE [Part::Mirroring] Part__Mirroring  label="PR1 (Mirror #1)"
  Base = (0,0,0)
  Normal = (0,1,0)
  Source = -> Body023
FEATURE [App::Part] Part  label="Ext"
  Group = -> [Body003,dd,Body,Body023,Part__Mirroring]
  Origin = -> Origin
FEATURE [Sketcher::SketchObject] Sketch054  label="FM_Sketch054"
  ArcFitTolerance = 1e-06
  AttachmentSupport = -> [Hole007]
  ExternalGeometry = -> [Hole007]
  FullyConstrained = true
  MakeInternals = false
  MapMode = 5
  Placement = pos=(10.6,0,0) rot=(0.57735,0.57735,0.57735;2.0944rad)
  expr: Constraints[5] = dd.R1_Y
  expr: Constraints[6] = -dd.R2_Y
  sketch-geometry (3):
    g0: LineSegment [constr] StartX=102 StartY=-29.8 StartZ=0 EndX=0 EndY=-29.8 EndZ=0
    g1: Circle CenterX=56.6064 CenterY=-29.8 CenterZ=0 NormalX=0 NormalY=0 NormalZ=1 AngleXU=0 Radius=1.6
    g2: Circle CenterX=89.4064 CenterY=-29.8 CenterZ=0 NormalX=0 NormalY=0 NormalZ=1 AngleXU=0 Radius=1.6
  constraints (9):
    c: Symmetric(g-3,g-3,g0)
    c: PointOnObject(g0,g-2)
    c: Horizontal(g0)
    c: PointOnObject(g1,g0)
    c: PointOnObject(g2,g0)
    c: Distance(g2,g-2) = 89.4064
    c: DistanceX(g-1,g1) = 56.6064
    c: Equal(g1,g2)
    c: Diameter(g1) = 3.2
FEATURE [PartDesign::Pocket] Pocket017  label="FM_Pocket017"
  BaseFeature = -> Hole007
  Direction = (-1,1.8e-15,0)
  Length = 10.6
  Length2 = 5
  Placement = pos=(0,0,0) rot=(1,1,1;2.0944rad)
  Profile = -> Sketch054
  ReferenceAxis = -> Sketch054 [N_Axis]
  Refine = true
  Suppressed = false
  Type = 0
  expr: Length = <<FM_Pad013>>.Length / 2
FEATURE [Sketcher::SketchObject] Sketch050  label="FM_Sketch050"
  ArcFitTolerance = 1e-06
  AttachmentOffset = pos=(0,0,-4) rot=(0,0,1;0rad)
  AttachmentSupport = -> [Pocket017]
  ExternalGeometry = -> [Pocket017]
  FullyConstrained = true
  MakeInternals = false
  MapMode = 5
  Placement = pos=(6.6,0,0) rot=(0.57735,0.57735,0.57735;2.0944rad)
  sketch-geometry (20):
    g0: LineSegment [constr] StartX=59.8396 StartY=-29.8 StartZ=0 EndX=58.223 EndY=-27 EndZ=0
    g1: LineSegment [constr] StartX=58.223 StartY=-27 StartZ=0 EndX=54.9899 EndY=-27 EndZ=0
    g2: LineSegment [constr] StartX=54.9899 StartY=-27 StartZ=0 EndX=53.3733 EndY=-29.8 EndZ=0
    g3: LineSegment StartX=53.3733 StartY=-29.8 StartZ=0 EndX=54.9899 EndY=-32.6 EndZ=0
    g4: LineSegment StartX=54.9899 StartY=-32.6 StartZ=0 EndX=58.223 EndY=-32.6 EndZ=0
    g5: LineSegment StartX=58.223 StartY=-32.6 StartZ=0 EndX=59.8396 EndY=-29.8 EndZ=0
    g6: Circle [constr] CenterX=56.6064 CenterY=-29.8 CenterZ=0 NormalX=0 NormalY=0 NormalZ=1 AngleXU=0 Radius=3.23316
    g7: LineSegment [constr] StartX=92.6396 StartY=-29.8 StartZ=0 EndX=91.023 EndY=-27 EndZ=0
    g8: LineSegment [constr] StartX=91.023 StartY=-27 StartZ=0 EndX=87.7899 EndY=-27 EndZ=0
    g9: LineSegment [constr] StartX=87.7899 StartY=-27 StartZ=0 EndX=86.1733 EndY=-29.8 EndZ=0
    g10: LineSegment StartX=86.1733 StartY=-29.8 StartZ=0 EndX=87.7899 EndY=-32.6 EndZ=0
    g11: LineSegment StartX=87.7899 StartY=-32.6 StartZ=0 EndX=91.023 EndY=-32.6 EndZ=0
    g12: LineSegment StartX=91.023 StartY=-32.6 StartZ=0 EndX=92.6396 EndY=-29.8 EndZ=0
    g13: Circle [constr] CenterX=89.4064 CenterY=-29.8 CenterZ=0 NormalX=0 NormalY=0 NormalZ=1 AngleXU=0 Radius=3.23316
    g14: LineSegment StartX=53.3733 StartY=-29.8 StartZ=0 EndX=53.3733 EndY=-25 EndZ=0
    g15: LineSegment StartX=53.3733 StartY=-25 StartZ=0 EndX=59.8396 EndY=-25 EndZ=0
    g16: LineSegment StartX=59.8396 StartY=-25 StartZ=0 EndX=59.8396 EndY=-29.8 EndZ=0
    g17: LineSegment StartX=86.1733 StartY=-29.8 StartZ=0 EndX=86.1733 EndY=-25 EndZ=0
    g18: LineSegment StartX=86.1733 StartY=-25 StartZ=0 EndX=92.6396 EndY=-25 EndZ=0
    g19: LineSegment StartX=92.6396 StartY=-25 StartZ=0 EndX=92.6396 EndY=-29.8 EndZ=0
  constraints (48):
    c: Coincident(g0,g1)
    c: Coincident(g1,g2)
    c: Coincident(g2,g3)
    c: Coincident(g3,g4)
    c: Coincident(g4,g5)
    c: Coincident(g5,g0)
    c: Equal(g0, g1-g5) x5
    c: PointOnObject(g0,g6)
    c: PointOnObject(g1,g6)
    c: PointOnObject(g2,g6)
    c: PointOnObject(g3,g6)
    c: PointOnObject(g4,g6)
    c: PointOnObject(g5,g6)
    c: Coincident(g7,g8)
    c: Coincident(g8,g9)
    c: Coincident(g9,g10)
    c: Coincident(g10,g11)
    c: Coincident(g11,g12)
    c: Coincident(g12,g7)
    c: Equal(g7, g8-g12) x5
    c: PointOnObject(g7,g13)
    c: PointOnObject(g8,g13)
    c: PointOnObject(g9,g13)
    c: PointOnObject(g10,g13)
    c: PointOnObject(g11,g13)
    c: PointOnObject(g12,g13)
    c: Equal(g13,g6)
    c: Horizontal(g1)
    c: Horizontal(g8)
    c: Distance(g3,g1) = 5.6
    c: Coincident(g2,g14)
    c: Vertical(g14)
    c: Coincident(g15,g16)
    c: Coincident(g16,g0)
    c: Vertical(g16)
    c: Coincident(g9,g17)
    c: Vertical(g17)
    c: Coincident(g18,g19)
    c: Coincident(g19,g7)
    c: Vertical(g19)
    c: Coincident(g18,g17)
    c: Horizontal(g18)
    c: Coincident(g15,g14)
    c: Horizontal(g15)
    c: PointOnObject(g18,g-3)
    c: PointOnObject(g15,g-3)
    c: Coincident(g13,g-5)
    c: Coincident(g6,g-4)
FEATURE [PartDesign::Pocket] Pocket018  label="FM_Pocket018"
  BaseFeature = -> Pocket017
  Direction = (-1,1.9e-15,1e-16)
  Length = 2.4
  Length2 = 5
  Placement = pos=(0,0,0) rot=(1,1,1;2.0944rad)
  Profile = -> Sketch050
  ReferenceAxis = -> Sketch050 [N_Axis]
  Refine = true
  Suppressed = false
  Type = 0
FEATURE [Sketcher::SketchObject] Sketch055  label="FM_Sketch055"
  ArcFitTolerance = 1e-06
  AttachmentSupport = -> [Pocket018]
  ExternalGeometry = -> [Pocket018]
  FullyConstrained = true
  MakeInternals = false
  MapMode = 5
  Placement = pos=(0,-7.6e-15,-34.6) rot=(0.707107,0.707107,0;3.14159rad)
  sketch-geometry (8):
    g0: LineSegment StartX=-95 StartY=8.6 StartZ=0 EndX=-95 EndY=2.6 EndZ=0
    g1: LineSegment StartX=-95 StartY=2.6 StartZ=0 EndX=-89 EndY=2.6 EndZ=0
    g2: LineSegment StartX=-89 StartY=2.6 StartZ=0 EndX=-89 EndY=8.6 EndZ=0
    g3: LineSegment StartX=-89 StartY=8.6 StartZ=0 EndX=-95 EndY=8.6 EndZ=0
    g4: LineSegment StartX=89 StartY=-2.6 StartZ=0 EndX=89 EndY=-8.6 EndZ=0
    g5: LineSegment StartX=89 StartY=-8.6 StartZ=0 EndX=95 EndY=-8.6 EndZ=0
    g6: LineSegment StartX=95 StartY=-8.6 StartZ=0 EndX=95 EndY=-2.6 EndZ=0
    g7: LineSegment StartX=95 StartY=-2.6 StartZ=0 EndX=89 EndY=-2.6 EndZ=0
  constraints (22):
    c: Coincident(g0,g1)
    c: Coincident(g1,g2)
    c: Coincident(g2,g3)
    c: Coincident(g3,g0)
    c: Vertical(g0)
    c: Vertical(g2)
    c: Horizontal(g1)
    c: Horizontal(g3)
    c: PointOnObject(g0,g-7)
    c: Coincident(g4,g5)
    c: Coincident(g5,g6)
    c: Coincident(g6,g7)
    c: Coincident(g7,g4)
    c: Vertical(g4)
    c: Vertical(g6)
    c: Horizontal(g5)
    c: Horizontal(g7)
    c: PointOnObject(g4,g-5)
    c: Symmetric(g4,g6,g-4)
    c: Symmetric(g0,g2,g-3)
    c: Equal(g2,g1)
    c: Equal(g4,g5)
FEATURE [PartDesign::Pocket] Pocket019  label="FM_Pocket019"
  BaseFeature = -> Pocket018
  Direction = (-3.1e-15,1.3e-15,1)
  Length = 5
  Length2 = 5
  Placement = pos=(0,0,0) rot=(1,1,1;2.0944rad)
  Profile = -> Sketch055
  ReferenceAxis = -> Sketch055 [N_Axis]
  Refine = true
  Reversed = true
  Suppressed = false
  Type = 1
FEATURE [PartDesign::PolarPattern] PolarPattern001  label="FM_PolarPattern001"
  Angle = 360
  Axis = -> Z_Axis013
  BaseFeature = -> Pocket019
  Mode = 0
  Occurrences = 2
  Offset = 120
  Originals = -> [Pocket017,Pocket018]
  Placement = pos=(0,0,0) rot=(1,1,1;2.0944rad)
  Refine = true
  Suppressed = false
  TransformMode = 0
FEATURE [PartDesign::Body] Body013  label="FrameMotor"
  AllowCompound = false
  Group = -> [Binder003,Sketch020,Sketch021,Pad012,Sketch022,Sketch023,Pad013,Pocket004,Sketch026,Pocket006,Sketch027,Pocket007,Pocket008,Hole,Hole005,Mirrored,Sketch049,Hole007,Sketch050,Sketch054,Pocket017,Pocket018,Sketch055,Pocket019,PolarPattern001]
  Origin = -> Origin013
  Tip = -> PolarPattern001
FEATURE [PartDesign::SubShapeBinder] Binder011  label="F2_Binder011_RP"
  BindCopyOnChange = 0
  BindMode = 0
  ClaimChildren = false
  Context = -> Part001 [Body022.Binder011.]
  Fuse = false
  MakeFace = true
  OffsetFill = false
  OffsetIntersection = false
  OffsetJoinType = 0
  OffsetOpenResult = false
  PartialLoad = false
  Refine = true
  Relative = true
  Support = -> [Part[Body023.Pad027.Face22]]
  _Version = 2
FEATURE [PartDesign::Pocket] Pocket020  label="F2_Pocket020"
  BaseFeature = -> Pocket016
  Direction = (-1,0,-3e-16)
  Length = 5
  Length2 = 5
  Placement = pos=(0,0,0) rot=(1,1,1;2.0944rad)
  Profile = -> Binder011
  Refine = true
  Suppressed = false
  Type = 1
FEATURE [PartDesign::Hole] Hole008  label="F2_Hole008"
  BaseFeature = -> Pocket020
  CustomThreadClearance = 0
  Depth = 2
  DepthType = 0
  Diameter = 5.6
  DrillForDepth = false
  DrillPoint = 0
  DrillPointAngle = 118
  HoleCutCountersinkAngle = 90
  HoleCutCustomValues = false
  HoleCutDepth = 0
  HoleCutDiameter = 6.1
  HoleCutType = 0
  ModelThread = false
  Placement = pos=(0,0,0) rot=(1,1,1;2.0944rad)
  Profile = -> Sketch051 [Edge7,Edge9]
  Refine = true
  Reversed = true
  Suppressed = false
  Tapered = false
  TaperedAngle = 90
  ThreadClass = 0
  ThreadDepth = 2
  ThreadDepthType = 0
  ThreadDirection = 0
  ThreadFit = 0
  ThreadSize = 0
  ThreadType = 0
  Threaded = false
  UseCustomThreadClearance = false
FEATURE [PartDesign::Body] Body022  label="Frame2"
  AllowCompound = false
  Group = -> [Sketch048,Pad025,Sketch051,Pad026,Chamfer002,Sketch052,Pocket016,Binder011,Pocket020,Hole008]
  Origin = -> Origin021
  Placement = pos=(20.1,0,0) rot=(0,0,1;0rad)
  Tip = -> Hole008
  expr: .Placement.Base.x = -dd.D1_X - 10.6 mm
FEATURE [Sketcher::SketchObject] Sketch057  label="F1_Sketch057"
  ArcFitTolerance = 1e-06
  AttachmentOffset = pos=(0,0,-14.7) rot=(0,0,1;0rad)
  AttachmentSupport = -> [YZ_Plane012]
  ExternalGeometry = -> [Pad022,Binder007]
  FullyConstrained = true
  MakeInternals = false
  MapMode = 5
  Placement = pos=(-14.7,0,0) rot=(0.57735,0.57735,0.57735;2.0944rad)
  expr: .AttachmentOffset.Base.z = -<<F1_Pad016>>.Length2
  expr: Constraints[25] = dd.CD_Radius
  sketch-geometry (18):
    g0: LineSegment [constr] StartX=-26.3328 StartY=36.244 StartZ=0 EndX=-22.3358 EndY=30.7426 EndZ=0
    g1: ArcOfCircle CenterX=0 CenterY=0 CenterZ=0 NormalX=0 NormalY=0 NormalZ=1 AngleXU=0 Radius=38 StartAngle=5.56517 EndAngle=10.1428
    g2: LineSegment StartX=-28.6182 StartY=-25 StartZ=0 EndX=28.6182 EndY=-25 EndZ=0
    g3: ArcOfCircle CenterX=-19.3936 CenterY=0 CenterZ=0 NormalX=0 NormalY=0 NormalZ=1 AngleXU=0 Radius=82.6064 StartAngle=1.5708 EndAngle=3.14159
    g4: ArcOfCircle CenterX=19.3936 CenterY=0 CenterZ=0 NormalX=0 NormalY=0 NormalZ=1 AngleXU=0 Radius=82.6064 StartAngle=1e-16 EndAngle=1.5708
    g5: LineSegment StartX=-19.3936 StartY=82.6064 StartZ=0 EndX=19.3936 EndY=82.6064 EndZ=0
    g6: LineSegment StartX=102 StartY=1.01e-14 StartZ=0 EndX=102 EndY=-82.8064 EndZ=0
    g7: LineSegment StartX=-102 StartY=-82.8064 StartZ=0 EndX=-102 EndY=1.42e-14 EndZ=0
    g8: LineSegment StartX=-76.6064 StartY=-82.8064 StartZ=0 EndX=-102 EndY=-82.8064 EndZ=0
    g9: LineSegment StartX=102 StartY=-82.8064 StartZ=0 EndX=-68.6064 EndY=-82.8064 EndZ=0
    g10: LineSegment [constr] StartX=-68.6064 StartY=-82.8064 StartZ=0 EndX=-76.6064 EndY=-82.8064 EndZ=0
    g11: LineSegment [constr] StartX=-72.6064 StartY=-82.8064 StartZ=0 EndX=-72.6064 EndY=0 EndZ=0
    g12: LineSegment StartX=-76.6064 StartY=-82.8064 StartZ=0 EndX=-76.6064 EndY=2.84e-14 EndZ=0
    g13: LineSegment StartX=-68.6064 StartY=-82.8064 StartZ=0 EndX=-68.6064 EndY=-34.0838 EndZ=0
    g14: ArcOfCircle CenterX=0 CenterY=0 CenterZ=0 NormalX=0 NormalY=0 NormalZ=1 AngleXU=0 Radius=76.6064 StartAngle=3.60268 EndAngle=9.42478
    g15: Circle CenterX=0 CenterY=0 CenterZ=0 NormalX=0 NormalY=0 NormalZ=1 AngleXU=0 Radius=68.6064
    g16: GeomPoint X=-68.6064 Y=0 Z=0
    g17: GeomPoint X=-23.5114 Y=32.3607 Z=0
  constraints (44):
    c: Horizontal(g2)
    c: Coincident(g2,g1)
    c: Coincident(g1,g2)
    c: PointOnObject(g1,g-7)
    c: Coincident(g0,g-5)
    c: Coincident(g3,g-8)
    c: Coincident(g4,g-9)
    c: Horizontal(g5)
    c: Vertical(g6)
    c: Coincident(g9,g6)
    c: Coincident(g7,g8)
    c: Vertical(g7)
    c: Tangent(g5,g3) = 1.5708
    c: Tangent(g5,g4) = 1.5708
    c: Tangent(g4,g6) = 1.5708
    c: Tangent(g7,g3) = 1.5708
    c: Coincident(g8,g-4)
    c: Coincident(g10,g8)
    c: Horizontal(g8)
    c: Coincident(g9,g10)
    c: Horizontal(g9)
    c: Horizontal(g10)
    c: Symmetric(g10,g10,g11)
    c: PointOnObject(g11,g-1)
    c: Vertical(g11)
    c: Distance(g11,g1) = 72.6064
    c: DistanceX(g8,g9) = 8
    c: Coincident(g1,g-1)
    c: PointOnObject(g1,g0)
    c: Coincident(g12,g8)
    c: Vertical(g12)
    c: Coincident(g13,g9)
    c: Vertical(g13)
    c: Coincident(g14,g1)
    c: Tangent(g12,g14) = 1.5708
    c: Coincident(g13,g14)
    c: Coincident(g15,g1)
    c: PointOnObject(g16,g15)
    c: PointOnObject(g16,g13)
    c: PointOnObject(g16,g-1)
    c: PointOnObject(g0,g1)
    c: PointOnObject(g17,g0)
    c: PointOnObject(g17,g-5)
    c: Distance(g17,g0) = 2
FEATURE [PartDesign::Pad] Pad028  label="F1_Pad028"
  BaseFeature = -> Pad022
  Direction = (1,0,0)
  Length = 2
  Length2 = 10
  Placement = pos=(0,0,0) rot=(1,0,0;1.5708rad)
  Profile = -> Sketch057
  ReferenceAxis = -> Sketch057 [N_Axis]
  Refine = true
  Suppressed = false
  Type = 0
FEATURE [PartDesign::Hole] Hole009  label="F1_Hole009"
  BaseFeature = -> Pad028
  CustomThreadClearance = 0
  Depth = 531.123
  DepthType = 1
  Diameter = 6.2
  DrillForDepth = false
  DrillPoint = 1
  DrillPointAngle = 118
  HoleCutCountersinkAngle = 90
  HoleCutCustomValues = false
  HoleCutDepth = 0.5
  HoleCutDiameter = 12
  HoleCutType = 3
  ModelThread = false
  Placement = pos=(0,0,0) rot=(1,0,0;1.5708rad)
  Profile = -> Sketch044 [Edge16,Edge17]
  Refine = true
  Reversed = true
  Suppressed = false
  Tapered = false
  TaperedAngle = 90
  ThreadClass = 0
  ThreadDepth = 531.123
  ThreadDepthType = 0
  ThreadDirection = 0
  ThreadFit = 0
  ThreadSize = 0
  ThreadType = 0
  Threaded = false
  UseCustomThreadClearance = false
FEATURE [PartDesign::Hole] Hole010  label="F1_Hole010"
  BaseFeature = -> Hole009
  CustomThreadClearance = 0
  Depth = 531.123
  DepthType = 1
  Diameter = 3.2
  DrillForDepth = false
  DrillPoint = 1
  DrillPointAngle = 118
  HoleCutCountersinkAngle = 179
  HoleCutCustomValues = false
  HoleCutDepth = 3
  HoleCutDiameter = 5.6
  HoleCutType = 3
  ModelThread = false
  Placement = pos=(0,0,0) rot=(1,0,0;1.5708rad)
  Profile = -> Sketch044 [Edge4,Edge3,Edge6,Edge1,Edge2]
  Refine = true
  Reversed = true
  Suppressed = false
  Tapered = false
  TaperedAngle = 90
  ThreadClass = 0
  ThreadDepth = 531.123
  ThreadDepthType = 0
  ThreadDirection = 0
  ThreadFit = 0
  ThreadSize = 0
  ThreadType = 0
  Threaded = false
  UseCustomThreadClearance = false
FEATURE [PartDesign::Hole] Hole011  label="F1_Hole011"
  BaseFeature = -> Hole010
  CustomThreadClearance = 0
  Depth = 531.123
  DepthType = 1
  Diameter = 3.2
  DrillForDepth = false
  DrillPoint = 1
  DrillPointAngle = 118
  HoleCutCountersinkAngle = 179
  HoleCutCustomValues = false
  HoleCutDepth = 1.6
  HoleCutDiameter = 5.6
  HoleCutType = 3
  ModelThread = false
  Placement = pos=(0,0,0) rot=(1,0,0;1.5708rad)
  Profile = -> Sketch044 [Edge15,Edge5,Edge7,Edge18,Edge8]
  Refine = true
  Reversed = true
  Suppressed = false
  Tapered = false
  TaperedAngle = 90
  ThreadClass = 0
  ThreadDepth = 531.123
  ThreadDepthType = 0
  ThreadDirection = 0
  ThreadFit = 0
  ThreadSize = 0
  ThreadType = 0
  Threaded = false
  UseCustomThreadClearance = false
FEATURE [Sketcher::SketchObject] Sketch058  label="CL3_Sketch058"
  ArcFitTolerance = 1e-06
  AttachmentOffset = pos=(0,0,8.7) rot=(0,0,1;0rad)
  AttachmentSupport = -> [YZ_Plane005]
  ExternalGeometry = -> [Pad005,Pad006]
  FullyConstrained = true
  MakeInternals = false
  MapMode = 5
  Placement = pos=(8.7,0,0) rot=(0.57735,0.57735,0.57735;2.0944rad)
  expr: .AttachmentOffset.Base.z = dd.CL_BW / 2
  sketch-geometry (14):
    g0: LineSegment [constr] StartX=-2.6 StartY=6 StartZ=0 EndX=-2.6 EndY=-24.2 EndZ=0
    g1: LineSegment StartX=-2.6 StartY=6 StartZ=0 EndX=-6 EndY=6 EndZ=0
    g2: LineSegment StartX=-6 StartY=-24.2 StartZ=0 EndX=-2.6 EndY=-24.2 EndZ=0
    g3: LineSegment [constr] StartX=-2.6 StartY=-9.1 StartZ=0 EndX=0 EndY=-9.1 EndZ=0
    g4: LineSegment StartX=-2.6 StartY=6 StartZ=0 EndX=-2.6 EndY=4.2 EndZ=0
    g5: LineSegment StartX=-2.6 StartY=4.2 StartZ=0 EndX=-6.32449 EndY=4.2 EndZ=0
    g6: LineSegment StartX=-2.6 StartY=-24.2 StartZ=0 EndX=-2.6 EndY=-22.4 EndZ=0
    g7: LineSegment StartX=-2.6 StartY=-22.4 StartZ=0 EndX=-6.32449 EndY=-22.4 EndZ=0
    g8: ArcOfCircle CenterX=72.6064 CenterY=-9.1 CenterZ=0 NormalX=0 NormalY=0 NormalZ=1 AngleXU=0 Radius=80.0436 StartAngle=2.95181 EndAngle=2.97466
    g9: ArcOfCircle CenterX=72.6064 CenterY=-9.1 CenterZ=0 NormalX=0 NormalY=0 NormalZ=1 AngleXU=0 Radius=80.0436 StartAngle=3.30853 EndAngle=3.33138
    g10: LineSegment StartX=-5.77714 StartY=-6 StartZ=0 EndX=-2.6 EndY=-6 EndZ=0
    g11: LineSegment StartX=-2.6 StartY=-6 StartZ=0 EndX=-2.6 EndY=-12.2 EndZ=0
    g12: LineSegment StartX=-2.6 StartY=-12.2 StartZ=0 EndX=-5.77714 EndY=-12.2 EndZ=0
    g13: LineSegment StartX=-5.77714 StartY=-12.2 StartZ=0 EndX=-5.77714 EndY=-6 EndZ=0
  constraints (40):
    c: Vertical(g0)
    c: DistanceX(g0,g-1) = 2.6
    c: Coincident(g1,g0)
    c: Horizontal(g1)
    c: Coincident(g2,g0)
    c: Horizontal(g2)
    c: PointOnObject(g3,g-2)
    c: Coincident(g0,g4)
    c: PointOnObject(g4,g0)
    c: Coincident(g4,g5)
    c: Coincident(g0,g6)
    c: Coincident(g6,g7)
    c: Symmetric(g6,g4,g3)
    c: Symmetric(g0,g0,g3)
    c: Horizontal(g5)
    c: Coincident(g8,g-4)
    c: Coincident(g8,g5)
    c: Coincident(g1,g8)
    c: PointOnObject(g-3,g1)
    c: Equal(g8,g-3)
    c: Distance(g4,g4) = 1.8
    c: Horizontal(g7)
    c: PointOnObject(g-3,g2)
    c: Coincident(g9,g8)
    c: Coincident(g9,g2)
    c: Coincident(g9,g7)
    c: Equal(g-3,g9)
    c: PointOnObject(g3,g0)
    c: PointOnObject(g10,g0)
    c: Horizontal(g10)
    c: Coincident(g10,g11)
    c: PointOnObject(g11,g0)
    c: Coincident(g11,g12)
    c: Horizontal(g12)
    c: Coincident(g12,g13)
    c: Coincident(g13,g10)
    c: Vertical(g13)
    c: PointOnObject(g-4,g10)
    c: PointOnObject(g-4,g12)
    c: Distance(g10,g-4) = 1.6
FEATURE [PartDesign::Pocket] Pocket021  label="CL3_Pocket021"
  BaseFeature = -> Pad006
  Direction = (-1,0,0)
  Length = 1.6
  Length2 = 3
  Placement = pos=(0,0,0) rot=(1,1,1;2.0944rad)
  Profile = -> Sketch058
  ReferenceAxis = -> Sketch058 [N_Axis]
  Refine = true
  Suppressed = false
  Type = 4
  expr: Length = <<CL3_Pad005>>.Length
  expr: Length2 = <<CL3_Pad006>>.Length / 2
FEATURE [PartDesign::Body] Body006  label="ChainLink3"
  AllowCompound = false
  Group = -> [Sketch007,Pad005,Sketch008,Pad006,Sketch058,Pocket021]
  Origin = -> Origin005
  Placement = pos=(0,-72.6064,0) rot=(0,0,1;0rad)
  Tip = -> Pocket021
  expr: .Placement.Base.y = -dd.CD_Radius
FEATURE [Sketcher::SketchObject] Sketch059  label="CL4_Sketch059"
  ArcFitTolerance = 1e-06
  AttachmentOffset = pos=(0,0,-8.7) rot=(0,0,1;0rad)
  AttachmentSupport = -> [YZ_Plane006]
  ExternalGeometry = -> [Pad008]
  FullyConstrained = true
  MakeInternals = false
  MapMode = 5
  Placement = pos=(-8.7,0,0) rot=(0.57735,0.57735,0.57735;2.0944rad)
  expr: .AttachmentOffset.Base.z = -dd.CL_BW / 2
  sketch-geometry (14):
    g0: LineSegment [constr] StartX=-2.6 StartY=6 StartZ=0 EndX=-2.6 EndY=-24.2 EndZ=0
    g1: LineSegment [constr] StartX=-2.6 StartY=-9.1 StartZ=0 EndX=0 EndY=-9.1 EndZ=0
    g2: LineSegment StartX=-2.6 StartY=6 StartZ=0 EndX=-2.6 EndY=4.2 EndZ=0
    g3: LineSegment StartX=-2.6 StartY=4.2 StartZ=0 EndX=-6.32449 EndY=4.2 EndZ=0
    g4: LineSegment StartX=-6 StartY=6 StartZ=0 EndX=-2.6 EndY=6 EndZ=0
    g5: ArcOfCircle CenterX=72.6064 CenterY=-9.1 CenterZ=0 NormalX=0 NormalY=0 NormalZ=1 AngleXU=0 Radius=80.0436 StartAngle=2.95181 EndAngle=2.97466
    g6: LineSegment StartX=-6 StartY=-24.2 StartZ=0 EndX=-2.6 EndY=-24.2 EndZ=0
    g7: LineSegment StartX=-2.6 StartY=-24.2 StartZ=0 EndX=-2.6 EndY=-22.4 EndZ=0
    g8: LineSegment StartX=-2.6 StartY=-22.4 StartZ=0 EndX=-6.32449 EndY=-22.4 EndZ=0
    g9: ArcOfCircle CenterX=72.6064 CenterY=-9.1 CenterZ=0 NormalX=0 NormalY=0 NormalZ=1 AngleXU=0 Radius=80.0436 StartAngle=3.30853 EndAngle=3.33138
    g10: LineSegment StartX=-5.77714 StartY=-6 StartZ=0 EndX=-2.6 EndY=-6 EndZ=0
    g11: LineSegment StartX=-2.6 StartY=-6 StartZ=0 EndX=-2.6 EndY=-12.2 EndZ=0
    g12: LineSegment StartX=-2.6 StartY=-12.2 StartZ=0 EndX=-5.77714 EndY=-12.2 EndZ=0
    g13: LineSegment StartX=-5.77714 StartY=-12.2 StartZ=0 EndX=-5.77714 EndY=-6 EndZ=0
  constraints (40):
    c: PointOnObject(g0,g-4)
    c: PointOnObject(g0,g-5)
    c: DistanceX(g0,g-1) = 2.6
    c: Vertical(g0)
    c: Symmetric(g0,g0,g1)
    c: PointOnObject(g1,g-2)
    c: Horizontal(g1)
    c: Coincident(g0,g2)
    c: PointOnObject(g2,g0)
    c: Coincident(g2,g3)
    c: Horizontal(g3)
    c: Coincident(g4,g2)
    c: Horizontal(g4)
    c: Coincident(g5,g-3)
    c: Coincident(g5,g4)
    c: Coincident(g5,g3)
    c: Equal(g-3,g5)
    c: Distance(g2,g2) = 1.8
    c: Coincident(g6,g0)
    c: Horizontal(g6)
    c: Coincident(g6,g7)
    c: Coincident(g7,g8)
    c: Horizontal(g8)
    c: Symmetric(g7,g2,g1)
    c: Coincident(g9,g5)
    c: Coincident(g9,g6)
    c: Coincident(g9,g8)
    c: Equal(g9,g-3)
    c: PointOnObject(g10,g0)
    c: Horizontal(g10)
    c: Coincident(g10,g11)
    c: PointOnObject(g11,g0)
    c: Coincident(g11,g12)
    c: Horizontal(g12)
    c: Coincident(g12,g13)
    c: Coincident(g13,g10)
    c: Vertical(g13)
    c: PointOnObject(g-3,g10)
    c: PointOnObject(g-3,g12)
    c: Distance(g10,g-3) = 1.6
FEATURE [PartDesign::Pocket] Pocket022  label="CL4_Pocket022"
  BaseFeature = -> Pad008
  Direction = (-1,0,0)
  Length = 1.6
  Length2 = 1.6
  Placement = pos=(0,0,0) rot=(1,1,1;2.0944rad)
  Profile = -> Sketch059
  ReferenceAxis = -> Sketch059 [N_Axis]
  Refine = true
  Suppressed = false
  Type = 4
  expr: Length = <<CL4_Pad007>>.Length
  expr: Length2 = <<CL4_Pad008>>.Length
FEATURE [PartDesign::Body] Body007  label="ChainLink4"
  AllowCompound = false
  Group = -> [Sketch010,Pad007,Sketch011,Pad008,Sketch059,Pocket022]
  Origin = -> Origin006
  Placement = pos=(0,-72.6064,0) rot=(0,0,1;0rad)
  Tip = -> Pocket022
  expr: .Placement.Base.y = -dd.CD_Radius
FEATURE [PartDesign::SubShapeBinder] Binder  label="CL5_Binder000_CL3"
  BindCopyOnChange = 0
  BindMode = 0
  ClaimChildren = false
  Context = -> Part001 [Body008.Binder.]
  Fuse = false
  MakeFace = true
  OffsetFill = false
  OffsetIntersection = false
  OffsetJoinType = 0
  OffsetOpenResult = false
  PartialLoad = false
  Refine = true
  Relative = true
  Support = -> [Body006[Pocket021.Face4]]
  _Version = 2
FEATURE [Sketcher::SketchObject] Sketch013  label="CL5_Sketch013"
  ArcFitTolerance = 1e-06
  AttachmentSupport = -> [YZ_Plane007]
  ExternalGeometry = -> [Binder]
  FullyConstrained = true
  MakeInternals = false
  MapMode = 5
  Placement = pos=(0,0,0) rot=(0.57735,0.57735,0.57735;2.0944rad)
  sketch-geometry (4):
    g0: ArcOfCircle CenterX=4.26e-14 CenterY=-9.1 CenterZ=0 NormalX=0 NormalY=0 NormalZ=1 AngleXU=0 Radius=80.0436 StartAngle=2.95181 EndAngle=3.33138
    g1: LineSegment StartX=-78.6064 StartY=6 StartZ=0 EndX=-75.2064 EndY=6 EndZ=0
    g2: LineSegment StartX=-75.2064 StartY=6 StartZ=0 EndX=-75.2064 EndY=-24.2 EndZ=0
    g3: LineSegment StartX=-75.2064 StartY=-24.2 StartZ=0 EndX=-78.6064 EndY=-24.2 EndZ=0
  constraints (10):
    c: Coincident(g0,g1)
    c: Coincident(g1,g2)
    c: Coincident(g2,g3)
    c: Coincident(g3,g0)
    c: Horizontal(g3)
    c: Horizontal(g1)
    c: Coincident(g0,g-3)
    c: Equal(g-3,g0)
    c: Coincident(g1,g-4)
    c: Coincident(g2,g-5)
FEATURE [PartDesign::Pad] Pad009  label="CL5_Pad009"
  Direction = (1,0,0)
  Length = 14.2
  Length2 = 10
  Midplane = true
  Placement = pos=(0,0,0) rot=(1,1,1;2.0944rad)
  Profile = -> Sketch013
  ReferenceAxis = -> Sketch013 [N_Axis]
  Refine = true
  Suppressed = false
  Type = 0
  expr: Length = dd.CL_BW - 3.2 mm
FEATURE [Sketcher::SketchObject] Sketch060  label="CL5_Sketch060"
  ArcFitTolerance = 1e-06
  AttachmentSupport = -> [YZ_Plane007]
  ExternalGeometry = -> [Binder]
  FullyConstrained = true
  MakeInternals = false
  MapMode = 5
  Placement = pos=(0,0,0) rot=(0.57735,0.57735,0.57735;2.0944rad)
  sketch-geometry (16):
    g0: LineSegment StartX=-78.3836 StartY=-6.2 StartZ=0 EndX=-78.3836 EndY=-12 EndZ=0
    g1: LineSegment StartX=-78.3836 StartY=-12 StartZ=0 EndX=-75.2064 EndY=-12 EndZ=0
    g2: LineSegment StartX=-75.2064 StartY=-12 StartZ=0 EndX=-75.2064 EndY=-6.2 EndZ=0
    g3: LineSegment StartX=-75.2064 StartY=-6.2 StartZ=0 EndX=-78.3836 EndY=-6.2 EndZ=0
    g4: ArcOfCircle CenterX=1.42e-14 CenterY=-9.1 CenterZ=0 NormalX=0 NormalY=0 NormalZ=1 AngleXU=0 Radius=80.0436 StartAngle=2.95181 EndAngle=2.97212
    g5: ArcOfCircle CenterX=1.42e-14 CenterY=-9.1 CenterZ=0 NormalX=0 NormalY=0 NormalZ=1 AngleXU=0 Radius=80.0436 StartAngle=3.31106 EndAngle=3.33138
    g6: LineSegment [constr] StartX=-75.2064 StartY=-6 StartZ=0 EndX=-75.2064 EndY=-6.2 EndZ=0
    g7: LineSegment [constr] StartX=-78.3836 StartY=-12.2 StartZ=0 EndX=-78.3836 EndY=-12 EndZ=0
    g8: LineSegment [constr] StartX=-75.2064 StartY=4.2 StartZ=0 EndX=-75.2064 EndY=4.4 EndZ=0
    g9: LineSegment [constr] StartX=-75.2064 StartY=-22.4 StartZ=0 EndX=-75.2064 EndY=-22.6 EndZ=0
    g10: LineSegment StartX=-78.6064 StartY=6 StartZ=0 EndX=-75.2064 EndY=6 EndZ=0
    g11: LineSegment StartX=-75.2064 StartY=6 StartZ=0 EndX=-75.2064 EndY=4.4 EndZ=0
    g12: LineSegment StartX=-75.2064 StartY=4.4 StartZ=0 EndX=-78.897 EndY=4.4 EndZ=0
    g13: LineSegment StartX=-78.897 StartY=-22.6 StartZ=0 EndX=-75.2064 EndY=-22.6 EndZ=0
    g14: LineSegment StartX=-75.2064 StartY=-22.6 StartZ=0 EndX=-75.2064 EndY=-24.2 EndZ=0
    g15: LineSegment StartX=-75.2064 StartY=-24.2 StartZ=0 EndX=-78.6064 EndY=-24.2 EndZ=0
  constraints (42):
    c: Coincident(g0,g1)
    c: Coincident(g1,g2)
    c: Coincident(g2,g3)
    c: Coincident(g3,g0)
    c: Vertical(g0)
    c: Vertical(g2)
    c: Horizontal(g1)
    c: Horizontal(g3)
    c: PointOnObject(g-3,g2)
    c: PointOnObject(g-4,g0)
    c: Coincident(g4,g-7)
    c: Coincident(g5,g4)
    c: Coincident(g6,g-3)
    c: Coincident(g6,g2)
    c: Coincident(g7,g-4)
    c: Coincident(g7,g0)
    c: Coincident(g8,g-5)
    c: Coincident(g9,g-6)
    c: Vertical(g9)
    c: Vertical(g8)
    c: Equal(g8,g6)
    c: Equal(g6,g7)
    c: Equal(g7,g9)
    c: Distance(g8,g8) = 0.2
    c: Coincident(g4,g10)
    c: Coincident(g10,g11)
    c: Coincident(g11,g8)
    c: Coincident(g11,g12)
    c: Coincident(g12,g4)
    c: Coincident(g5,g13)
    c: Coincident(g13,g14)
    c: Coincident(g14,g-6)
    c: Coincident(g14,g15)
    c: Coincident(g15,g5)
    c: Equal(g5,g-7)
    c: Equal(g-7,g4)
    c: Horizontal(g10)
    c: Horizontal(g12)
    c: Horizontal(g13)
    c: Horizontal(g15)
    c: Coincident(g13,g9)
    c: Coincident(g10,g-5)
FEATURE [PartDesign::Pad] Pad029  label="CL5_Pad029"
  BaseFeature = -> Pad009
  Direction = (1,0,0)
  Length = 17.4
  Length2 = 0
  Midplane = true
  Placement = pos=(0,0,0) rot=(1,1,1;2.0944rad)
  Profile = -> Sketch060
  ReferenceAxis = -> Sketch060 [N_Axis]
  Refine = true
  Suppressed = false
  Type = 0
  expr: Length = dd.CL_BW
FEATURE [PartDesign::Pad] Pad030  label="CL5_Pad030"
  BaseFeature = -> Pad029
  Direction = (1,0,0)
  Length = 11.7
  Length2 = 10.3
  Placement = pos=(0,0,0) rot=(1,1,1;2.0944rad)
  Profile = -> Sketch060 [Edge4,Edge3,Edge2,Edge1]
  ReferenceAxis = -> Sketch060 [N_Axis]
  Refine = true
  Suppressed = false
  Type = 4
  expr: Length = dd.CL_BW / 2 + 3 mm
  expr: Length2 = dd.CL_BW / 2 + 1.6 mm
FEATURE [PartDesign::Body] Body008  label="ChainLink5"
  AllowCompound = false
  Group = -> [Sketch013,Pad009,Binder,Sketch060,Pad029,Pad030]
  Origin = -> Origin007
  Tip = -> Pad030
FEATURE [Sketcher::SketchObject] Sketch061  label="CL0_Sketch061"
  ArcFitTolerance = 1e-06
  AttachmentOffset = pos=(0,0,8.7) rot=(0,0,1;0rad)
  AttachmentSupport = -> [YZ_Plane016]
  ExternalGeometry = -> [Pad018]
  FullyConstrained = true
  MakeInternals = false
  MapMode = 5
  Placement = pos=(8.7,0,0) rot=(0.57735,0.57735,0.57735;2.0944rad)
  expr: .AttachmentOffset.Base.z = dd.CL_BW / 2
  sketch-geometry (14):
    g0: LineSegment [constr] StartX=-4.8 StartY=-24.2 StartZ=0 EndX=-4.8 EndY=6 EndZ=0
    g1: ArcOfCircle CenterX=72.6064 CenterY=-9.1 CenterZ=0 NormalX=0 NormalY=0 NormalZ=1 AngleXU=0 Radius=80.0436 StartAngle=3.30853 EndAngle=3.33138
    g2: LineSegment StartX=-6 StartY=-24.2 StartZ=0 EndX=-4.8 EndY=-24.2 EndZ=0
    g3: LineSegment StartX=-4.8 StartY=-24.2 StartZ=0 EndX=-4.8 EndY=-22.4 EndZ=0
    g4: LineSegment StartX=-4.8 StartY=-22.4 StartZ=0 EndX=-6.32449 EndY=-22.4 EndZ=0
    g5: LineSegment [constr] StartX=-4.8 StartY=6 StartZ=0 EndX=-6 EndY=6 EndZ=0
    g6: LineSegment StartX=-4.8 StartY=-11 StartZ=0 EndX=-4.8 EndY=-7.2 EndZ=0
    g7: LineSegment StartX=-4.8 StartY=-7.2 StartZ=0 EndX=-6.57714 EndY=-7.2 EndZ=0
    g8: LineSegment StartX=-6.57714 StartY=-7.2 StartZ=0 EndX=-6.57714 EndY=-11 EndZ=0
    g9: LineSegment StartX=-6.57714 StartY=-11 StartZ=0 EndX=-4.8 EndY=-11 EndZ=0
    g10: LineSegment StartX=-6 StartY=6 StartZ=0 EndX=-4.8 EndY=6 EndZ=0
    g11: LineSegment StartX=-4.8 StartY=6 StartZ=0 EndX=-4.8 EndY=4.2 EndZ=0
    g12: LineSegment StartX=-4.8 StartY=4.2 StartZ=0 EndX=-6.32449 EndY=4.2 EndZ=0
    g13: ArcOfCircle CenterX=72.6064 CenterY=-9.1 CenterZ=0 NormalX=0 NormalY=0 NormalZ=1 AngleXU=0 Radius=80.0436 StartAngle=2.95181 EndAngle=2.97466
  constraints (40):
    c: PointOnObject(g0,g-3)
    c: Vertical(g0)
    c: Distance(g0,g-2) = 4.8
    c: Coincident(g1,g-4)
    c: Coincident(g1,g2)
    c: Coincident(g2,g0)
    c: Coincident(g2,g3)
    c: PointOnObject(g3,g0)
    c: Coincident(g3,g4)
    c: Coincident(g4,g1)
    c: Equal(g1,g-4)
    c: Horizontal(g2)
    c: Horizontal(g4)
    c: Distance(g3,g3) = 1.8
    c: Coincident(g5,g0)
    c: Coincident(g5,g-4)
    c: Horizontal(g5)
    c: Coincident(g6,g7)
    c: Coincident(g7,g8)
    c: Coincident(g8,g9)
    c: Coincident(g9,g6)
    c: Vertical(g6)
    c: Vertical(g8)
    c: Horizontal(g7)
    c: Horizontal(g9)
    c: PointOnObject(g6,g0)
    c: DistanceY(g-4,g8) = 1.2
    c: Distance(g6,g6) = 3.8
    c: DistanceX(g-4,g8) = 0.8
    c: Coincident(g10,g0)
    c: Coincident(g0,g11)
    c: Coincident(g11,g12)
    c: Horizontal(g12)
    c: Equal(g11,g3)
    c: Vertical(g11)
    c: Horizontal(g10)
    c: Coincident(g13,g1)
    c: Coincident(g13,g12)
    c: Coincident(g13,g10)
    c: Equal(g-4,g13)
FEATURE [PartDesign::Pocket] Pocket023  label="CL0_Pocket023"
  BaseFeature = -> Pad018
  Direction = (-1,0,0)
  Length = 1.6
  Length2 = 3
  Placement = pos=(0,0,0) rot=(1,1,1;2.0944rad)
  Profile = -> Sketch061
  ReferenceAxis = -> Sketch061 [N_Axis]
  Refine = true
  Suppressed = false
  Type = 4
  expr: Length = <<CL0_Pad017>>.Length
  expr: Length2 = <<CL0_Pad018>>.Length / 2
FEATURE [PartDesign::Body] Body016  label="ChainLink0R"
  AllowCompound = false
  Group = -> [Sketch034,Pad017,Sketch035,Pad018,Sketch061,Pocket023]
  Origin = -> Origin016
  Placement = pos=(0,-72.6064,0) rot=(0,0,1;0rad)
  Tip = -> Pocket023
  expr: .Placement.Base.y = -dd.CD_Radius
FEATURE [Sketcher::SketchObject] Sketch062  label="CL0_Sketch062"
  ArcFitTolerance = 1e-06
  AttachmentOffset = pos=(0,0,-8.7) rot=(0,0,1;0rad)
  AttachmentSupport = -> [YZ_Plane006]
  ExternalGeometry = -> [Pad020]
  FullyConstrained = true
  MakeInternals = false
  MapMode = 5
  Placement = pos=(-8.7,0,0) rot=(0.57735,0.57735,0.57735;2.0944rad)
  expr: .AttachmentOffset.Base.z = -dd.CL_BW / 2
  sketch-geometry (14):
    g0: LineSegment [constr] StartX=-4.8 StartY=-24.2 StartZ=0 EndX=-4.8 EndY=6 EndZ=0
    g1: ArcOfCircle CenterX=72.6064 CenterY=-9.1 CenterZ=0 NormalX=0 NormalY=0 NormalZ=1 AngleXU=0 Radius=80.0436 StartAngle=3.30853 EndAngle=3.33138
    g2: LineSegment StartX=-6 StartY=-24.2 StartZ=0 EndX=-4.8 EndY=-24.2 EndZ=0
    g3: LineSegment StartX=-4.8 StartY=-24.2 StartZ=0 EndX=-4.8 EndY=-22.4 EndZ=0
    g4: LineSegment StartX=-4.8 StartY=-22.4 StartZ=0 EndX=-6.32449 EndY=-22.4 EndZ=0
    g5: LineSegment [constr] StartX=-4.8 StartY=6 StartZ=0 EndX=-6 EndY=6 EndZ=0
    g6: LineSegment StartX=-4.8 StartY=-11 StartZ=0 EndX=-4.8 EndY=-7.2 EndZ=0
    g7: LineSegment StartX=-4.8 StartY=-7.2 StartZ=0 EndX=-6.57714 EndY=-7.2 EndZ=0
    g8: LineSegment StartX=-6.57714 StartY=-7.2 StartZ=0 EndX=-6.57714 EndY=-11 EndZ=0
    g9: LineSegment StartX=-6.57714 StartY=-11 StartZ=0 EndX=-4.8 EndY=-11 EndZ=0
    g10: LineSegment StartX=-6 StartY=6 StartZ=0 EndX=-4.8 EndY=6 EndZ=0
    g11: LineSegment StartX=-4.8 StartY=6 StartZ=0 EndX=-4.8 EndY=4.2 EndZ=0
    g12: LineSegment StartX=-4.8 StartY=4.2 StartZ=0 EndX=-6.32449 EndY=4.2 EndZ=0
    g13: ArcOfCircle CenterX=72.6064 CenterY=-9.1 CenterZ=0 NormalX=0 NormalY=0 NormalZ=1 AngleXU=0 Radius=80.0436 StartAngle=2.95181 EndAngle=2.97466
  constraints (40):
    c: Vertical(g0)
    c: Distance(g0,g-2) = 4.8
    c: Coincident(g1,g2)
    c: Coincident(g2,g0)
    c: Coincident(g2,g3)
    c: PointOnObject(g3,g0)
    c: Coincident(g3,g4)
    c: Coincident(g4,g1)
    c: Horizontal(g2)
    c: Horizontal(g4)
    c: Distance(g3,g3) = 1.8
    c: Coincident(g5,g0)
    c: Horizontal(g5)
    c: Coincident(g6,g7)
    c: Coincident(g7,g8)
    c: Coincident(g8,g9)
    c: Coincident(g9,g6)
    c: Vertical(g6)
    c: Vertical(g8)
    c: Horizontal(g7)
    c: Horizontal(g9)
    c: PointOnObject(g6,g0)
    c: Distance(g6,g6) = 3.8
    c: Coincident(g10,g0)
    c: Coincident(g0,g11)
    c: Coincident(g11,g12)
    c: Horizontal(g12)
    c: Equal(g11,g3)
    c: Vertical(g11)
    c: Horizontal(g10)
    c: Coincident(g13,g1)
    c: Coincident(g13,g12)
    c: Coincident(g13,g10)
    c: DistanceY(g-3,g8) = 1.2
    c: DistanceX(g-3,g8) = 0.8
    c: Coincident(g5,g-3)
    c: Equal(g13,g-3)
    c: Equal(g1,g-3)
    c: PointOnObject(g0,g-4)
    c: Coincident(g1,g-3)
FEATURE [PartDesign::Pocket] Pocket024  label="CL0_Pocket024"
  BaseFeature = -> Pad020
  Direction = (-1,0,0)
  Length = 3.2
  Length2 = 5
  Midplane = true
  Placement = pos=(0,0,0) rot=(1,1,1;2.0944rad)
  Profile = -> Sketch062
  ReferenceAxis = -> Sketch062 [N_Axis]
  Refine = true
  Suppressed = false
  Type = 0
FEATURE [PartDesign::Body] Body017  label="ChainLink0L"
  AllowCompound = false
  Group = -> [Sketch037,Pad019,Sketch038,Pad020,Sketch062,Pocket024]
  Origin = -> Origin017
  Placement = pos=(0,-72.6064,0) rot=(0,0,1;0rad)
  Tip = -> Pocket024
  expr: .Placement.Base.y = -dd.CD_Radius
FEATURE [PartDesign::SubShapeBinder] Binder012  label="CL0_Binder012"
  BindCopyOnChange = 0
  BindMode = 0
  ClaimChildren = false
  Context = -> Part001 [Body018.Binder012.]
  Fuse = false
  MakeFace = true
  OffsetFill = false
  OffsetIntersection = false
  OffsetJoinType = 0
  OffsetOpenResult = false
  PartialLoad = false
  Refine = true
  Relative = true
  Support = -> [Body017[Pocket024.Face4]]
  _Version = 2
FEATURE [Sketcher::SketchObject] Sketch063  label="CL0_Sketch063"
  ArcFitTolerance = 1e-06
  AttachmentSupport = -> [YZ_Plane007]
  ExternalGeometry = -> [Pad021,Binder012]
  FullyConstrained = true
  MakeInternals = false
  MapMode = 5
  Placement = pos=(0,0,0) rot=(0.57735,0.57735,0.57735;2.0944rad)
  sketch-geometry (14):
    g0: ArcOfCircle CenterX=72.6064 CenterY=-9.1 CenterZ=0 NormalX=0 NormalY=0 NormalZ=1 AngleXU=0 Radius=80.0436 StartAngle=2.95181 EndAngle=2.97212
    g1: ArcOfCircle CenterX=72.6064 CenterY=-9.1 CenterZ=0 NormalX=0 NormalY=0 NormalZ=1 AngleXU=0 Radius=80.0436 StartAngle=3.31106 EndAngle=3.33138
    g2: LineSegment StartX=-6 StartY=-24.2 StartZ=0 EndX=-4.8 EndY=-24.2 EndZ=0
    g3: LineSegment StartX=-4.8 StartY=-24.2 StartZ=0 EndX=-4.8 EndY=-22.6 EndZ=0
    g4: LineSegment StartX=-4.8 StartY=-22.6 StartZ=0 EndX=-6.29053 EndY=-22.6 EndZ=0
    g5: LineSegment StartX=-6.29053 StartY=4.4 StartZ=0 EndX=-4.8 EndY=4.4 EndZ=0
    g6: LineSegment StartX=-4.8 StartY=4.4 StartZ=0 EndX=-4.8 EndY=6 EndZ=0
    g7: LineSegment StartX=-4.8 StartY=6 StartZ=0 EndX=-6 EndY=6 EndZ=0
    g8: LineSegment [constr] StartX=-6.57714 StartY=-7.2 StartZ=0 EndX=-6.57714 EndY=-7.3 EndZ=0
    g9: LineSegment [constr] StartX=-4.8 StartY=-11 StartZ=0 EndX=-4.8 EndY=-10.9 EndZ=0
    g10: LineSegment StartX=-6.57714 StartY=-7.3 StartZ=0 EndX=-6.57714 EndY=-10.9 EndZ=0
    g11: LineSegment StartX=-6.57714 StartY=-10.9 StartZ=0 EndX=-4.8 EndY=-10.9 EndZ=0
    g12: LineSegment StartX=-4.8 StartY=-10.9 StartZ=0 EndX=-4.8 EndY=-7.3 EndZ=0
    g13: LineSegment StartX=-4.8 StartY=-7.3 StartZ=0 EndX=-6.57714 EndY=-7.3 EndZ=0
  constraints (38):
    c: Coincident(g0,g-3)
    c: Coincident(g1,g0)
    c: Coincident(g1,g2)
    c: Coincident(g2,g-4)
    c: Coincident(g2,g3)
    c: Coincident(g3,g4)
    c: Coincident(g4,g1)
    c: Coincident(g0,g5)
    c: Coincident(g5,g6)
    c: Coincident(g6,g-4)
    c: Coincident(g6,g7)
    c: Coincident(g7,g0)
    c: Vertical(g6)
    c: Horizontal(g5)
    c: Horizontal(g7)
    c: Equal(g0,g-3)
    c: Distance(g6,g6) = 1.6
    c: Vertical(g3)
    c: Horizontal(g4)
    c: Horizontal(g2)
    c: Equal(g-3,g1)
    c: Equal(g3,g6)
    c: Coincident(g8,g-5)
    c: Vertical(g8)
    c: Coincident(g9,g-6)
    c: PointOnObject(g9,g-4)
    c: Equal(g9,g8)
    c: Distance(g9,g9) = 0.1
    c: Coincident(g10,g11)
    c: Coincident(g11,g12)
    c: Coincident(g12,g13)
    c: Coincident(g13,g10)
    c: Vertical(g10)
    c: Vertical(g12)
    c: Horizontal(g11)
    c: Horizontal(g13)
    c: Coincident(g10,g8)
    c: Coincident(g11,g9)
FEATURE [PartDesign::Pad] Pad031  label="CL0_Pad031"
  BaseFeature = -> Pad021
  Direction = (1,0,0)
  Length = 17.4
  Length2 = 10
  Midplane = true
  Placement = pos=(0,0,0) rot=(1,1,1;2.0944rad)
  Profile = -> Sketch063
  ReferenceAxis = -> Sketch063 [N_Axis]
  Refine = true
  Suppressed = false
  Type = 0
  expr: Length = dd.CL_BW
FEATURE [PartDesign::Pad] Pad032  label="CL0_Pad032"
  BaseFeature = -> Pad031
  Direction = (1,0,0)
  Length = 11.7
  Length2 = 10.3
  Placement = pos=(0,0,0) rot=(1,1,1;2.0944rad)
  Profile = -> Sketch063 [Edge4,Edge1,Edge3,Edge2,Edge12,Edge9,Edge11,Edge10]
  ReferenceAxis = -> Sketch063 [N_Axis]
  Refine = true
  Suppressed = false
  Type = 4
  expr: Length = dd.CL_BW / 2 + 3 mm
  expr: Length2 = dd.CL_BW / 2 + 1.6 mm
FEATURE [PartDesign::Body] Body018  label="ChainLink0T"
  AllowCompound = false
  Group = -> [Sketch040,Pad021,Sketch063,Binder012,Pad031,Pad032]
  Origin = -> Origin018
  Placement = pos=(0,-72.6064,0) rot=(0,0,1;0rad)
  Tip = -> Pad032
  expr: .Placement.Base.y = -dd.CD_Radius
FEATURE [PartDesign::SubShapeBinder] Binder015  label="CL2_Binder015_CL1"
  BindCopyOnChange = 0
  BindMode = 0
  ClaimChildren = false
  Context = -> Part001 [Body005.Binder015.]
  Fuse = false
  MakeFace = true
  OffsetFill = false
  OffsetIntersection = false
  OffsetJoinType = 0
  OffsetOpenResult = false
  PartialLoad = false
  Refine = true
  Relative = true
  Support = -> [Body004[Pad002.Face23]]
  _Version = 2
FEATURE [Sketcher::SketchObject] Sketch065  label="CL2_Sketch065"
  ArcFitTolerance = 1e-06
  AttachmentSupport = -> [Binder015]
  ExternalGeometry = -> [Binder015]
  FullyConstrained = true
  MakeInternals = false
  MapMode = 5
  Placement = pos=(-9.5,2.1e-15,-1.1e-15) rot=(0.57735,-0.57735,-0.57735;2.0944rad)
  sketch-geometry (12):
    g0: LineSegment [constr] StartX=2.4 StartY=11 StartZ=0 EndX=2.4 EndY=7.2 EndZ=0
    g1: LineSegment [constr] StartX=2.4 StartY=7.2 StartZ=0 EndX=6.17714 EndY=7.2 EndZ=0
    g2: LineSegment [constr] StartX=6.17714 StartY=7.2 StartZ=0 EndX=6.17714 EndY=11 EndZ=0
    g3: LineSegment [constr] StartX=6.17714 StartY=11 StartZ=0 EndX=2.4 EndY=11 EndZ=0
    g4: LineSegment StartX=6.17714 StartY=11.1 StartZ=0 EndX=2.4 EndY=11.1 EndZ=0
    g5: ArcOfCircle CenterX=2.4 CenterY=11 CenterZ=0 NormalX=0 NormalY=0 NormalZ=-1 AngleXU=-1.5708 Radius=0.1 StartAngle=1.5708 EndAngle=3.14159
    g6: LineSegment StartX=2.3 StartY=11 StartZ=0 EndX=2.3 EndY=7.2 EndZ=0
    g7: ArcOfCircle CenterX=2.4 CenterY=7.2 CenterZ=0 NormalX=0 NormalY=0 NormalZ=-1 AngleXU=-3.14159 Radius=0.1 StartAngle=1.5708 EndAngle=3.14159
    g8: LineSegment StartX=2.4 StartY=7.1 StartZ=0 EndX=6.17714 EndY=7.1 EndZ=0
    g9: ArcOfCircle CenterX=6.17714 CenterY=7.2 CenterZ=0 NormalX=0 NormalY=0 NormalZ=-1 AngleXU=1.5708 Radius=0.1 StartAngle=1.5708 EndAngle=3.14159
    g10: LineSegment StartX=6.27714 StartY=7.2 StartZ=0 EndX=6.27714 EndY=11 EndZ=0
    g11: ArcOfCircle CenterX=6.17714 CenterY=11 CenterZ=0 NormalX=0 NormalY=0 NormalZ=-1 AngleXU=0 Radius=0.1 StartAngle=1.5708 EndAngle=3.14159
  constraints (26):
    c: Coincident(g0,g1)
    c: Coincident(g1,g2)
    c: Coincident(g2,g3)
    c: Coincident(g3,g0)
    c: Vertical(g0)
    c: Vertical(g2)
    c: Horizontal(g1)
    c: Horizontal(g3)
    c: Coincident(g0,g-3)
    c: Coincident(g-4,g1)
    c: Tangent(g4,g5) = -1.5708
    c: Tangent(g4,g11) = -1.5708
    c: Tangent(g5,g6) = -1.5708
    c: Tangent(g6,g7) = -1.5708
    c: Tangent(g7,g8) = -1.5708
    c: Tangent(g8,g9) = -1.5708
    c: Tangent(g9,g10) = -1.5708
    c: Tangent(g10,g11) = -1.5708
    c: Coincident(g11,g2)
    c: Parallel(g4,g3)
    c: Coincident(g5,g0)
    c: Parallel(g6,g0)
    c: Coincident(g7,g0)
    c: Parallel(g8,g1)
    c: Coincident(g9,g1)
    c: Distance(g10,g2) = 0.1
FEATURE [PartDesign::Pocket] Pocket  label="CL2_Pocket"
  BaseFeature = -> Pad004
  Direction = (1,0,0)
  Length = 5
  Length2 = 5
  Placement = pos=(0,0,0) rot=(1,1,1;2.0944rad)
  Profile = -> Sketch065
  ReferenceAxis = -> Sketch065 [N_Axis]
  Refine = true
  Suppressed = false
  Type = 1
FEATURE [PartDesign::Body] Body005  label="ChainLink2"
  AllowCompound = false
  Group = -> [Sketch004,Pad003,Sketch005,Pad004,Binder015,Sketch065,Pocket]
  Origin = -> Origin004
  Placement = pos=(0,-72.6064,0) rot=(1,0,0;0rad)
  Tip = -> Pocket
  expr: .Placement.Base.y = -dd.CD_Radius
  expr: .Placement.Rotation.Angle = <<ChainLink1>>.Placement.Rotation.Angle
FEATURE [PartDesign::SubShapeBinder] Binder016  label="CLB_Binder016_CL1"
  BindCopyOnChange = 0
  BindMode = 0
  ClaimChildren = false
  Context = -> Part001 [Body024.Binder016.]
  Fuse = false
  MakeFace = true
  OffsetFill = false
  OffsetIntersection = false
  OffsetJoinType = 0
  OffsetOpenResult = false
  PartialLoad = false
  Refine = true
  Relative = true
  Support = -> [Body004[Pad002.Face23]]
  _Version = 2
FEATURE [Sketcher::SketchObject] Sketch064  label="CLB_Sketch064"
  ArcFitTolerance = 1e-06
  AttachmentSupport = -> [YZ_Plane021]
  ExternalGeometry = -> [Binder016]
  FullyConstrained = true
  MakeInternals = false
  MapMode = 5
  Placement = pos=(0,0,0) rot=(0.57735,0.57735,0.57735;2.0944rad)
  sketch-geometry (22):
    g0: LineSegment StartX=-4.95306 StartY=6.25397 StartZ=0 EndX=-2.46759 EndY=7.1054 EndZ=0
    g1: ArcOfCircle CenterX=-2.5 CenterY=7.2 CenterZ=0 NormalX=0 NormalY=0 NormalZ=-1 AngleXU=1.5708 Radius=0.1 StartAngle=1.5708 EndAngle=2.81156
    g2: LineSegment StartX=-2.4 StartY=7.2 StartZ=0 EndX=-2.4 EndY=11 EndZ=0
    g3: ArcOfCircle CenterX=-2.5 CenterY=11 CenterZ=0 NormalX=0 NormalY=0 NormalZ=-1 AngleXU=0 Radius=0.1 StartAngle=1.90083 EndAngle=3.14159
    g4: LineSegment StartX=-2.46759 StartY=11.0946 StartZ=0 EndX=-4.95306 EndY=11.946 EndZ=0
    g5: ArcOfCircle CenterX=-5.27714 CenterY=11 CenterZ=0 NormalX=0 NormalY=0 NormalZ=-1 AngleXU=-1.5708 Radius=1 StartAngle=1.5708 EndAngle=3.47163
    g6: LineSegment StartX=-6.27714 StartY=11 StartZ=0 EndX=-6.27714 EndY=7.2 EndZ=0
    g7: ArcOfCircle CenterX=-5.27714 CenterY=7.2 CenterZ=0 NormalX=0 NormalY=0 NormalZ=-1 AngleXU=-3.14159 Radius=1 StartAngle=1.24076 EndAngle=3.14159
    g8: LineSegment StartX=-4.2938 StartY=5.21135 StartZ=0 EndX=-2.60833 EndY=5.78873 EndZ=0
    g9: ArcOfCircle CenterX=-3.09178 CenterY=7.2 CenterZ=0 NormalX=0 NormalY=0 NormalZ=-1 AngleXU=1.5708 Radius=1.49178 StartAngle=1.5708 EndAngle=2.81156
    g10: LineSegment StartX=-1.6 StartY=7.2 StartZ=0 EndX=-1.6 EndY=11 EndZ=0
    g11: ArcOfCircle CenterX=-3.09178 CenterY=11 CenterZ=0 NormalX=0 NormalY=0 NormalZ=-1 AngleXU=0 Radius=1.49178 StartAngle=1.90083 EndAngle=3.14159
    g12: LineSegment StartX=-2.60833 StartY=12.4113 StartZ=0 EndX=-4.2938 EndY=12.9887 EndZ=0
    g13: ArcOfCircle CenterX=-4.97504 CenterY=11 CenterZ=0 NormalX=0 NormalY=0 NormalZ=-1 AngleXU=-1.5708 Radius=2.1021 StartAngle=1.5708 EndAngle=3.47163
    g14: LineSegment StartX=-7.07714 StartY=11 StartZ=0 EndX=-7.07714 EndY=7.2 EndZ=0
    g15: ArcOfCircle CenterX=-4.97504 CenterY=7.2 CenterZ=0 NormalX=0 NormalY=0 NormalZ=-1 AngleXU=-3.14159 Radius=2.1021 StartAngle=1.24076 EndAngle=3.14159
    g16: LineSegment [constr] StartX=-7.07714 StartY=11 StartZ=0 EndX=-6.27714 EndY=11 EndZ=0
    g17: LineSegment [constr] StartX=-2.4 StartY=7.2 StartZ=0 EndX=-1.6 EndY=7.2 EndZ=0
    g18: LineSegment [constr] StartX=-2.4 StartY=9.1 StartZ=0 EndX=-6.17714 EndY=9.1 EndZ=0
    g19: LineSegment [constr] StartX=-6.17714 StartY=7.2 StartZ=0 EndX=-6.27714 EndY=7.2 EndZ=0
    g20: LineSegment [constr] StartX=-2.60833 StartY=12.4113 StartZ=0 EndX=-2.99722 EndY=11.276 EndZ=0
    g21: LineSegment [constr] StartX=-2.60833 StartY=5.78873 StartZ=0 EndX=-2.99722 EndY=6.92397 EndZ=0
  constraints (49):
    c: Tangent(g0,g1) = -1.5708
    c: Tangent(g0,g7) = -1.5708
    c: Tangent(g1,g2) = -1.5708
    c: Tangent(g2,g3) = -1.5708
    c: Tangent(g3,g4) = -1.5708
    c: Tangent(g4,g5) = -1.5708
    c: Tangent(g5,g6) = -1.5708
    c: Tangent(g6,g7) = -1.5708
    c: Tangent(g8,g9) = -1.5708
    c: Tangent(g8,g15) = -1.5708
    c: Tangent(g9,g10) = -1.5708
    c: Tangent(g10,g11) = -1.5708
    c: Tangent(g11,g12) = -1.5708
    c: Tangent(g12,g13) = -1.5708
    c: Tangent(g13,g14) = -1.5708
    c: Tangent(g14,g15) = -1.5708
    c: Parallel(g4,g12)
    c: Parallel(g8,g0)
    c: Vertical(g6)
    c: Vertical(g14)
    c: DistanceX(g16,g16) = 0.8
    c: Coincident(g16,g13)
    c: Coincident(g5,g16)
    c: Coincident(g17,g1)
    c: Coincident(g17,g9)
    c: Equal(g17,g16)
    c: Coincident(g1,g-4)
    c: Coincident(g2,g-4)
    c: Horizontal(g16)
    c: Horizontal(g17)
    c: Symmetric(g2,g2,g18)
    c: Symmetric(g-3,g-3,g18)
    c: Symmetric(g11,g9,g18)
    c: Symmetric(g5,g7,g18)
    c: Vertical(g10)
    c: Radius(g3) = 0.1
    c: Radius(g7) = 1
    c: Coincident(g19,g-3)
    c: Coincident(g19,g6)
    c: Horizontal(g19)
    c: Distance(g19,g19) = 0.1
    c: Coincident(g20,g11)
    c: PointOnObject(g20,g4)
    c: Coincident(g21,g8)
    c: PointOnObject(g21,g0)
    c: Perpendicular(g8,g21)
    c: Perpendicular(g12,g20)
    c: Distance(g20) = 1.2
    c: Symmetric(g13,g15,g18)
FEATURE [PartDesign::Pad] Pad033  label="CLB_Pad033"
  Direction = (1,0,0)
  Length = 13.8
  Length2 = 10
  Midplane = true
  Placement = pos=(0,0,0) rot=(1,1,1;2.0944rad)
  Profile = -> Sketch064
  ReferenceAxis = -> Sketch064 [N_Axis]
  Refine = true
  Suppressed = false
  Type = 0
  expr: Length = dd.CL_BW - 3.6 mm
FEATURE [PartDesign::Body] Body024  label="ChainLinkBumper"
  AllowCompound = false
  Group = -> [Sketch064,Pad033,Binder016]
  Origin = -> Origin023
  Placement = pos=(0,-72.6064,0) rot=(0,0,1;0rad)
  Tip = -> Pad033
  expr: .Placement.Base.y = -dd.CD_Radius
FEATURE [PartDesign::Chamfer] Chamfer003  label="F1_Chamfer003"
  Angle = 45
  Base = -> Hole011 [Edge19,Edge8,Edge12,Edge155,Edge156]
  BaseFeature = -> Hole011
  ChamferType = 0
  FlipDirection = false
  Placement = pos=(0,0,0) rot=(1,0,0;1.5708rad)
  Refine = true
  Size = 1.99
  Size2 = 1
  SupportTransform = false
  Suppressed = false
  UseAllEdges = false
FEATURE [Sketcher::SketchObject] Sketch066  label="F1_Sketch066"
  ArcFitTolerance = 1e-06
  AttachmentOffset = pos=(0,0,-16.7) rot=(0,0,1;0rad)
  AttachmentSupport = -> [YZ_Plane012]
  ExternalGeometry = -> [Chamfer003]
  FullyConstrained = true
  MakeInternals = false
  MapMode = 5
  Placement = pos=(-16.7,0,0) rot=(0.57735,0.57735,0.57735;2.0944rad)
  expr: .AttachmentOffset.Base.z = -<<F1_Pad016>>.Length2 - 2 mm
  sketch-geometry (5):
    g0: ArcOfCircle CenterX=0 CenterY=0 CenterZ=0 NormalX=0 NormalY=0 NormalZ=1 AngleXU=0 Radius=34.8 StartAngle=5.60621 EndAngle=10.1018
    g1: LineSegment StartX=-27.1256 StartY=-21.8 StartZ=0 EndX=27.1256 EndY=-21.8 EndZ=0
    g2: LineSegment [constr] StartX=-28.6182 StartY=-25 StartZ=0 EndX=28.6182 EndY=-25 EndZ=0
    g3: LineSegment [constr] StartX=-27.1256 StartY=-21.8 StartZ=0 EndX=-27.1256 EndY=-25 EndZ=0
    g4: LineSegment [constr] StartX=-34.8 StartY=0 StartZ=0 EndX=-38 EndY=0 EndZ=0
  constraints (15):
    c: Coincident(g0,g-1)
    c: Coincident(g1,g0)
    c: Coincident(g1,g0)
    c: Horizontal(g1)
    c: Coincident(g2,g-3)
    c: Coincident(g2,g-3)
    c: Coincident(g3,g0)
    c: PointOnObject(g3,g2)
    c: Vertical(g3)
    c: Distance(g3,g3) = 3.2
    c: PointOnObject(g4,g0)
    c: PointOnObject(g4,g-3)
    c: Horizontal(g4)
    c: PointOnObject(g4,g-1)
    c: Equal(g4,g3)
FEATURE [PartDesign::Pocket] Pocket025  label="F1_Pocket025"
  BaseFeature = -> Chamfer003
  Direction = (-1,0,0)
  Length = 5
  Length2 = 5
  Placement = pos=(0,0,0) rot=(1,0,0;1.5708rad)
  Profile = -> Sketch066
  ReferenceAxis = -> Sketch066 [N_Axis]
  Refine = true
  Reversed = true
  Suppressed = false
  Type = 1
FEATURE [PartDesign::SubShapeBinder] Binder017  label="F1_Binder017"
  BindCopyOnChange = 0
  BindMode = 0
  ClaimChildren = false
  Context = -> Part001 [Body012.Binder017.]
  Fuse = false
  MakeFace = true
  OffsetFill = false
  OffsetIntersection = false
  OffsetJoinType = 0
  OffsetOpenResult = false
  PartialLoad = false
  Refine = true
  Relative = true
  Support = -> [Part[Part__Mirroring.Face21,Body023.Pad027.Face21]]
  _Version = 2
FEATURE [PartDesign::Pocket] Pocket026  label="F1_Pocket026"
  BaseFeature = -> Pocket025
  Direction = (1,0,3e-16)
  Length = 5
  Length2 = 5
  Placement = pos=(0,0,0) rot=(1,0,0;1.5708rad)
  Profile = -> Binder017
  Refine = true
  Reversed = true
  Suppressed = false
  Type = 1
FEATURE [Part::Feature] Body026  label="F1_I"
  Placement = pos=(61.4,0,0) rot=(0,0,1;3.14159rad)
  shape: bbox 25.24 x 204 x 165.4 mm, 156 faces (baked)
  expr: .Placement.Base.x = -2 * dd.D1_X
FEATURE [Sketcher::SketchObject] Sketch067  label="FB_Sketch067"
  ArcFitTolerance = 1e-06
  AttachmentSupport = -> [YZ_Plane022]
  FullyConstrained = true
  MakeInternals = false
  MapMode = 5
  Placement = pos=(0,0,0) rot=(0.57735,0.57735,0.57735;2.0944rad)
  expr: Constraints[10] = dd.FR_H / 2 + dd.R2_Z
  expr: Constraints[11] = -dd.R2_Y
  expr: Constraints[12] = dd.R1_Y
  expr: Constraints[44] = dd.FR_H / 2
  expr: Constraints[7] = dd.FR_W
  sketch-geometry (17):
    g0: LineSegment StartX=-102 StartY=0 StartZ=0 EndX=-102 EndY=-0.8 EndZ=0
    g1: LineSegment StartX=-102 StartY=-0.8 StartZ=0 EndX=102 EndY=-0.8 EndZ=0
    g2: LineSegment StartX=102 StartY=-0.8 StartZ=0 EndX=102 EndY=0 EndZ=0
    g3: LineSegment [constr] StartX=-89.4064 StartY=12.0022 StartZ=0 EndX=-56.6064 EndY=12.0022 EndZ=0
    g4: ArcOfCircle CenterX=-89.4064 CenterY=12.0022 CenterZ=0 NormalX=0 NormalY=0 NormalZ=1 AngleXU=0 Radius=12.0022 StartAngle=3.69772 EndAngle=4.71239
    g5: ArcOfCircle CenterX=-56.6064 CenterY=12.0022 CenterZ=0 NormalX=0 NormalY=0 NormalZ=1 AngleXU=0 Radius=12.0022 StartAngle=4.71239 EndAngle=6.01311
    g6: LineSegment StartX=-89.4064 StartY=0 StartZ=0 EndX=-56.6064 EndY=0 EndZ=0
    g7: LineSegment StartX=-102 StartY=0 StartZ=0 EndX=-102 EndY=5.66623 EndZ=0
    g8: LineSegment StartX=-102 StartY=5.66623 StartZ=0 EndX=-99.6 EndY=5.66623 EndZ=0
    g9: LineSegment StartX=-37.1477 StartY=8.8 StartZ=0 EndX=-45.0393 EndY=8.8 EndZ=0
    g10: ArcOfCircle CenterX=89.4064 CenterY=12.0022 CenterZ=0 NormalX=0 NormalY=0 NormalZ=1 AngleXU=0 Radius=12.0022 StartAngle=4.71239 EndAngle=5.72706
    g11: ArcOfCircle CenterX=56.6064 CenterY=12.0022 CenterZ=0 NormalX=0 NormalY=0 NormalZ=1 AngleXU=0 Radius=12.0022 StartAngle=3.41167 EndAngle=4.71239
    g12: LineSegment StartX=89.4064 StartY=0 StartZ=0 EndX=56.6064 EndY=0 EndZ=0
    g13: LineSegment StartX=102 StartY=0 StartZ=0 EndX=102 EndY=5.66623 EndZ=0
    g14: LineSegment StartX=102 StartY=5.66623 StartZ=0 EndX=99.6 EndY=5.66623 EndZ=0
    g15: LineSegment StartX=37.1477 StartY=8.8 StartZ=0 EndX=45.0393 EndY=8.8 EndZ=0
    g16: ArcOfCircle CenterX=0 CenterY=82.8064 CenterZ=0 NormalX=0 NormalY=0 NormalZ=1 AngleXU=0 Radius=82.8064 StartAngle=4.24718 EndAngle=5.1776
  constraints (47):
    c: PointOnObject(g0,g-1)
    c: Vertical(g0)
    c: Coincident(g0,g1)
    c: Coincident(g1,g2)
    c: PointOnObject(g2,g-1)
    c: Vertical(g2)
    c: Symmetric(g1,g0,g-2)
    c: DistanceX(g1,g1) = 204
    c: Distance(g0,g-1) = 0.8
    c: Horizontal(g3)
    c: Distance(g3,g-1) = 12.0022
    c: Distance(g3,g-2) = 56.6064
    c: Distance(g3,g-2) = 89.4064
    c: Coincident(g4,g3)
    c: PointOnObject(g4,g-1)
    c: Coincident(g5,g3)
    c: PointOnObject(g5,g-1)
    c: Tangent(g6,g5) = -1.5708
    c: Tangent(g6,g4) = -1.5708
    c: Coincident(g7,g0)
    c: Vertical(g7)
    c: Coincident(g8,g7)
    c: Coincident(g8,g4)
    c: Horizontal(g8)
    c: Distance(g8,g8) = 2.4
    c: Coincident(g9,g5)
    c: Horizontal(g9)
    c: Equal(g4,g10)
    c: Symmetric(g4,g10,g-2)
    c: Symmetric(g4,g10,g-2)
    c: Equal(g5,g11)
    c: Symmetric(g5,g11,g-2)
    c: Symmetric(g5,g11,g-2)
    c: Symmetric(g6,g12,g-2)
    c: Symmetric(g6,g12,g-2)
    c: Symmetric(g7,g13,g-2)
    c: Symmetric(g7,g13,g-2)
    c: Symmetric(g8,g14,g-2)
    c: Symmetric(g8,g14,g-2)
    c: Symmetric(g9,g15,g-2)
    c: PointOnObject(g16,g-2)
    c: Coincident(g16,g9)
    c: Coincident(g16,g15)
    c: PointOnObject(g-1,g16)
    c: Radius(g16) = 82.8064
    c: Horizontal(g15)
    c: Distance(g15,g-1) = 8.8
FEATURE [PartDesign::Pad] Pad034  label="FR_Pad034"
  Direction = (1,0,0)
  Length = 86.8
  Length2 = 10
  Midplane = true
  Placement = pos=(0,0,0) rot=(1,1,1;2.0944rad)
  Profile = -> Sketch067
  ReferenceAxis = -> Sketch067 [N_Axis]
  Refine = true
  Suppressed = false
  Type = 0
FEATURE [Sketcher::SketchObject] Sketch068  label="FR_Sketch068"
  ArcFitTolerance = 1e-06
  AttachmentSupport = -> [XY_Plane022]
  ExternalGeometry = -> [Pad034]
  FullyConstrained = true
  MakeInternals = false
  MapMode = 5
  expr: Constraints[28] = -dd.R2_Y + 9 mm
  expr: Constraints[29] = dd.R1_Y - 8.2 mm
  expr: Constraints[8] = 9.6 mm
  sketch-geometry (22):
    g0: LineSegment StartX=-9.6 StartY=-49.6 StartZ=0 EndX=-14.8 EndY=-49.6 EndZ=0
    g1: LineSegment StartX=-14.8 StartY=-102 StartZ=0 EndX=-9.6 EndY=-102 EndZ=0
    g2: LineSegment StartX=-9.6 StartY=-102 StartZ=0 EndX=-9.6 EndY=-49.6 EndZ=0
    g3: LineSegment StartX=14.8 StartY=102 StartZ=0 EndX=9.6 EndY=102 EndZ=0
    g4: LineSegment StartX=9.6 StartY=102 StartZ=0 EndX=9.6 EndY=49.6 EndZ=0
    g5: LineSegment StartX=9.6 StartY=49.6 StartZ=0 EndX=14.8 EndY=49.6 EndZ=0
    g6: LineSegment StartX=14.8 StartY=65.6064 StartZ=0 EndX=41.2 EndY=65.6064 EndZ=0
    g7: LineSegment StartX=41.2 StartY=65.6064 StartZ=0 EndX=41.2 EndY=81.2064 EndZ=0
    g8: LineSegment StartX=41.2 StartY=81.2064 StartZ=0 EndX=14.8 EndY=81.2064 EndZ=0
    g9: LineSegment StartX=14.8 StartY=81.2064 StartZ=0 EndX=14.8 EndY=65.6064 EndZ=0
    g10: LineSegment StartX=-41.2 StartY=-65.6064 StartZ=0 EndX=-41.2 EndY=-81.2064 EndZ=0
    g11: LineSegment StartX=-41.2 StartY=-81.2064 StartZ=0 EndX=-14.8 EndY=-81.2064 EndZ=0
    g12: LineSegment StartX=-14.8 StartY=-81.2064 StartZ=0 EndX=-14.8 EndY=-65.6064 EndZ=0
    g13: LineSegment StartX=-14.8 StartY=-65.6064 StartZ=0 EndX=-41.2 EndY=-65.6064 EndZ=0
    g14: LineSegment StartX=-14.8 StartY=-81.2064 StartZ=0 EndX=-14.8 EndY=-102 EndZ=0
    g15: LineSegment StartX=-14.8 StartY=-49.6 StartZ=0 EndX=-14.8 EndY=-65.6064 EndZ=0
    g16: LineSegment StartX=14.8 StartY=81.2064 StartZ=0 EndX=14.8 EndY=102 EndZ=0
    g17: LineSegment StartX=14.8 StartY=49.6 StartZ=0 EndX=14.8 EndY=65.6064 EndZ=0
    g18: LineSegment StartX=-9.3 StartY=3.1 StartZ=0 EndX=-9.3 EndY=-3.1 EndZ=0
    g19: LineSegment StartX=-9.3 StartY=-3.1 StartZ=0 EndX=9.3 EndY=-3.1 EndZ=0
    g20: LineSegment StartX=9.3 StartY=-3.1 StartZ=0 EndX=9.3 EndY=3.1 EndZ=0
    g21: LineSegment StartX=9.3 StartY=3.1 StartZ=0 EndX=-9.3 EndY=3.1 EndZ=0
  constraints (59):
    c: Coincident(g0,g15)
    c: Coincident(g14,g1)
    c: Coincident(g1,g2)
    c: Coincident(g2,g0)
    c: Horizontal(g0)
    c: Horizontal(g1)
    c: Vertical(g2)
    c: PointOnObject(g14,g-3)
    c: Distance(g1,g-2) = 9.6
    c: Distance(g0,g0) = 5.2
    c: DistanceY(g14,g15) = 52.4
    c: Coincident(g3,g4)
    c: Coincident(g4,g5)
    c: Coincident(g5,g17)
    c: Coincident(g16,g3)
    c: Horizontal(g3)
    c: Horizontal(g5)
    c: Vertical(g4)
    c: Symmetric(g3,g14,g-1)
    c: Symmetric(g0,g4,g-1)
    c: Coincident(g6,g7)
    c: Coincident(g7,g8)
    c: Coincident(g8,g9)
    c: Coincident(g9,g6)
    c: Horizontal(g6)
    c: Horizontal(g8)
    c: Vertical(g7)
    c: Vertical(g9)
    c: DistanceY(g-1,g6) = 65.6064
    c: DistanceY(g-1,g7) = 81.2064
    c: Coincident(g10,g11)
    c: Coincident(g11,g12)
    c: Coincident(g12,g13)
    c: Coincident(g13,g10)
    c: Vertical(g10)
    c: Horizontal(g11)
    c: Horizontal(g13)
    c: Symmetric(g10,g7,g-1)
    c: Symmetric(g12,g6,g-1)
    c: DistanceX(g-3,g10) = 2.2
    c: Coincident(g15,g12)
    c: Coincident(g14,g11)
    c: Coincident(g16,g8)
    c: Coincident(g17,g6)
    c: Vertical(g15)
    c: Vertical(g14)
    c: Vertical(g17)
    c: Vertical(g16)
    c: Coincident(g18,g19)
    c: Coincident(g19,g20)
    c: Coincident(g20,g21)
    c: Coincident(g21,g18)
    c: Vertical(g18)
    c: Vertical(g20)
    c: Horizontal(g19)
    c: Horizontal(g21)
    c: Symmetric(g20,g18,g-1)
    c: DistanceX(g21,g21) = 18.6
    c: DistanceY(g18,g18) = 6.2
FEATURE [Sketcher::SketchObject] Sketch069  label="FR_Sketch069"
  ArcFitTolerance = 1e-06
  AttachmentSupport = -> [XY_Plane022]
  FullyConstrained = true
  MakeInternals = false
  MapMode = 5
  sketch-geometry (6):
    g0: LineSegment StartX=-47.4 StartY=102 StartZ=0 EndX=-47.4 EndY=-102 EndZ=0
    g1: LineSegment StartX=-47.4 StartY=-102 StartZ=0 EndX=47.4 EndY=-102 EndZ=0
    g2: LineSegment StartX=47.4 StartY=-102 StartZ=0 EndX=47.4 EndY=102 EndZ=0
    g3: LineSegment StartX=47.4 StartY=102 StartZ=0 EndX=-47.4 EndY=102 EndZ=0
    g4: LineSegment [constr] StartX=-43.4 StartY=102 StartZ=0 EndX=-47.4 EndY=102 EndZ=0
    g5: LineSegment [constr] StartX=43.4 StartY=-102 StartZ=0 EndX=47.4 EndY=-102 EndZ=0
  constraints (16):
    c: Coincident(g0,g1)
    c: Coincident(g1,g2)
    c: Coincident(g2,g3)
    c: Coincident(g3,g0)
    c: Vertical(g0)
    c: Vertical(g2)
    c: Horizontal(g1)
    c: Horizontal(g3)
    c: Coincident(g4,g-4)
    c: Coincident(g4,g0)
    c: Coincident(g5,g-3)
    c: Coincident(g5,g1)
    c: DistanceX(g5,g5) = 4
    c: Equal(g5,g4)
    c: Horizontal(g4)
    c: Horizontal(g5)
FEATURE [PartDesign::Pad] Pad035  label="FR_Pad035"
  BaseFeature = -> Pad034
  Direction = (0,0,1)
  Length = 0.8
  Length2 = 10
  Placement = pos=(0,0,0) rot=(1,1,1;2.0944rad)
  Profile = -> Sketch069
  ReferenceAxis = -> Sketch069 [N_Axis]
  Refine = true
  Reversed = true
  Suppressed = false
  Type = 0
FEATURE [PartDesign::Pocket] Pocket027  label="FR_Pocket027"
  BaseFeature = -> Pad035
  Direction = (0,0,-1)
  Length = 5
  Length2 = 5
  Placement = pos=(0,0,0) rot=(1,1,1;2.0944rad)
  Profile = -> Sketch068 [Edge5,Edge6,Edge4,Edge2,Edge7,Edge8,Edge1,Edge9,Edge10,Edge11,Edge18,Edge17,Edge16,Edge15,Edge13,Edge12]
  ReferenceAxis = -> Sketch068 [N_Axis]
  Refine = true
  Reversed = true
  Suppressed = false
  Type = 1
FEATURE [PartDesign::Pocket] Pocket028  label="FR_Pocket028"
  BaseFeature = -> Pocket027
  Direction = (0,0,-1)
  Length = 5
  Length2 = 5
  Placement = pos=(0,0,0) rot=(1,1,1;2.0944rad)
  Profile = -> Sketch068 [Edge5,Edge4,Edge3,Edge6,Edge15,Edge14,Edge17,Edge16]
  ReferenceAxis = -> Sketch068 [N_Axis]
  Refine = true
  Suppressed = false
  Type = 1
FEATURE [Sketcher::SketchObject] Sketch070  label="FR_Sketch070"
  ArcFitTolerance = 1e-06
  AttachmentSupport = -> [Pocket028]
  ExternalGeometry = -> [Pocket028]
  FullyConstrained = true
  MakeInternals = false
  MapMode = 5
  Placement = pos=(43.4,0,0) rot=(0.57735,0.57735,0.57735;2.0944rad)
  sketch-geometry (4):
    g0: LineSegment [constr] StartX=-41.0935 StartY=8.8 StartZ=0 EndX=-41.0935 EndY=4 EndZ=0
    g1: LineSegment [constr] StartX=-41.0935 StartY=4 StartZ=0 EndX=-41.0935 EndY=-0.8 EndZ=0
    g2: Circle CenterX=-41.0935 CenterY=4 CenterZ=0 NormalX=0 NormalY=0 NormalZ=1 AngleXU=0 Radius=1.6
    g3: Circle CenterX=41.0935 CenterY=4 CenterZ=0 NormalX=0 NormalY=0 NormalZ=1 AngleXU=0 Radius=1.6
  constraints (10):
    c: Symmetric(g-3,g-3,g0)
    c: Vertical(g0)
    c: Coincident(g1,g0)
    c: PointOnObject(g1,g-4)
    c: Vertical(g1)
    c: Equal(g1,g0)
    c: Coincident(g2,g0)
    c: Equal(g3,g2)
    c: Symmetric(g0,g3,g-2)
    c: Diameter(g3) = 3.2
FEATURE [PartDesign::Pocket] Pocket029  label="FR_Pocket029"
  BaseFeature = -> Pocket028
  Direction = (-1,0,0)
  Length = 10
  Length2 = 5
  Placement = pos=(0,0,0) rot=(1,1,1;2.0944rad)
  Profile = -> Sketch070
  ReferenceAxis = -> Sketch070 [N_Axis]
  Refine = true
  Suppressed = false
  Type = 0
FEATURE [Sketcher::SketchObject] Sketch071  label="FR_Sketch071"
  ArcFitTolerance = 1e-06
  AttachmentOffset = pos=(0,0,-4) rot=(0,0,1;0rad)
  AttachmentSupport = -> [Pocket029]
  ExternalGeometry = -> [Pocket029]
  FullyConstrained = true
  MakeInternals = false
  MapMode = 5
  Placement = pos=(39.4,0,0) rot=(0.57735,0.57735,0.57735;2.0944rad)
  sketch-geometry (20):
    g0: LineSegment [constr] StartX=-37.8603 StartY=4 StartZ=0 EndX=-39.4769 EndY=6.8 EndZ=0
    g1: LineSegment [constr] StartX=-39.4769 StartY=6.8 StartZ=0 EndX=-42.7101 EndY=6.8 EndZ=0
    g2: LineSegment [constr] StartX=-42.7101 StartY=6.8 StartZ=0 EndX=-44.3267 EndY=4 EndZ=0
    g3: LineSegment StartX=-44.3267 StartY=4 StartZ=0 EndX=-42.7101 EndY=1.2 EndZ=0
    g4: LineSegment StartX=-42.7101 StartY=1.2 StartZ=0 EndX=-39.4769 EndY=1.2 EndZ=0
    g5: LineSegment StartX=-39.4769 StartY=1.2 StartZ=0 EndX=-37.8603 EndY=4 EndZ=0
    g6: Circle [constr] CenterX=-41.0935 CenterY=4 CenterZ=0 NormalX=0 NormalY=0 NormalZ=1 AngleXU=0 Radius=3.23316
    g7: LineSegment StartX=37.8603 StartY=4 StartZ=0 EndX=39.4769 EndY=1.2 EndZ=0
    g8: LineSegment StartX=39.4769 StartY=1.2 StartZ=0 EndX=42.7101 EndY=1.2 EndZ=0
    g9: LineSegment StartX=42.7101 StartY=1.2 StartZ=0 EndX=44.3267 EndY=4 EndZ=0
    g10: LineSegment [constr] StartX=44.3267 StartY=4 StartZ=0 EndX=42.7101 EndY=6.8 EndZ=0
    g11: LineSegment [constr] StartX=42.7101 StartY=6.8 StartZ=0 EndX=39.4769 EndY=6.8 EndZ=0
    g12: LineSegment [constr] StartX=39.4769 StartY=6.8 StartZ=0 EndX=37.8603 EndY=4 EndZ=0
    g13: Circle [constr] CenterX=41.0935 CenterY=4 CenterZ=0 NormalX=0 NormalY=0 NormalZ=1 AngleXU=0 Radius=3.23316
    g14: LineSegment StartX=-44.3267 StartY=4 StartZ=0 EndX=-44.3267 EndY=8.8 EndZ=0
    g15: LineSegment StartX=-44.3267 StartY=8.8 StartZ=0 EndX=-37.8603 EndY=8.8 EndZ=0
    g16: LineSegment StartX=-37.8603 StartY=8.8 StartZ=0 EndX=-37.8603 EndY=4 EndZ=0
    g17: LineSegment StartX=37.8603 StartY=4 StartZ=0 EndX=37.8603 EndY=8.8 EndZ=0
    g18: LineSegment StartX=37.8603 StartY=8.8 StartZ=0 EndX=44.3267 EndY=8.8 EndZ=0
    g19: LineSegment StartX=44.3267 StartY=8.8 StartZ=0 EndX=44.3267 EndY=4 EndZ=0
  constraints (48):
    c: Coincident(g0,g1)
    c: Coincident(g1,g2)
    c: Coincident(g2,g3)
    c: Coincident(g3,g4)
    c: Coincident(g4,g5)
    c: Coincident(g5,g0)
    c: Equal(g0, g1-g5) x5
    c: PointOnObject(g0,g6)
    c: PointOnObject(g1,g6)
    c: PointOnObject(g2,g6)
    c: PointOnObject(g3,g6)
    c: PointOnObject(g4,g6)
    c: PointOnObject(g5,g6)
    c: Coincident(g6,g-3)
    c: Coincident(g7,g8)
    c: Coincident(g8,g9)
    c: Coincident(g9,g10)
    c: Coincident(g10,g11)
    c: Coincident(g11,g12)
    c: Coincident(g12,g7)
    c: Equal(g7, g8-g12) x5
    c: PointOnObject(g7,g13)
    c: PointOnObject(g8,g13)
    c: PointOnObject(g9,g13)
    c: PointOnObject(g10,g13)
    c: PointOnObject(g11,g13)
    c: PointOnObject(g12,g13)
    c: Equal(g13,g6)
    c: Horizontal(g4)
    c: Horizontal(g8)
    c: Coincident(g13,g-4)
    c: Distance(g3,g1) = 5.6
    c: Coincident(g2,g14)
    c: Vertical(g14)
    c: Coincident(g15,g16)
    c: Coincident(g16,g0)
    c: Vertical(g16)
    c: Coincident(g7,g17)
    c: Vertical(g17)
    c: Coincident(g18,g19)
    c: Coincident(g19,g9)
    c: Vertical(g19)
    c: Coincident(g14,g15)
    c: PointOnObject(g15,g-6)
    c: Coincident(g17,g18)
    c: PointOnObject(g18,g-5)
    c: Horizontal(g18)
    c: Horizontal(g15)
FEATURE [PartDesign::Pocket] Pocket030  label="FR_Pocket030"
  BaseFeature = -> Pocket029
  Direction = (-1,1e-15,1e-16)
  Length = 2.4
  Length2 = 5
  Placement = pos=(0,0,0) rot=(1,1,1;2.0944rad)
  Profile = -> Sketch071
  ReferenceAxis = -> Sketch071 [N_Axis]
  Refine = true
  Suppressed = false
  Type = 0
FEATURE [PartDesign::Mirrored] Mirrored001  label="FR_Mirrored001"
  BaseFeature = -> Pocket030
  MirrorPlane = -> YZ_Plane022
  Originals = -> [Pocket030,Pocket029]
  Placement = pos=(0,0,0) rot=(1,1,1;2.0944rad)
  Refine = true
  Suppressed = false
  TransformMode = 0
FEATURE [Sketcher::SketchObject] Sketch074  label="FR_Sketch074"
  ArcFitTolerance = 1e-06
  AttachmentOffset = pos=(0,0,-0.8) rot=(0,0,1;0rad)
  AttachmentSupport = -> [XY_Plane022]
  ExternalGeometry = -> [Mirrored001]
  FullyConstrained = true
  MakeInternals = false
  MapMode = 5
  Placement = pos=(0,0,-0.8) rot=(0,0,1;0rad)
  sketch-geometry (7):
    g0: LineSegment StartX=-9.6 StartY=-102 StartZ=0 EndX=9.6 EndY=-102 EndZ=0
    g1: LineSegment StartX=9.6 StartY=-102 StartZ=0 EndX=9.6 EndY=-82 EndZ=0
    g2: LineSegment StartX=9.6 StartY=-82 StartZ=0 EndX=-9.6 EndY=-82 EndZ=0
    g3: LineSegment StartX=-9.6 StartY=-82 StartZ=0 EndX=-9.6 EndY=-102 EndZ=0
    g4: LineSegment [constr] StartX=9.6 StartY=-92 StartZ=0 EndX=2.6 EndY=-92 EndZ=0
    g5: LineSegment [constr] StartX=2.6 StartY=-92 StartZ=0 EndX=-4.4 EndY=-92 EndZ=0
    g6: Circle CenterX=2.6 CenterY=-92 CenterZ=0 NormalX=0 NormalY=0 NormalZ=1 AngleXU=0 Radius=2.1
  constraints (18):
    c: Coincident(g0,g1)
    c: Coincident(g1,g2)
    c: Coincident(g2,g3)
    c: Coincident(g3,g0)
    c: Horizontal(g0)
    c: Vertical(g1)
    c: Vertical(g3)
    c: Coincident(g0,g-3)
    c: Symmetric(g2,g1,g-2)
    c: Horizontal(g4)
    c: Coincident(g5,g4)
    c: Horizontal(g5)
    c: Equal(g5,g4)
    c: DistanceX(g-4,g5) = 43
    c: Coincident(g6,g4)
    c: Diameter(g6) = 4.2
    c: DistanceY(g3,g3) = 20
    c: Symmetric(g1,g0,g4)
FEATURE [PartDesign::Pad] Pad036  label="FR_Pad036"
  BaseFeature = -> Mirrored001
  Direction = (0,0,1)
  Length = 29.0064
  Length2 = 10
  Placement = pos=(0,0,0) rot=(1,1,1;2.0944rad)
  Profile = -> Sketch074
  ReferenceAxis = -> Sketch074 [N_Axis]
  Refine = true
  Suppressed = false
  Type = 0
  expr: Length = dd.FR_H / 2 + dd.CG_Z - 28.8 mm
FEATURE [Sketcher::SketchObject] Sketch075  label="FR_Sketch075"
  ArcFitTolerance = 1e-06
  AttachmentSupport = -> [Pad036]
  ExternalGeometry = -> [Pad036]
  FullyConstrained = true
  MakeInternals = false
  MapMode = 5
  Placement = pos=(0,0,28.2064) rot=(0,0,-1;1.5708rad)
  sketch-geometry (8):
    g0: LineSegment StartX=89 StartY=-9.6 StartZ=0 EndX=95 EndY=-9.6 EndZ=0
    g1: LineSegment StartX=95 StartY=-9.6 StartZ=0 EndX=95 EndY=-0.4 EndZ=0
    g2: LineSegment StartX=95 StartY=-0.4 StartZ=0 EndX=89 EndY=-0.4 EndZ=0
    g3: LineSegment StartX=89 StartY=-0.4 StartZ=0 EndX=89 EndY=-9.6 EndZ=0
    g4: LineSegment StartX=89 StartY=9.6 StartZ=0 EndX=89 EndY=5.6 EndZ=0
    g5: LineSegment StartX=89 StartY=5.6 StartZ=0 EndX=95 EndY=5.6 EndZ=0
    g6: LineSegment StartX=95 StartY=5.6 StartZ=0 EndX=95 EndY=9.6 EndZ=0
    g7: LineSegment StartX=95 StartY=9.6 StartZ=0 EndX=89 EndY=9.6 EndZ=0
  constraints (23):
    c: Coincident(g0,g1)
    c: Coincident(g1,g2)
    c: Coincident(g2,g3)
    c: Coincident(g3,g0)
    c: Horizontal(g0)
    c: Horizontal(g2)
    c: Vertical(g1)
    c: Vertical(g3)
    c: PointOnObject(g0,g-5)
    c: Coincident(g4,g5)
    c: Coincident(g5,g6)
    c: Coincident(g6,g7)
    c: Coincident(g7,g4)
    c: Vertical(g4)
    c: Vertical(g6)
    c: Horizontal(g5)
    c: Horizontal(g7)
    c: PointOnObject(g4,g-4)
    c: Equal(g7,g0)
    c: Symmetric(g4,g1,g-3)
    c: DistanceX(g7,g7) = 6
    c: PointOnObject(g2,g4)
    c: DistanceY(g2,g4) = 6
FEATURE [PartDesign::Pad] Pad037  label="FR_Pad037"
  BaseFeature = -> Pad036
  Direction = (0,0,1)
  Length = 1.6
  Length2 = 10
  Placement = pos=(0,0,0) rot=(1,1,1;2.0944rad)
  Profile = -> Sketch075
  ReferenceAxis = -> Sketch075 [N_Axis]
  Refine = true
  Suppressed = false
  Type = 0
FEATURE [Sketcher::SketchObject] Sketch073  label="FR_Sketch073"
  ArcFitTolerance = 1e-06
  ExternalGeometry = -> [Pad037]
  FullyConstrained = true
  MakeInternals = false
  MapMode = 5
  Placement = pos=(-9.6,2.1e-15,-1.1e-15) rot=(0.57735,0.57735,-0.57735;4.18879rad)
  expr: Constraints[5] = dd.R1_Y
  expr: Constraints[6] = dd.FR_H / 2 + dd.R2_Z
  sketch-geometry (6):
    g0: ArcOfCircle CenterX=-89.4064 CenterY=-12.0022 CenterZ=0 NormalX=0 NormalY=0 NormalZ=1 AngleXU=0 Radius=1.8 StartAngle=0 EndAngle=3.14159
    g1: LineSegment StartX=-91.2064 StartY=-12.0022 StartZ=0 EndX=-91.2064 EndY=-29.8064 EndZ=0
    g2: LineSegment StartX=-87.6064 StartY=-12.0022 StartZ=0 EndX=-87.6064 EndY=-28.2064 EndZ=0
    g3: LineSegment StartX=-91.2064 StartY=-29.8064 StartZ=0 EndX=-89 EndY=-29.8064 EndZ=0
    g4: LineSegment StartX=-89 StartY=-29.8064 StartZ=0 EndX=-89 EndY=-28.2064 EndZ=0
    g5: LineSegment StartX=-89 StartY=-28.2064 StartZ=0 EndX=-87.6064 EndY=-28.2064 EndZ=0
  constraints (15):
    c: Radius(g0) = 1.8
    c: Vertical(g2)
    c: Vertical(g1)
    c: Tangent(g0,g1) = -1.5708
    c: Tangent(g0,g2) = 1.5708
    c: Distance(g0,g-2) = 89.4064
    c: Distance(g0,g-1) = 12.0022
    c: Coincident(g1,g3)
    c: Coincident(g3,g4)
    c: Coincident(g4,g5)
    c: Coincident(g5,g2)
    c: Horizontal(g5)
    c: Horizontal(g3)
    c: Coincident(g4,g-3)
    c: Coincident(g-3,g3)
FEATURE [PartDesign::Pocket] Pocket031  label="FR_Pocket031"
  BaseFeature = -> Pad037
  Direction = (1,0,0)
  Length = 3.6
  Length2 = 5
  Placement = pos=(0,0,0) rot=(1,1,1;2.0944rad)
  Profile = -> Sketch073
  ReferenceAxis = -> Sketch073 [N_Axis]
  Refine = true
  Suppressed = false
  Type = 0
FEATURE [PartDesign::Hole] Hole012  label="FR_Hole012"
  BaseFeature = -> Pocket031
  CustomThreadClearance = 0
  Depth = 458.588
  DepthType = 1
  Diameter = 4.2
  DrillForDepth = false
  DrillPoint = 1
  DrillPointAngle = 118
  HoleCutCountersinkAngle = 178
  HoleCutCustomValues = false
  HoleCutDepth = 15
  HoleCutDiameter = 7.6
  HoleCutType = 3
  ModelThread = false
  Placement = pos=(0,0,0) rot=(1,1,1;2.0944rad)
  Profile = -> Sketch074 [Edge5]
  Refine = true
  Reversed = true
  Suppressed = false
  Tapered = false
  TaperedAngle = 90
  ThreadClass = 0
  ThreadDepth = 458.588
  ThreadDepthType = 0
  ThreadDirection = 0
  ThreadFit = 0
  ThreadSize = 0
  ThreadType = 0
  Threaded = false
  UseCustomThreadClearance = false
FEATURE [PartDesign::PolarPattern] PolarPattern002  label="FR_PolarPattern002"
  Angle = 360
  Axis = -> Z_Axis022
  BaseFeature = -> Hole012
  Mode = 0
  Occurrences = 2
  Offset = 120
  Originals = -> [Pad036,Pad037,Pocket031,Hole012]
  Placement = pos=(0,0,0) rot=(1,1,1;2.0944rad)
  Refine = true
  Suppressed = false
  TransformMode = 0
FEATURE [PartDesign::Hole] Hole013  label="F1_Hole013"
  BaseFeature = -> Pocket026
  CustomThreadClearance = 0
  Depth = 532.968
  DepthType = 1
  Diameter = 3.2
  DrillForDepth = false
  DrillPoint = 1
  DrillPointAngle = 118
  HoleCutCountersinkAngle = 178
  HoleCutCustomValues = false
  HoleCutDepth = 1.6
  HoleCutDiameter = 5.6
  HoleCutType = 3
  ModelThread = false
  Placement = pos=(0,0,0) rot=(1,0,0;1.5708rad)
  Profile = -> Sketch044 [Edge20,Edge19]
  Refine = true
  Reversed = true
  Suppressed = false
  Tapered = false
  TaperedAngle = 90
  ThreadClass = 0
  ThreadDepth = 532.968
  ThreadDepthType = 0
  ThreadDirection = 0
  ThreadFit = 0
  ThreadSize = 0
  ThreadType = 0
  Threaded = false
  UseCustomThreadClearance = false
FEATURE [PartDesign::Body] Body012  label="Frame1"
  AllowCompound = false
  Group = -> [Binder002,Sketch019,Revolution002,Sketch029,Pad016,Sketch030,Pocket013,Sketch044,Pad022,Binder007,Sketch057,Pad028,Hole009,Hole010,Hole011,Chamfer003,Sketch066,Pocket025,Binder017,Pocket026,Hole013]
  Origin = -> Origin012
  Tip = -> Hole013
FEATURE [Part::FeaturePython] Slice  # WARN: FeaturePython — macro-defined, semantics opaque (R4)
  Base = -> Body012
  Mode = 1
  Tolerance = 0
  Tools = -> [Cylinder]
FEATURE [Part::FeaturePython] Slice_child0  label="Slice.0"  # WARN: FeaturePython — macro-defined, semantics opaque (R4)
  Base = -> Slice
  FilterType = 1
  Invert = false
  OverrideMaxVal = 0
  WindowFrom = 80
  WindowTo = 100
  items = 0
FEATURE [Part::FeaturePython] Slice_child1  label="Slice.1"  # WARN: FeaturePython — macro-defined, semantics opaque (R4)
  Base = -> Slice
  FilterType = 1
  Invert = false
  OverrideMaxVal = 0
  WindowFrom = 80
  WindowTo = 100
  items = 1
FEATURE [App::DocumentObjectGroup] GrExplode_Slice  label="F1_Exploded Slice"
  Group = -> [Slice_child0,Slice_child1]
FEATURE [App::Part] Part001  label="Drum1"
  Group = -> [Body004,Body005,Body006,Body007,Body008,BevelGear,LanternGear,Body009,Body010,Fusion,Common,Body011,Body012,Cylinder,Body016,Body017,Body018,Body019,Body020,Body021,Tube,Body022,Body024,Slice,Slice_child0,Slice_child1,GrExplode_Slice,Body026]
  Origin = -> Origin001
  Placement = pos=(-30.7,0,0) rot=(0,0,1;0rad)
  expr: .Placement.Base.x = dd.D1_X
FEATURE [PartDesign::Pocket] Pocket032  label="FR_Pocket032"
  BaseFeature = -> PolarPattern002
  Direction = (0,0,-1)
  Length = 5
  Length2 = 5
  Midplane = true
  Placement = pos=(0,0,0) rot=(1,1,1;2.0944rad)
  Profile = -> Sketch068 [Edge19,Edge20,Edge21,Edge22]
  ReferenceAxis = -> Sketch068 [N_Axis]
  Refine = true
  Suppressed = false
  Type = 1
FEATURE [Sketcher::SketchObject] Sketch076  label="FR_Sketch076"
  ArcFitTolerance = 1e-06
  AttachmentSupport = -> [XY_Plane022]
  FullyConstrained = true
  MakeInternals = false
  MapMode = 5
  sketch-geometry (5):
    g0: LineSegment [constr] StartX=-7.5 StartY=-17.8 StartZ=0 EndX=7.5 EndY=-17.8 EndZ=0
    g1: ArcOfCircle CenterX=-7.5 CenterY=-17.8 CenterZ=0 NormalX=0 NormalY=0 NormalZ=1 AngleXU=0 Radius=3.2 StartAngle=1.5708 EndAngle=4.71239
    g2: ArcOfCircle CenterX=7.5 CenterY=-17.8 CenterZ=0 NormalX=0 NormalY=0 NormalZ=1 AngleXU=0 Radius=3.2 StartAngle=4.71239 EndAngle=7.85398
    g3: LineSegment StartX=-7.5 StartY=-14.6 StartZ=0 EndX=7.5 EndY=-14.6 EndZ=0
    g4: LineSegment StartX=-7.5 StartY=-21 StartZ=0 EndX=7.5 EndY=-21 EndZ=0
  constraints (11):
    c: Distance(g0,g-1) = 17.8
    c: DistanceX(g0,g0) = 15
    c: Symmetric(g0,g0,g-2)
    c: Tangent(g1,g3) = 1.5708
    c: Tangent(g1,g4) = -1.5708
    c: Tangent(g2,g3) = 1.5708
    c: Tangent(g2,g4) = -1.5708
    c: Equal(g1,g2)
    c: Coincident(g1,g0)
    c: Coincident(g2,g0)
    c: Radius(g2) = 3.2
FEATURE [PartDesign::Pad] Pad038  label="FR_Pad038"
  BaseFeature = -> Pocket032
  Direction = (0,0,1)
  Length = 14.2
  Length2 = 10
  Placement = pos=(0,0,0) rot=(1,1,1;2.0944rad)
  Profile = -> Sketch076
  ReferenceAxis = -> Sketch076 [N_Axis]
  Refine = true
  Suppressed = false
  Type = 0
FEATURE [Sketcher::SketchObject] Sketch077  label="FR_Sketch077"
  ArcFitTolerance = 1e-06
  AttachmentSupport = -> [Pad038]
  ExternalGeometry = -> [Pad038]
  FullyConstrained = true
  MakeInternals = false
  MapMode = 5
  Placement = pos=(0,0,14.2) rot=(0,0,-1;1.5708rad)
  sketch-geometry (6):
    g0: Circle CenterX=17.8 CenterY=7.5 CenterZ=0 NormalX=0 NormalY=0 NormalZ=1 AngleXU=0 Radius=0.8
    g1: Circle CenterX=17.8 CenterY=-7.5 CenterZ=0 NormalX=0 NormalY=0 NormalZ=1 AngleXU=0 Radius=0.8
    g2: LineSegment StartX=14.6 StartY=4 StartZ=0 EndX=14.6 EndY=-4 EndZ=0
    g3: LineSegment StartX=14.6 StartY=-4 StartZ=0 EndX=21 EndY=-4 EndZ=0
    g4: LineSegment StartX=21 StartY=-4 StartZ=0 EndX=21 EndY=4 EndZ=0
    g5: LineSegment StartX=21 StartY=4 StartZ=0 EndX=14.6 EndY=4 EndZ=0
  constraints (15):
    c: Coincident(g0,g-3)
    c: Coincident(g1,g-4)
    c: Equal(g0,g1)
    c: Diameter(g0) = 1.6
    c: Coincident(g2,g3)
    c: Coincident(g3,g4)
    c: Coincident(g4,g5)
    c: Coincident(g5,g2)
    c: Vertical(g2)
    c: Horizontal(g3)
    c: Horizontal(g5)
    c: Symmetric(g3,g4,g-1)
    c: PointOnObject(g-3,g4)
    c: PointOnObject(g-4,g2)
    c: DistanceY(g4,g4) = 8
FEATURE [PartDesign::Pocket] Pocket033  label="FR_Pocket033"
  BaseFeature = -> Pad038
  Direction = (0,0,-1)
  Length = 5.2
  Length2 = 5
  Placement = pos=(0,0,0) rot=(1,1,1;2.0944rad)
  Profile = -> Sketch077
  ReferenceAxis = -> Sketch077 [N_Axis]
  Refine = true
  Suppressed = false
  Type = 0
FEATURE [PartDesign::Hole] Hole014  label="FR_Hole014"
  BaseFeature = -> Pocket033
  CustomThreadClearance = 0
  Depth = 10
  DepthType = 0
  Diameter = 3
  DrillForDepth = false
  DrillPoint = 0
  DrillPointAngle = 118
  HoleCutCountersinkAngle = 90
  HoleCutCustomValues = false
  HoleCutDepth = 0
  HoleCutDiameter = 6.1
  HoleCutType = 0
  ModelThread = false
  Placement = pos=(0,0,0) rot=(1,1,1;2.0944rad)
  Profile = -> Sketch077 [Edge1,Edge2]
  Refine = true
  Suppressed = false
  Tapered = true
  TaperedAngle = 87
  ThreadClass = 0
  ThreadDepth = 10
  ThreadDepthType = 0
  ThreadDirection = 0
  ThreadFit = 0
  ThreadSize = 0
  ThreadType = 0
  Threaded = false
  UseCustomThreadClearance = false
FEATURE [Sketcher::SketchObject] Sketch078  label="FB_Sketch078"
  ArcFitTolerance = 1e-06
  AttachmentSupport = -> [XY_Plane022]
  ExternalGeometry = -> [Hole014]
  FullyConstrained = true
  MakeInternals = false
  MapMode = 5
  expr: Constraints[5] = dd.CD_Radius
  sketch-geometry (18):
    g0: LineSegment [constr] StartX=0 StartY=-72.6064 StartZ=0 EndX=-47.4 EndY=-72.6064 EndZ=0
    g1: LineSegment [constr] StartX=0 StartY=72.6064 StartZ=0 EndX=47.4 EndY=72.6064 EndZ=0
    g2: LineSegment StartX=-44.4 StartY=-74.4064 StartZ=0 EndX=-44.4 EndY=-70.8064 EndZ=0
    g3: LineSegment StartX=-44.4 StartY=-70.8064 StartZ=0 EndX=-41.2 EndY=-67.6064 EndZ=0
    g4: LineSegment StartX=-41.2 StartY=-67.6064 StartZ=0 EndX=-14.8 EndY=-67.6064 EndZ=0
    g5: LineSegment StartX=-14.8 StartY=-67.6064 StartZ=0 EndX=-11.6 EndY=-70.8064 EndZ=0
    g6: LineSegment StartX=-11.6 StartY=-70.8064 StartZ=0 EndX=-11.6 EndY=-74.4064 EndZ=0
    g7: LineSegment StartX=-11.6 StartY=-74.4064 StartZ=0 EndX=-14.8 EndY=-77.6064 EndZ=0
    g8: LineSegment StartX=-14.8 StartY=-77.6064 StartZ=0 EndX=-41.2 EndY=-77.6064 EndZ=0
    g9: LineSegment StartX=-41.2 StartY=-77.6064 StartZ=0 EndX=-44.4 EndY=-74.4064 EndZ=0
    g10: LineSegment StartX=11.6 StartY=74.4064 StartZ=0 EndX=14.8 EndY=77.6064 EndZ=0
    g11: LineSegment StartX=14.8 StartY=77.6064 StartZ=0 EndX=41.2 EndY=77.6064 EndZ=0
    g12: LineSegment StartX=41.2 StartY=77.6064 StartZ=0 EndX=44.4 EndY=74.4064 EndZ=0
    g13: LineSegment StartX=44.4 StartY=74.4064 StartZ=0 EndX=44.4 EndY=70.8064 EndZ=0
    g14: LineSegment StartX=44.4 StartY=70.8064 StartZ=0 EndX=41.2 EndY=67.6064 EndZ=0
    g15: LineSegment StartX=41.2 StartY=67.6064 StartZ=0 EndX=14.8 EndY=67.6064 EndZ=0
    g16: LineSegment StartX=14.8 StartY=67.6064 StartZ=0 EndX=11.6 EndY=70.8064 EndZ=0
    g17: LineSegment StartX=11.6 StartY=70.8064 StartZ=0 EndX=11.6 EndY=74.4064 EndZ=0
  constraints (47):
    c: PointOnObject(g0,g-2)
    c: PointOnObject(g0,g-3)
    c: Horizontal(g0)
    c: PointOnObject(g1,g-2)
    c: Symmetric(g1,g0,g-1)
    c: Distance(g1,g-1) = 72.6064
    c: Coincident(g2,g3)
    c: Coincident(g3,g4)
    c: Horizontal(g4)
    c: Coincident(g4,g5)
    c: Coincident(g5,g6)
    c: Coincident(g6,g7)
    c: Coincident(g7,g8)
    c: Coincident(g8,g9)
    c: Coincident(g9,g2)
    c: Symmetric(g8,g3,g0)
    c: Symmetric(g7,g4,g0)
    c: Perpendicular(g7,g5)
    c: Perpendicular(g9,g3)
    c: PointOnObject(g3,g-4)
    c: Symmetric(g2,g2,g0)
    c: Symmetric(g6,g5,g0)
    c: PointOnObject(g4,g-5)
    c: Distance(g4,g7) = 10
    c: DistanceX(g2,g3) = 3.2
    c: Equal(g3,g5)
    c: PointOnObject(g10,g-6)
    c: Coincident(g10,g11)
    c: PointOnObject(g11,g-7)
    c: Horizontal(g11)
    c: Coincident(g11,g12)
    c: Coincident(g12,g13)
    c: Coincident(g13,g14)
    c: PointOnObject(g14,g-7)
    c: Coincident(g14,g15)
    c: Coincident(g15,g16)
    c: Coincident(g16,g17)
    c: Coincident(g17,g10)
    c: Symmetric(g16,g10,g1)
    c: Symmetric(g15,g10,g1)
    c: Symmetric(g14,g11,g1)
    c: Symmetric(g13,g12,g1)
    c: Perpendicular(g12,g14)
    c: Perpendicular(g10,g16)
    c: Equal(g16,g5)
    c: Equal(g12,g9)
    c: Equal(g2,g17)
FEATURE [PartDesign::Pocket] Pocket034  label="FB_Pocket034"
  BaseFeature = -> Hole014
  Direction = (0,0,-1)
  Length = 5
  Length2 = 5
  Placement = pos=(0,0,0) rot=(1,1,1;2.0944rad)
  Profile = -> Sketch078
  ReferenceAxis = -> Sketch078 [N_Axis]
  Refine = true
  Suppressed = false
  Type = 1
FEATURE [PartDesign::Body] Body025  label="FrameBottom"
  AllowCompound = false
  Group = -> [Sketch067,Pad034,Sketch068,Sketch069,Pad035,Pocket027,Pocket028,Sketch070,Pocket029,Sketch071,Pocket030,Mirrored001,Sketch073,Sketch074,Pad036,Sketch075,Pad037,Pocket031,Hole012,PolarPattern002,Pocket032,Sketch076,Pad038,Sketch077,Pocket033,Hole014,Sketch078,Pocket034]
  Origin = -> Origin024
  Placement = pos=(0,0,-82.8064) rot=(0,0,1;0rad)
  Tip = -> Pocket034
  expr: .Placement.Base.z = -dd.FR_H / 2
FEATURE [Sketcher::SketchObject] Sketch079  label="S1_Sketch079"
  ArcFitTolerance = 1e-06
  AttachmentOffset = pos=(0,0,8.7) rot=(0,0,1;0rad)
  AttachmentSupport = -> [YZ_Plane023]
  FullyConstrained = true
  MakeInternals = false
  MapMode = 5
  Placement = pos=(8.7,0,0) rot=(0.57735,0.57735,0.57735;2.0944rad)
  expr: .AttachmentOffset.Base.z = dd.CL_BW / 2
  expr: Constraints[11] = dd.CL_Radius
  expr: Constraints[12] = dd.CL_Radius
  expr: Constraints[13] = dd.FR_H / 2 + 0.8 mm
  expr: Constraints[16] = dd.FR_H / 4
  expr: Constraints[1] = dd.CL_BD
  sketch-geometry (11):
    g0: Circle CenterX=0 CenterY=0 CenterZ=0 NormalX=0 NormalY=0 NormalZ=1 AngleXU=0 Radius=2.45
    g1: ArcOfCircle CenterX=0 CenterY=0 CenterZ=0 NormalX=0 NormalY=0 NormalZ=1 AngleXU=0 Radius=6 StartAngle=0 EndAngle=1.5708
    g2: LineSegment StartX=2.22546e-11 StartY=6 StartZ=0 EndX=-6 EndY=6 EndZ=0
    g3: LineSegment StartX=-6 StartY=6 StartZ=0 EndX=-6 EndY=-83.6064 EndZ=0
    g4: LineSegment StartX=6 StartY=-83.6064 StartZ=0 EndX=6 EndY=0 EndZ=0
    g5: Circle CenterX=0 CenterY=-41.4032 CenterZ=0 NormalX=0 NormalY=0 NormalZ=1 AngleXU=0 Radius=2.45
    g6: LineSegment StartX=-6 StartY=-83.6064 StartZ=0 EndX=-2.8 EndY=-83.6064 EndZ=0
    g7: LineSegment StartX=-2.8 StartY=-83.6064 StartZ=0 EndX=-2.8 EndY=-86.8064 EndZ=0
    g8: LineSegment StartX=-2.8 StartY=-86.8064 StartZ=0 EndX=2.8 EndY=-86.8064 EndZ=0
    g9: LineSegment StartX=2.8 StartY=-86.8064 StartZ=0 EndX=2.8 EndY=-83.6064 EndZ=0
    g10: LineSegment StartX=2.8 StartY=-83.6064 StartZ=0 EndX=6 EndY=-83.6064 EndZ=0
  constraints (30):
    c: Coincident(g0,g-1)
    c: Diameter(g0) = 4.9
    c: Coincident(g1,g0)
    c: Horizontal(g2)
    c: Coincident(g2,g3)
    c: Vertical(g3)
    c: Coincident(g3,g6)
    c: Coincident(g10,g4)
    c: Vertical(g4)
    c: Tangent(g4,g1) = -1.5708
    c: Tangent(g1,g2) = -1.5708
    c: Radius(g1) = 6
    c: Distance(g2,g2) = 6
    c: Distance(g3,g-1) = 83.6064
    c: PointOnObject(g5,g-2)
    c: Equal(g0,g5)
    c: Distance(g5,g-1) = 41.4032
    c: Coincident(g6,g7)
    c: Horizontal(g6)
    c: Coincident(g7,g8)
    c: Coincident(g8,g9)
    c: Horizontal(g8)
    c: Coincident(g9,g10)
    c: Horizontal(g10)
    c: Vertical(g7)
    c: Vertical(g9)
    c: PointOnObject(g4,g6)
    c: Distance(g7,g7) = 3.2
    c: Equal(g7,g6)
    c: Equal(g9,g10)
FEATURE [PartDesign::Pad] Pad039  label="S1_Pad039"
  Direction = (1,0,0)
  Length = 6
  Length2 = 1.6
  Placement = pos=(0,0,0) rot=(1,1,1;2.0944rad)
  Profile = -> Sketch079
  ReferenceAxis = -> Sketch079 [N_Axis]
  Refine = true
  Suppressed = false
  Type = 4
FEATURE [Sketcher::SketchObject] Sketch080  label="S1_Sketch080"
  ArcFitTolerance = 1e-06
  AttachmentOffset = pos=(0,0,8.7) rot=(0,0,1;0rad)
  AttachmentSupport = -> [YZ_Plane023]
  ExternalGeometry = -> [Pad039]
  FullyConstrained = true
  MakeInternals = false
  MapMode = 5
  Placement = pos=(8.7,0,0) rot=(0.57735,0.57735,0.57735;2.0944rad)
  expr: .AttachmentOffset.Base.z = dd.CL_BW / 2
  expr: Constraints[15] = 180 - 180 / dd.CL_Num
  expr: Constraints[16] = dd.CL_Radius
  expr: Constraints[3] = dd.CL_Radius
  expr: Constraints[6] = dd.CL_BD + 0.3 mm
  sketch-geometry (7):
    g0: ArcOfCircle CenterX=0 CenterY=0 CenterZ=0 NormalX=0 NormalY=0 NormalZ=1 AngleXU=0 Radius=6 StartAngle=4.71239 EndAngle=6.15752
    g1: LineSegment StartX=5.95269 StartY=-0.751999 StartZ=0 EndX=6 EndY=-0.377488 EndZ=0
    g2: LineSegment StartX=-6 StartY=-6 StartZ=0 EndX=-9e-16 EndY=-6 EndZ=0
    g3: Circle CenterX=0 CenterY=-41.4032 CenterZ=0 NormalX=0 NormalY=0 NormalZ=1 AngleXU=0 Radius=2.6
    g4: LineSegment StartX=-6 StartY=-6 StartZ=0 EndX=-6 EndY=6 EndZ=0
    g5: LineSegment StartX=-6 StartY=6 StartZ=0 EndX=6 EndY=6 EndZ=0
    g6: LineSegment StartX=6 StartY=6 StartZ=0 EndX=6 EndY=-0.377488 EndZ=0
  constraints (17):
    c: Coincident(g0,g-1)
    c: Tangent(g0,g2) = -1.5708
    c: Tangent(g0,g1) = -1.5708
    c: Radius(g0) = 6
    c: Horizontal(g2)
    c: Coincident(g3,g-3)
    c: Diameter(g3) = 5.2
    c: Coincident(g2,g4)
    c: Coincident(g4,g-4)
    c: Coincident(g4,g5)
    c: Horizontal(g5)
    c: Coincident(g5,g6)
    c: Coincident(g6,g1)
    c: Vertical(g6)
    c: Vertical(g4)
    c: Angle(g6,g1) = 3.01593
    c: DistanceX(g-4,g5) = 6
FEATURE [PartDesign::Pocket] Pocket035  label="S1_Pocket035"
  BaseFeature = -> Pad039
  Direction = (-1,0,0)
  Length = 5
  Length2 = 5
  Placement = pos=(0,0,0) rot=(1,1,1;2.0944rad)
  Profile = -> Sketch080
  ReferenceAxis = -> Sketch080 [N_Axis]
  Refine = true
  Reversed = true
  Suppressed = false
  Type = 1
FEATURE [PartDesign::Body] Body027  label="Support1"
  AllowCompound = false
  Group = -> [Sketch079,Pad039,Sketch080,Pocket035]
  Origin = -> Origin025
  Placement = pos=(-30.7,-72.6064,0) rot=(0,0,1;0rad)
  Tip = -> Pocket035
  expr: .Placement.Base.x = dd.D1_X
  expr: .Placement.Base.y = -dd.CD_Radius
FEATURE [Sketcher::SketchObject] Sketch081  label="S2_Sketch081"
  ArcFitTolerance = 1e-06
  AttachmentOffset = pos=(0,0,-8.7) rot=(0,0,1;0rad)
  AttachmentSupport = -> [YZ_Plane024]
  FullyConstrained = true
  MakeInternals = false
  MapMode = 5
  Placement = pos=(-8.7,0,0) rot=(0.57735,0.57735,0.57735;2.0944rad)
  expr: .AttachmentOffset.Base.z = -dd.CL_BW / 2
  expr: Constraints[19] = dd.CL_Radius
  expr: Constraints[23] = dd.CL_BD
  expr: Constraints[24] = dd.FR_H / 4
  expr: Constraints[31] = dd.FR_H / 2 + 0.8 mm
  sketch-geometry (12):
    g0: ArcOfCircle CenterX=0 CenterY=0 CenterZ=0 NormalX=0 NormalY=0 NormalZ=1 AngleXU=0 Radius=6 StartAngle=0 EndAngle=1.5708
    g1: LineSegment StartX=4e-16 StartY=6 StartZ=0 EndX=-6 EndY=6 EndZ=0
    g2: LineSegment StartX=-6 StartY=6 StartZ=0 EndX=-6 EndY=-83.6064 EndZ=0
    g3: LineSegment StartX=-6 StartY=-83.6064 StartZ=0 EndX=-2.8 EndY=-83.6064 EndZ=0
    g4: LineSegment StartX=-2.8 StartY=-83.6064 StartZ=0 EndX=-2.8 EndY=-86.8064 EndZ=0
    g5: LineSegment StartX=-2.8 StartY=-86.8064 StartZ=0 EndX=2.8 EndY=-86.8064 EndZ=0
    g6: LineSegment StartX=2.8 StartY=-86.8064 StartZ=0 EndX=2.8 EndY=-83.6064 EndZ=0
    g7: LineSegment StartX=2.8 StartY=-83.6064 StartZ=0 EndX=6 EndY=-83.6064 EndZ=0
    g8: LineSegment StartX=6 StartY=-83.6064 StartZ=0 EndX=6 EndY=0 EndZ=0
    g9: LineSegment [constr] StartX=0 StartY=0 StartZ=0 EndX=6 EndY=0 EndZ=0
    g10: Circle CenterX=0 CenterY=0 CenterZ=0 NormalX=0 NormalY=0 NormalZ=1 AngleXU=0 Radius=2.45
    g11: Circle CenterX=0 CenterY=-41.4032 CenterZ=0 NormalX=0 NormalY=0 NormalZ=1 AngleXU=0 Radius=2.45
  constraints (32):
    c: Coincident(g0,g-1)
    c: Horizontal(g1)
    c: Coincident(g1,g2)
    c: Vertical(g2)
    c: Coincident(g2,g3)
    c: Coincident(g3,g4)
    c: Vertical(g4)
    c: Coincident(g4,g5)
    c: Coincident(g5,g6)
    c: Vertical(g6)
    c: Coincident(g6,g7)
    c: Horizontal(g7)
    c: Coincident(g7,g8)
    c: Vertical(g8)
    c: Tangent(g0,g8) = -1.5708
    c: Tangent(g0,g1) = -1.5708
    c: Coincident(g9,g0)
    c: Coincident(g9,g0)
    c: Equal(g9,g1)
    c: Radius(g0) = 6
    c: Coincident(g10,g0)
    c: PointOnObject(g11,g-2)
    c: Equal(g11,g10)
    c: Diameter(g11) = 4.9
    c: Distance(g11,g-1) = 41.4032
    c: PointOnObject(g7,g3)
    c: Horizontal(g3)
    c: Distance(g3,g3) = 3.2
    c: Equal(g3,g4)
    c: Horizontal(g5)
    c: Equal(g6,g7)
    c: Distance(g2,g-1) = 83.6064
FEATURE [PartDesign::Pad] Pad040  label="S2_Pad040"
  Direction = (1,0,0)
  Length = 1.6
  Length2 = 1.6
  Placement = pos=(0,0,0) rot=(1,1,1;2.0944rad)
  Profile = -> Sketch081
  ReferenceAxis = -> Sketch081 [N_Axis]
  Refine = true
  Suppressed = false
  Type = 4
FEATURE [Sketcher::SketchObject] Sketch082  label="S2_Sketch082"
  ArcFitTolerance = 1e-06
  AttachmentOffset = pos=(0,0,-8.7) rot=(0,0,1;0rad)
  AttachmentSupport = -> [YZ_Plane024]
  ExternalGeometry = -> [Pad040]
  FullyConstrained = true
  MakeInternals = false
  MapMode = 5
  Placement = pos=(-8.7,0,0) rot=(0.57735,0.57735,0.57735;2.0944rad)
  expr: .AttachmentOffset.Base.z = -dd.CL_BW / 2
  expr: Constraints[14] = 180 - 180 / dd.CL_Num
  sketch-geometry (6):
    g0: ArcOfCircle CenterX=0 CenterY=0 CenterZ=0 NormalX=0 NormalY=0 NormalZ=1 AngleXU=0 Radius=6 StartAngle=4.71239 EndAngle=6.15752
    g1: LineSegment StartX=5.95269 StartY=-0.751999 StartZ=0 EndX=6 EndY=-0.377488 EndZ=0
    g2: LineSegment StartX=6 StartY=-0.377488 StartZ=0 EndX=6 EndY=6 EndZ=0
    g3: LineSegment StartX=6 StartY=6 StartZ=0 EndX=-6 EndY=6 EndZ=0
    g4: LineSegment StartX=-6 StartY=6 StartZ=0 EndX=-6 EndY=-6 EndZ=0
    g5: LineSegment StartX=-6 StartY=-6 StartZ=0 EndX=-9e-16 EndY=-6 EndZ=0
  constraints (15):
    c: Coincident(g0,g-1)
    c: Coincident(g1,g2)
    c: Vertical(g2)
    c: Coincident(g2,g3)
    c: Coincident(g3,g-4)
    c: Horizontal(g3)
    c: Coincident(g3,g4)
    c: Vertical(g4)
    c: Coincident(g4,g5)
    c: Horizontal(g5)
    c: Tangent(g0,g1) = -1.5708
    c: Tangent(g0,g5) = -1.5708
    c: Equal(g-3,g0)
    c: PointOnObject(g-3,g2)
    c: Angle(g2,g1) = 3.01593
FEATURE [PartDesign::Pocket] Pocket036  label="S2_Pocket036"
  BaseFeature = -> Pad040
  Direction = (-1,0,0)
  Length = 5
  Length2 = 5
  Placement = pos=(0,0,0) rot=(1,1,1;2.0944rad)
  Profile = -> Sketch082
  ReferenceAxis = -> Sketch082 [N_Axis]
  Refine = true
  Suppressed = false
  Type = 1
FEATURE [PartDesign::Body] Body028  label="Support2"
  AllowCompound = false
  Group = -> [Sketch081,Pad040,Sketch082,Pocket036]
  Origin = -> Origin026
  Placement = pos=(-30.7,-72.6064,0) rot=(0,0,1;0rad)
  Tip = -> Pocket036
  expr: .Placement.Base.x = dd.D1_X
  expr: .Placement.Base.y = -dd.CD_Radius
FEATURE [PartDesign::SubShapeBinder] Binder018  label="S3_Binder018"
  BindCopyOnChange = 0
  BindMode = 0
  ClaimChildren = false
  Context = -> Body029 [Binder018.]
  Fuse = false
  MakeFace = true
  OffsetFill = false
  OffsetIntersection = false
  OffsetJoinType = 0
  OffsetOpenResult = false
  PartialLoad = false
  Refine = true
  Relative = true
  Support = -> [Body028[Pocket036.Face4,Pocket036.Face13],Body027[Pocket035.Face7,Pocket035.Face11]]
  _Version = 2
FEATURE [Sketcher::SketchObject] Sketch083  label="S3_Sketch083"
  ArcFitTolerance = 1e-06
  AttachmentOffset = pos=(0,0,-86.8064) rot=(0,0,1;0rad)
  AttachmentSupport = -> [XY_Plane025]
  ExternalGeometry = -> [Binder018]
  FullyConstrained = true
  MakeInternals = false
  MapMode = 5
  Placement = pos=(0,0,-86.8064) rot=(0,0,1;0rad)
  expr: .AttachmentOffset.Base.z = -(dd.FR_H / 2 + 4 mm)
  expr: Constraints[55] = dd.FR_W
  sketch-geometry (21):
    g0: LineSegment StartX=-42.6 StartY=-102 StartZ=0 EndX=42.6 EndY=-102 EndZ=0
    g1: LineSegment StartX=42.6 StartY=-102 StartZ=0 EndX=42.6 EndY=102 EndZ=0
    g2: LineSegment StartX=42.6 StartY=102 StartZ=0 EndX=-42.6 EndY=102 EndZ=0
    g3: LineSegment StartX=-42.6 StartY=102 StartZ=0 EndX=-42.6 EndY=-102 EndZ=0
    g4: LineSegment [constr] StartX=-41 StartY=-75.4064 StartZ=0 EndX=-42.6 EndY=-75.4064 EndZ=0
    g5: LineSegment StartX=-41 StartY=-69.8064 StartZ=0 EndX=-41 EndY=-75.4064 EndZ=0
    g6: LineSegment StartX=-41 StartY=-75.4064 StartZ=0 EndX=-37.8 EndY=-75.4064 EndZ=0
    g7: LineSegment StartX=-37.8 StartY=-75.4064 StartZ=0 EndX=-37.8 EndY=-69.8064 EndZ=0
    g8: LineSegment StartX=-37.8 StartY=-69.8064 StartZ=0 EndX=-41 EndY=-69.8064 EndZ=0
    g9: LineSegment StartX=-23.6 StartY=-75.4064 StartZ=0 EndX=-16 EndY=-75.4064 EndZ=0
    g10: LineSegment StartX=-16 StartY=-75.4064 StartZ=0 EndX=-16 EndY=-69.8064 EndZ=0
    g11: LineSegment StartX=-16 StartY=-69.8064 StartZ=0 EndX=-23.6 EndY=-69.8064 EndZ=0
    g12: LineSegment StartX=-23.6 StartY=-69.8064 StartZ=0 EndX=-23.6 EndY=-75.4064 EndZ=0
    g13: LineSegment StartX=41 StartY=75.4064 StartZ=0 EndX=37.8 EndY=75.4064 EndZ=0
    g14: LineSegment StartX=37.8 StartY=75.4064 StartZ=0 EndX=37.8 EndY=69.8064 EndZ=0
    g15: LineSegment StartX=37.8 StartY=69.8064 StartZ=0 EndX=41 EndY=69.8064 EndZ=0
    g16: LineSegment StartX=41 StartY=69.8064 StartZ=0 EndX=41 EndY=75.4064 EndZ=0
    g17: LineSegment StartX=23.6 StartY=75.4064 StartZ=0 EndX=16 EndY=75.4064 EndZ=0
    g18: LineSegment StartX=16 StartY=75.4064 StartZ=0 EndX=16 EndY=69.8064 EndZ=0
    g19: LineSegment StartX=16 StartY=69.8064 StartZ=0 EndX=23.6 EndY=69.8064 EndZ=0
    g20: LineSegment StartX=23.6 StartY=69.8064 StartZ=0 EndX=23.6 EndY=75.4064 EndZ=0
  constraints (56):
    c: Coincident(g0,g1)
    c: Coincident(g1,g2)
    c: Coincident(g2,g3)
    c: Coincident(g3,g0)
    c: Horizontal(g0)
    c: Horizontal(g2)
    c: Vertical(g1)
    c: Vertical(g3)
    c: Symmetric(g0,g2,g-1)
    c: Coincident(g4,g-3)
    c: PointOnObject(g4,g3)
    c: Horizontal(g4)
    c: Distance(g4,g4) = 1.6
    c: Coincident(g5,g6)
    c: Coincident(g6,g7)
    c: Coincident(g7,g8)
    c: Coincident(g8,g5)
    c: Vertical(g5)
    c: Vertical(g7)
    c: Horizontal(g6)
    c: Horizontal(g8)
    c: Coincident(g5,g-3)
    c: Coincident(g6,g-5)
    c: Coincident(g9,g10)
    c: Coincident(g10,g11)
    c: Coincident(g11,g12)
    c: Coincident(g12,g9)
    c: Horizontal(g9)
    c: Horizontal(g11)
    c: Vertical(g10)
    c: Vertical(g12)
    c: PointOnObject(g-4,g10)
    c: PointOnObject(g-4,g12)
    c: PointOnObject(g9,g6)
    c: PointOnObject(g11,g8)
    c: Coincident(g13,g14)
    c: Coincident(g14,g15)
    c: Coincident(g15,g16)
    c: Coincident(g16,g13)
    c: Horizontal(g13)
    c: Horizontal(g15)
    c: Vertical(g14)
    c: Vertical(g16)
    c: Coincident(g17,g18)
    c: Coincident(g18,g19)
    c: Coincident(g19,g20)
    c: Coincident(g20,g17)
    c: Horizontal(g17)
    c: Horizontal(g19)
    c: Vertical(g18)
    c: Vertical(g20)
    c: Symmetric(g10,g18,g-1)
    c: Symmetric(g9,g17,g-1)
    c: Symmetric(g13,g4,g-1)
    c: Symmetric(g14,g7,g-1)
    c: DistanceY(g1,g1) = 204
FEATURE [PartDesign::Pad] Pad041  label="S3_Pad041"
  Direction = (0,0,1)
  Length = 3.2
  Length2 = 10
  Profile = -> Sketch083
  ReferenceAxis = -> Sketch083 [N_Axis]
  Refine = true
  Suppressed = false
  Type = 0
  expr: Length = 3.2 mm
FEATURE [Sketcher::SketchObject] Sketch084  label="S3_Sketch084"
  ArcFitTolerance = 1e-06
  AttachmentOffset = pos=(0,0,-30.7) rot=(0,0,1;0rad)
  AttachmentSupport = -> [YZ_Plane025]
  ExternalGeometry = -> [Binder018]
  FullyConstrained = true
  MakeInternals = false
  MapMode = 5
  Placement = pos=(-30.7,0,0) rot=(0.57735,0.57735,0.57735;2.0944rad)
  expr: .AttachmentOffset.Base.z = dd.D1_X
  expr: Constraints[0] = dd.CD_Radius + 3.2 mm
  sketch-geometry (7):
    g0: ArcOfCircle CenterX=0 CenterY=0 CenterZ=0 NormalX=0 NormalY=0 NormalZ=1 AngleXU=0 Radius=75.8064 StartAngle=3.14159 EndAngle=3.63939
    g1: LineSegment StartX=-75.8064 StartY=-2.44e-14 StartZ=0 EndX=-75.8064 EndY=6 EndZ=0
    g2: LineSegment StartX=-75.8064 StartY=6 StartZ=0 EndX=-78.6064 EndY=6 EndZ=0
    g3: LineSegment StartX=-78.6064 StartY=6 StartZ=0 EndX=-78.6064 EndY=-83.6064 EndZ=0
    g4: LineSegment StartX=-78.6064 StartY=-83.6064 StartZ=0 EndX=-66.6064 EndY=-83.6064 EndZ=0
    g5: LineSegment StartX=-66.6064 StartY=-83.6064 StartZ=0 EndX=-66.6064 EndY=-36.1967 EndZ=0
    g6: Circle CenterX=-72.6064 CenterY=-41.4032 CenterZ=0 NormalX=0 NormalY=0 NormalZ=1 AngleXU=0 Radius=2.45
  constraints (17):
    c: Radius(g0) = 75.8064
    c: Coincident(g0,g-1)
    c: Vertical(g1)
    c: Coincident(g1,g2)
    c: Horizontal(g2)
    c: Coincident(g2,g3)
    c: Vertical(g3)
    c: Coincident(g3,g4)
    c: Coincident(g4,g-4)
    c: Horizontal(g4)
    c: Coincident(g4,g5)
    c: Coincident(g5,g0)
    c: Vertical(g5)
    c: Tangent(g0,g1) = 1.5708
    c: Coincident(g6,g-5)
    c: Equal(g6,g-5)
    c: Coincident(g-3,g2)
FEATURE [PartDesign::Pad] Pad042  label="S3_Pad042"
  BaseFeature = -> Pad041
  Direction = (1,0,0)
  Length = 14.2
  Length2 = 10
  Midplane = true
  Profile = -> Sketch084
  ReferenceAxis = -> Sketch084 [N_Axis]
  Refine = true
  Suppressed = false
  Type = 0
  expr: Length = dd.CL_BW - 3.2 mm
FEATURE [Sketcher::SketchObject] Sketch085  label="S3_Sketch085"
  ArcFitTolerance = 1e-06
  AttachmentOffset = pos=(0,0,-30.7) rot=(0,0,1;0rad)
  AttachmentSupport = -> [YZ_Plane025]
  ExternalGeometry = -> [Pad042]
  FullyConstrained = true
  MakeInternals = false
  MapMode = 5
  Placement = pos=(-30.7,0,0) rot=(0.57735,0.57735,0.57735;2.0944rad)
  expr: .AttachmentOffset.Base.z = dd.D1_X
  expr: Constraints[10] = dd.CL_Radius
  sketch-geometry (4):
    g0: LineSegment StartX=-78.6064 StartY=-6 StartZ=0 EndX=-80.2064 EndY=-6 EndZ=0
    g1: LineSegment StartX=-80.2064 StartY=-6 StartZ=0 EndX=-80.2064 EndY=-83.6064 EndZ=0
    g2: LineSegment StartX=-80.2064 StartY=-83.6064 StartZ=0 EndX=-78.6064 EndY=-83.6064 EndZ=0
    g3: LineSegment StartX=-78.6064 StartY=-83.6064 StartZ=0 EndX=-78.6064 EndY=-6 EndZ=0
  constraints (11):
    c: Coincident(g0,g1)
    c: Coincident(g1,g2)
    c: Coincident(g2,g3)
    c: Coincident(g3,g0)
    c: Horizontal(g0)
    c: Horizontal(g2)
    c: Vertical(g1)
    c: Coincident(g2,g-3)
    c: Distance(g0,g0) = 1.6
    c: PointOnObject(g0,g-3)
    c: Distance(g0,g-1) = 6
FEATURE [PartDesign::Pad] Pad043  label="S3_Pad043"
  BaseFeature = -> Pad042
  Direction = (1,0,0)
  Length = 10.3
  Length2 = 14.7
  Profile = -> Sketch085
  ReferenceAxis = -> Sketch085 [N_Axis]
  Refine = true
  Reversed = true
  Suppressed = false
  Type = 4
  expr: Length = dd.CL_BW / 2 + 1.6 mm
  expr: Length2 = dd.CL_BW / 2 + 6 mm
FEATURE [PartDesign::PolarPattern] PolarPattern003  label="S3_PolarPattern003"
  Angle = 360
  Axis = -> Z_Axis025
  BaseFeature = -> Pad043
  Mode = 0
  Occurrences = 2
  Offset = 120
  Originals = -> [Pad042,Pad043]
  Refine = true
  Suppressed = false
  TransformMode = 0
FEATURE [Sketcher::SketchObject] Sketch086  label="S3_Sketch086"
  ArcFitTolerance = 1e-06
  AttachmentOffset = pos=(0,0,-83.6064) rot=(0,0,1;0rad)
  AttachmentSupport = -> [XY_Plane025]
  FullyConstrained = true
  MakeInternals = false
  MapMode = 5
  Placement = pos=(0,0,-83.6064) rot=(0,0,1;0rad)
  expr: .AttachmentOffset.Base.z = -(dd.FR_H / 2 + 0.8 mm)
  sketch-geometry (4):
    g0: LineSegment StartX=-3.2 StartY=-1.6 StartZ=0 EndX=3.2 EndY=-1.6 EndZ=0
    g1: LineSegment StartX=3.2 StartY=-1.6 StartZ=0 EndX=3.2 EndY=1.6 EndZ=0
    g2: LineSegment StartX=3.2 StartY=1.6 StartZ=0 EndX=-3.2 EndY=1.6 EndZ=0
    g3: LineSegment StartX=-3.2 StartY=1.6 StartZ=0 EndX=-3.2 EndY=-1.6 EndZ=0
  constraints (11):
    c: Coincident(g0,g1)
    c: Coincident(g1,g2)
    c: Coincident(g2,g3)
    c: Coincident(g3,g0)
    c: Horizontal(g0)
    c: Horizontal(g2)
    c: Vertical(g1)
    c: Vertical(g3)
    c: Symmetric(g2,g0,g-1)
    c: Distance(g3,g3) = 3.2
    c: DistanceX(g2,g2) = 6.4
FEATURE [PartDesign::Pad] Pad044  label="S3_Pad044"
  BaseFeature = -> PolarPattern003
  Direction = (0,0,1)
  Length = 5
  Length2 = 10
  Profile = -> Sketch086
  ReferenceAxis = -> Sketch086 [N_Axis]
  Refine = true
  Suppressed = false
  Type = 0
FEATURE [PartDesign::Body] Body029  label="Support3"
  AllowCompound = false
  Group = -> [Binder018,Sketch083,Pad041,Sketch084,Pad042,Sketch085,Pad043,PolarPattern003,Sketch086,Pad044]
  Origin = -> Origin027
  Tip = -> Pad044
